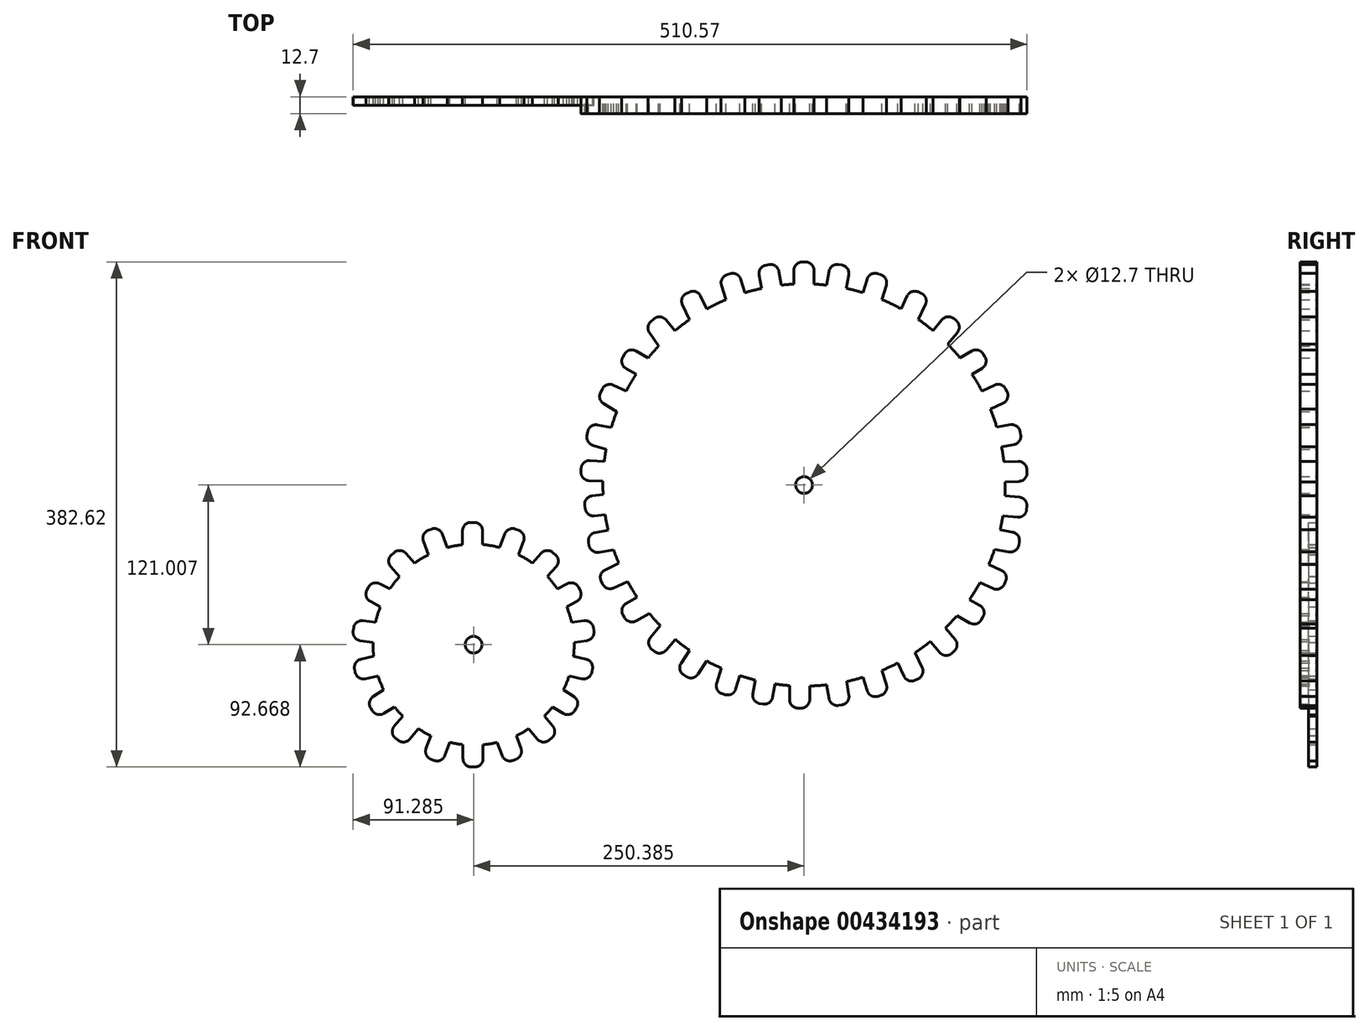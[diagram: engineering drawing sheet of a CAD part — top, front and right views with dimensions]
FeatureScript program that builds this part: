
annotation { "Feature Type Name" : "Feature", "Feature Type Description" : "" }
export const myFeature = defineFeature(function(context is Context, id is Id, definition is map)
    precondition{}
    {
        {
            var Q0;
            Q0=qCreatedBy(makeId("Front.planeOp"),FACE);
            var sketch = newSketch(context, id + "F0", { "sketchPlane" : qUnion([Q0])});
            skCircle(sketch, "E0", {"center": v(106.38, 71.68) * mm, "radius": 152.4 * mm});
            skCircle(sketch, "E1", {"center": v(-144, -49.32) * mm, "radius": 76.2 * mm});
            skCircle(sketch, "E2", {"center": v(-144, -49.32) * mm, "radius": 6.35 * mm});
            skCircle(sketch, "E3", {"center": v(106.38, 71.68) * mm, "radius": 6.35 * mm});
            skSolve(sketch);
        }
        {
            var Q0;
            Q0=makeQuery(id+"F0.imprint","IMPRINT",FACE,{"disambiguationData":[TD([[makeQuery(id+"F0.imprint","IMPRINT",EDGE,{"derivedFrom":sQuery(id+"F0.wireOp",EDGE,"E0")}),1.0]])]});
            extrude(context, id + "F1", {"entities" : qUnion([Q0]), "depth" : 12.7 * mm});
        }
        {
            var Q0;
            Q0 = qSketchRegion(id + "F0", true);
            extrude(context, id + "F2", {"entities" : qUnion([Q0]), "depth" : 6.35 * mm});
        }
        {
            var Q0;
            Q0=qCreatedBy(makeId("Front.planeOp"),FACE);
            var sketch = newSketch(context, id + "F3", { "sketchPlane" : qUnion([Q0])});
            skLineSegment(sketch, "E4.bottom", {"start": v(-146.1, 43.29) * mm, "end": v(-143.56, 43.29) * mm});
            skLineSegment(sketch, "E4.top", {"start": v(-152.45, 22.97) * mm, "end": v(-137.2, 22.97) * mm});
            skLineSegment(sketch, "E4.left", {"start": v(-152.45, 36.94) * mm, "end": v(-152.45, 22.97) * mm});
            skLineSegment(sketch, "E4.right", {"start": v(-137.2, 36.94) * mm, "end": v(-137.2, 22.97) * mm});
            skLineSegment(sketch, "E5", {"start": v(-136.92, 40.56) * mm, "end": v(-135.42, 26.4) * mm});
            skLineSegment(sketch, "E6", {"start": v(-137.2, 22.97) * mm, "end": v(-138.5, 22.97) * mm});
            skLineSegment(sketch, "E7", {"start": v(-152.67, 40.47) * mm, "end": v(-153.76, 26.25) * mm});
            skLineSegment(sketch, "E8", {"start": v(-152.45, 22.97) * mm, "end": v(-150.72, 22.97) * mm});
            skPoint(sketch, "E9.visualSharp", {"position": v(-152.45, 43.29) * mm});
            skArc(sketch, "E9.filletArc", {"start": v(-149.63, 43.29) * mm, "mid": v(-151.7, 42.48) * mm, "end": v(-152.67, 40.47) * mm});
            skPoint(sketch, "E10.visualSharp", {"position": v(-137.2, 43.29) * mm});
            skArc(sketch, "E10.filletArc", {"start": v(-136.92, 40.56) * mm, "mid": v(-137.91, 42.5) * mm, "end": v(-139.95, 43.29) * mm});
            skPoint(sketch, "E11.visualSharp", {"position": v(-154.01, 22.97) * mm});
            skArc(sketch, "E11.filletArc", {"start": v(-153.76, 26.25) * mm, "mid": v(-152.96, 23.95) * mm, "end": v(-150.72, 22.97) * mm});
            skPoint(sketch, "E12.visualSharp", {"position": v(-135.06, 22.97) * mm});
            skArc(sketch, "E12.filletArc", {"start": v(-138.5, 22.97) * mm, "mid": v(-136.2, 24) * mm, "end": v(-135.42, 26.4) * mm});
            skLineSegment(sketch, "E13.MirrorCS", {"start": v(-136.79, -121.67) * mm, "end": v(-138.04, -121.67) * mm});
            skLineSegment(sketch, "E14.MirrorCS", {"start": v(-152.03, -121.67) * mm, "end": v(-150.3, -121.67) * mm});
            skArc(sketch, "E15.MirrorCS", {"start": v(-138.04, -121.67) * mm, "mid": v(-135.8, -122.66) * mm, "end": v(-135.01, -124.99) * mm});
            skArc(sketch, "E16.MirrorCS", {"start": v(-149.2, -141.99) * mm, "mid": v(-151.28, -141.18) * mm, "end": v(-152.24, -139.17) * mm});
            skArc(sketch, "E17.MirrorCS", {"start": v(-136.5, -139.21) * mm, "mid": v(-137.48, -141.19) * mm, "end": v(-139.53, -141.99) * mm});
            skArc(sketch, "E18.MirrorCS", {"start": v(-153.34, -124.95) * mm, "mid": v(-152.54, -122.64) * mm, "end": v(-150.3, -121.67) * mm});
            skPoint(sketch, "E19.MirrorP", {"position": v(-152.03, -141.99) * mm});
            skLineSegment(sketch, "E20.MirrorCS", {"start": v(-152.03, -121.67) * mm, "end": v(-136.79, -121.67) * mm});
            skLineSegment(sketch, "E21.MirrorCS", {"start": v(-136.5, -139.21) * mm, "end": v(-135.01, -124.99) * mm});
            skPoint(sketch, "E22.MirrorP", {"position": v(-135, -124.52) * mm});
            skPoint(sketch, "E23.MirrorP", {"position": v(-136.79, -141.99) * mm});
            skLineSegment(sketch, "E24.MirrorCS", {"start": v(-152.03, -135.64) * mm, "end": v(-152.03, -121.67) * mm});
            skLineSegment(sketch, "E25.MirrorCS", {"start": v(-152.24, -139.17) * mm, "end": v(-153.34, -124.95) * mm});
            skLineSegment(sketch, "E26.MirrorCS", {"start": v(-145.68, -141.99) * mm, "end": v(-143.14, -141.99) * mm});
            skLineSegment(sketch, "E27.MirrorCS", {"start": v(-136.79, -135.64) * mm, "end": v(-136.79, -121.67) * mm});
            skPoint(sketch, "E28.MirrorP", {"position": v(-153.94, -124.52) * mm});
            skLineSegment(sketch, "E29.bottom", {"start": v(-178.32, 37.32) * mm, "end": v(-175.94, 38.23) * mm});
            skLineSegment(sketch, "E29.top", {"start": v(-176.8, 15.57) * mm, "end": v(-162.56, 21.01) * mm});
            skLineSegment(sketch, "E29.left", {"start": v(-181.98, 29.13) * mm, "end": v(-176.8, 15.57) * mm});
            skLineSegment(sketch, "E29.right", {"start": v(-167.75, 34.57) * mm, "end": v(-162.56, 21.01) * mm});
            skLineSegment(sketch, "E30", {"start": v(-168.8, 37.96) * mm, "end": v(-162.41, 24.62) * mm});
            skLineSegment(sketch, "E31", {"start": v(-162.56, 21.01) * mm, "end": v(-164.08, 20.43) * mm});
            skLineSegment(sketch, "E32", {"start": v(-183.5, 32.38) * mm, "end": v(-179.51, 18.1) * mm});
            skLineSegment(sketch, "E33", {"start": v(-176.8, 15.57) * mm, "end": v(-175.49, 16.07) * mm});
            skPoint(sketch, "E34.visualSharp", {"position": v(-184.25, 35.06) * mm});
            skArc(sketch, "E34.filletArc", {"start": v(-181.65, 36.05) * mm, "mid": v(-183.29, 34.57) * mm, "end": v(-183.5, 32.38) * mm});
            skPoint(sketch, "E35.visualSharp", {"position": v(-170.01, 40.5) * mm});
            skArc(sketch, "E35.filletArc", {"start": v(-168.8, 37.96) * mm, "mid": v(-170.42, 39.48) * mm, "end": v(-172.64, 39.5) * mm});
            skPoint(sketch, "E36.visualSharp", {"position": v(-178.61, 14.88) * mm});
            skArc(sketch, "E36.filletArc", {"start": v(-179.51, 18.1) * mm, "mid": v(-177.95, 16.2) * mm, "end": v(-175.49, 16.07) * mm});
            skPoint(sketch, "E37.visualSharp", {"position": v(-160.97, 21.62) * mm});
            skArc(sketch, "E37.filletArc", {"start": v(-164.08, 20.43) * mm, "mid": v(-162.33, 22.16) * mm, "end": v(-162.41, 24.62) * mm});
            skLineSegment(sketch, "E38.0", {"start": v(-162.56, 21.01) * mm, "end": v(-160.97, 21.62) * mm, "construction": true});
            skLineSegment(sketch, "E39.0", {"start": v(-178.61, 14.88) * mm, "end": v(-176.8, 15.57) * mm, "construction": true});
            skLineSegment(sketch, "E40.bottom", {"start": v(-206.24, 18.7) * mm, "end": v(-204.35, 20.4) * mm});
            skLineSegment(sketch, "E40.top", {"start": v(-197.6, -0.33) * mm, "end": v(-186.3, 9.88) * mm});
            skLineSegment(sketch, "E40.left", {"start": v(-206.7, 9.73) * mm, "end": v(-197.6, -0.33) * mm});
            skLineSegment(sketch, "E40.right", {"start": v(-195.39, 19.95) * mm, "end": v(-186.3, 9.88) * mm});
            skLineSegment(sketch, "E41", {"start": v(-197.6, 22.9) * mm, "end": v(-186.87, 13.68) * mm});
            skLineSegment(sketch, "E42", {"start": v(-186.3, 9.88) * mm, "end": v(-186.82, 9.4) * mm});
            skLineSegment(sketch, "E43", {"start": v(-209.38, 12.24) * mm, "end": v(-201.32, 0.9) * mm});
            skLineSegment(sketch, "E44", {"start": v(-197.6, -0.33) * mm, "end": v(-196.8, 0.4) * mm});
            skPoint(sketch, "E45.visualSharp", {"position": v(-210.95, 14.45) * mm});
            skArc(sketch, "E45.filletArc", {"start": v(-208.94, 16.26) * mm, "mid": v(-209.93, 14.33) * mm, "end": v(-209.38, 12.24) * mm});
            skPoint(sketch, "E46.visualSharp", {"position": v(-199.64, 24.66) * mm});
            skArc(sketch, "E46.filletArc", {"start": v(-197.6, 22.9) * mm, "mid": v(-199.63, 23.65) * mm, "end": v(-201.64, 22.86) * mm});
            skPoint(sketch, "E47.visualSharp", {"position": v(-199.33, -1.9) * mm});
            skArc(sketch, "E47.filletArc", {"start": v(-201.32, 0.9) * mm, "mid": v(-199.17, -0.37) * mm, "end": v(-196.8, 0.4) * mm});
            skPoint(sketch, "E48.visualSharp", {"position": v(-184.42, 11.57) * mm});
            skArc(sketch, "E48.filletArc", {"start": v(-186.82, 9.4) * mm, "mid": v(-185.88, 11.55) * mm, "end": v(-186.87, 13.68) * mm});
            skLineSegment(sketch, "E49.0", {"start": v(-186.3, 9.88) * mm, "end": v(-184.42, 11.57) * mm, "construction": true});
            skLineSegment(sketch, "E50.0", {"start": v(-199.33, -1.9) * mm, "end": v(-197.6, -0.33) * mm, "construction": true});
            skLineSegment(sketch, "E51.bottom", {"start": v(-224.8, -8.03) * mm, "end": v(-223.6, -5.78) * mm});
            skLineSegment(sketch, "E51.top", {"start": v(-211.59, -22.22) * mm, "end": v(-204.45, -8.76) * mm});
            skLineSegment(sketch, "E51.left", {"start": v(-222.16, -16.61) * mm, "end": v(-211.59, -22.22) * mm});
            skLineSegment(sketch, "E51.right", {"start": v(-215.02, -3.15) * mm, "end": v(-204.45, -8.76) * mm});
            skLineSegment(sketch, "E52", {"start": v(-218.1, -1.16) * mm, "end": v(-206.48, -5.7) * mm});
            skLineSegment(sketch, "E53", {"start": v(-204.45, -8.76) * mm, "end": v(-204.98, -9.76) * mm});
            skLineSegment(sketch, "E54", {"start": v(-225.38, -15.15) * mm, "end": v(-215.02, -21.7) * mm});
            skLineSegment(sketch, "E55", {"start": v(-211.59, -22.22) * mm, "end": v(-210.7, -20.55) * mm});
            skPoint(sketch, "E56.visualSharp", {"position": v(-227.77, -13.64) * mm});
            skArc(sketch, "E56.filletArc", {"start": v(-226.45, -11.14) * mm, "mid": v(-226.7, -13.35) * mm, "end": v(-225.38, -15.15) * mm});
            skPoint(sketch, "E57.visualSharp", {"position": v(-220.63, -0.17) * mm});
            skArc(sketch, "E57.filletArc", {"start": v(-218.1, -1.16) * mm, "mid": v(-220.27, -1.14) * mm, "end": v(-221.9, -2.57) * mm});
            skPoint(sketch, "E58.visualSharp", {"position": v(-212.24, -23.46) * mm});
            skArc(sketch, "E58.filletArc", {"start": v(-215.02, -21.7) * mm, "mid": v(-212.61, -22.07) * mm, "end": v(-210.7, -20.55) * mm});
            skPoint(sketch, "E59.visualSharp", {"position": v(-203.45, -6.89) * mm});
            skArc(sketch, "E59.filletArc", {"start": v(-204.98, -9.76) * mm, "mid": v(-204.82, -7.4) * mm, "end": v(-206.48, -5.7) * mm});
            skLineSegment(sketch, "E60.0", {"start": v(-212.24, -23.46) * mm, "end": v(-211.59, -22.22) * mm, "construction": true});
            skLineSegment(sketch, "E61.0", {"start": v(-204.45, -8.76) * mm, "end": v(-203.45, -6.89) * mm, "construction": true});
            skLineSegment(sketch, "E62.bottom", {"start": v(-235.23, -39.12) * mm, "end": v(-234.88, -36.6) * mm});
            skLineSegment(sketch, "E62.top", {"start": v(-216.79, -48.1) * mm, "end": v(-214.69, -33) * mm});
            skLineSegment(sketch, "E62.left", {"start": v(-229.81, -46.29) * mm, "end": v(-216.79, -48.1) * mm});
            skLineSegment(sketch, "E62.right", {"start": v(-227.7, -31.2) * mm, "end": v(-214.69, -33) * mm});
            skLineSegment(sketch, "E63", {"start": v(-231.27, -30.4) * mm, "end": v(-217.91, -30.78) * mm});
            skLineSegment(sketch, "E64", {"start": v(-214.69, -33) * mm, "end": v(-214.88, -34.37) * mm});
            skLineSegment(sketch, "E65", {"start": v(-233.34, -46) * mm, "end": v(-220.2, -48.86) * mm});
            skLineSegment(sketch, "E66", {"start": v(-216.79, -48.1) * mm, "end": v(-216.54, -46.3) * mm});
            skPoint(sketch, "E67.visualSharp", {"position": v(-236.1, -45.4) * mm});
            skArc(sketch, "E67.filletArc", {"start": v(-235.71, -42.6) * mm, "mid": v(-235.2, -44.77) * mm, "end": v(-233.34, -46) * mm});
            skPoint(sketch, "E68.visualSharp", {"position": v(-234, -30.32) * mm});
            skArc(sketch, "E68.filletArc", {"start": v(-231.27, -30.4) * mm, "mid": v(-233.32, -31.11) * mm, "end": v(-234.38, -33.02) * mm});
            skPoint(sketch, "E69.visualSharp", {"position": v(-217, -49.55) * mm});
            skArc(sketch, "E69.filletArc", {"start": v(-220.2, -48.86) * mm, "mid": v(-217.81, -48.38) * mm, "end": v(-216.54, -46.3) * mm});
            skPoint(sketch, "E70.visualSharp", {"position": v(-214.4, -30.88) * mm});
            skArc(sketch, "E70.filletArc", {"start": v(-214.88, -34.37) * mm, "mid": v(-215.6, -31.9) * mm, "end": v(-217.91, -30.78) * mm});
            skLineSegment(sketch, "E71.0", {"start": v(-217, -49.55) * mm, "end": v(-216.79, -48.1) * mm, "construction": true});
            skLineSegment(sketch, "E72.0", {"start": v(-214.69, -33) * mm, "end": v(-214.4, -30.88) * mm, "construction": true});
            skLineSegment(sketch, "E73.bottom", {"start": v(-233.61, -70.43) * mm, "end": v(-234.16, -67.95) * mm});
            skLineSegment(sketch, "E73.top", {"start": v(-213.05, -72.38) * mm, "end": v(-216.34, -57.5) * mm});
            skLineSegment(sketch, "E73.left", {"start": v(-226.04, -75.26) * mm, "end": v(-213.05, -72.38) * mm});
            skLineSegment(sketch, "E73.right", {"start": v(-229.33, -60.38) * mm, "end": v(-216.34, -57.5) * mm});
            skLineSegment(sketch, "E74", {"start": v(-232.94, -60.87) * mm, "end": v(-219.87, -56.47) * mm});
            skLineSegment(sketch, "E75", {"start": v(-216.34, -57.5) * mm, "end": v(-216.1, -58.6) * mm});
            skLineSegment(sketch, "E76", {"start": v(-229.45, -76.24) * mm, "end": v(-215.98, -74.35) * mm});
            skLineSegment(sketch, "E77", {"start": v(-213.05, -72.38) * mm, "end": v(-213.42, -70.68) * mm});
            skPoint(sketch, "E78.visualSharp", {"position": v(-232.24, -76.63) * mm});
            skArc(sketch, "E78.filletArc", {"start": v(-232.85, -73.88) * mm, "mid": v(-231.61, -75.72) * mm, "end": v(-229.45, -76.24) * mm});
            skPoint(sketch, "E79.visualSharp", {"position": v(-235.53, -61.75) * mm});
            skArc(sketch, "E79.filletArc", {"start": v(-232.94, -60.87) * mm, "mid": v(-234.62, -62.26) * mm, "end": v(-234.94, -64.42) * mm});
            skPoint(sketch, "E80.visualSharp", {"position": v(-212.71, -73.9) * mm});
            skArc(sketch, "E80.filletArc", {"start": v(-215.98, -74.35) * mm, "mid": v(-213.9, -73.07) * mm, "end": v(-213.42, -70.68) * mm});
            skPoint(sketch, "E81.visualSharp", {"position": v(-216.8, -55.43) * mm});
            skArc(sketch, "E81.filletArc", {"start": v(-216.1, -58.6) * mm, "mid": v(-217.5, -56.7) * mm, "end": v(-219.87, -56.47) * mm});
            skLineSegment(sketch, "E82.0", {"start": v(-212.71, -73.9) * mm, "end": v(-213.05, -72.38) * mm, "construction": true});
            skLineSegment(sketch, "E83.0", {"start": v(-216.34, -57.5) * mm, "end": v(-216.8, -55.43) * mm, "construction": true});
            skLineSegment(sketch, "E84.bottom", {"start": v(-220.62, -99.46) * mm, "end": v(-221.98, -97.3) * mm});
            skLineSegment(sketch, "E84.top", {"start": v(-201.01, -94.6) * mm, "end": v(-209.14, -81.7) * mm});
            skLineSegment(sketch, "E84.left", {"start": v(-211.86, -101.44) * mm, "end": v(-201.01, -94.6) * mm});
            skLineSegment(sketch, "E84.right", {"start": v(-220, -88.55) * mm, "end": v(-209.14, -81.7) * mm});
            skLineSegment(sketch, "E85", {"start": v(-223.23, -90.24) * mm, "end": v(-212.86, -81.96) * mm});
            skLineSegment(sketch, "E86", {"start": v(-209.14, -81.7) * mm, "end": v(-208.52, -82.7) * mm});
            skLineSegment(sketch, "E87", {"start": v(-214.74, -103.51) * mm, "end": v(-203.13, -97.4) * mm});
            skLineSegment(sketch, "E88", {"start": v(-201.01, -94.6) * mm, "end": v(-201.97, -93.07) * mm});
            skPoint(sketch, "E89.visualSharp", {"position": v(-217.23, -104.83) * mm});
            skArc(sketch, "E89.filletArc", {"start": v(-218.74, -102.44) * mm, "mid": v(-216.95, -103.76) * mm, "end": v(-214.74, -103.51) * mm});
            skPoint(sketch, "E90.visualSharp", {"position": v(-225.37, -91.94) * mm});
            skArc(sketch, "E90.filletArc", {"start": v(-223.23, -90.24) * mm, "mid": v(-224.34, -92.11) * mm, "end": v(-223.9, -94.24) * mm});
            skPoint(sketch, "E91.visualSharp", {"position": v(-200.21, -95.86) * mm});
            skArc(sketch, "E91.filletArc", {"start": v(-203.13, -97.4) * mm, "mid": v(-201.6, -95.49) * mm, "end": v(-201.97, -93.07) * mm});
            skPoint(sketch, "E92.visualSharp", {"position": v(-210.28, -79.9) * mm});
            skArc(sketch, "E92.filletArc", {"start": v(-208.52, -82.7) * mm, "mid": v(-210.52, -81.36) * mm, "end": v(-212.86, -81.96) * mm});
            skLineSegment(sketch, "E93.0", {"start": v(-200.21, -95.86) * mm, "end": v(-201.01, -94.6) * mm, "construction": true});
            skLineSegment(sketch, "E94.0", {"start": v(-209.14, -81.7) * mm, "end": v(-210.28, -79.9) * mm, "construction": true});
            skLineSegment(sketch, "E95.bottom", {"start": v(-201.4, -121.68) * mm, "end": v(-203.35, -120.05) * mm});
            skLineSegment(sketch, "E95.top", {"start": v(-183.63, -110.37) * mm, "end": v(-195.3, -100.57) * mm});
            skLineSegment(sketch, "E95.left", {"start": v(-192.46, -120.9) * mm, "end": v(-183.63, -110.37) * mm});
            skLineSegment(sketch, "E95.right", {"start": v(-204.14, -111.1) * mm, "end": v(-195.3, -100.57) * mm});
            skLineSegment(sketch, "E96", {"start": v(-206.7, -113.7) * mm, "end": v(-198.93, -102.14) * mm});
            skLineSegment(sketch, "E97", {"start": v(-195.3, -100.57) * mm, "end": v(-194.24, -101.47) * mm});
            skLineSegment(sketch, "E98", {"start": v(-194.57, -123.75) * mm, "end": v(-184.75, -113.72) * mm});
            skLineSegment(sketch, "E99", {"start": v(-183.63, -110.37) * mm, "end": v(-184.96, -109.25) * mm});
            skPoint(sketch, "E100.visualSharp", {"position": v(-196.54, -125.76) * mm});
            skArc(sketch, "E100.filletArc", {"start": v(-198.7, -123.95) * mm, "mid": v(-196.6, -124.66) * mm, "end": v(-194.57, -123.75) * mm});
            skPoint(sketch, "E101.visualSharp", {"position": v(-208.22, -115.97) * mm});
            skArc(sketch, "E101.filletArc", {"start": v(-206.7, -113.7) * mm, "mid": v(-207.18, -115.82) * mm, "end": v(-206.12, -117.73) * mm});
            skPoint(sketch, "E102.visualSharp", {"position": v(-182.44, -111.37) * mm});
            skArc(sketch, "E102.filletArc", {"start": v(-184.75, -113.72) * mm, "mid": v(-183.88, -111.44) * mm, "end": v(-184.96, -109.25) * mm});
            skPoint(sketch, "E103.visualSharp", {"position": v(-196.96, -99.19) * mm});
            skArc(sketch, "E103.filletArc", {"start": v(-194.24, -101.47) * mm, "mid": v(-196.73, -100.76) * mm, "end": v(-198.93, -102.14) * mm});
            skLineSegment(sketch, "E104.0", {"start": v(-182.44, -111.37) * mm, "end": v(-183.63, -110.37) * mm, "construction": true});
            skLineSegment(sketch, "E105.0", {"start": v(-195.3, -100.57) * mm, "end": v(-196.96, -99.19) * mm, "construction": true});
            skLineSegment(sketch, "E106.bottom", {"start": v(-173.8, -137.08) * mm, "end": v(-176.2, -136.2) * mm});
            skLineSegment(sketch, "E106.top", {"start": v(-160.88, -120.12) * mm, "end": v(-175.2, -114.92) * mm});
            skLineSegment(sketch, "E106.left", {"start": v(-165.67, -133.28) * mm, "end": v(-160.88, -120.12) * mm});
            skLineSegment(sketch, "E106.right", {"start": v(-180, -128.07) * mm, "end": v(-175.2, -114.92) * mm});
            skLineSegment(sketch, "E107", {"start": v(-181.5, -131.38) * mm, "end": v(-178.04, -117.5) * mm});
            skLineSegment(sketch, "E108", {"start": v(-175.2, -114.92) * mm, "end": v(-174, -115.35) * mm});
            skLineSegment(sketch, "E109", {"start": v(-166.67, -136.68) * mm, "end": v(-160.78, -123.65) * mm});
            skLineSegment(sketch, "E110", {"start": v(-160.88, -120.12) * mm, "end": v(-162.51, -119.53) * mm});
            skPoint(sketch, "E111.visualSharp", {"position": v(-167.84, -139.25) * mm});
            skArc(sketch, "E111.filletArc", {"start": v(-170.5, -138.28) * mm, "mid": v(-168.27, -138.23) * mm, "end": v(-166.67, -136.68) * mm});
            skPoint(sketch, "E112.visualSharp", {"position": v(-182.16, -134.04) * mm});
            skArc(sketch, "E112.filletArc", {"start": v(-181.5, -131.38) * mm, "mid": v(-181.23, -133.55) * mm, "end": v(-179.58, -134.98) * mm});
            skPoint(sketch, "E113.visualSharp", {"position": v(-159.42, -120.66) * mm});
            skArc(sketch, "E113.filletArc", {"start": v(-160.78, -123.65) * mm, "mid": v(-160.74, -121.21) * mm, "end": v(-162.51, -119.53) * mm});
            skPoint(sketch, "E114.visualSharp", {"position": v(-177.22, -114.19) * mm});
            skArc(sketch, "E114.filletArc", {"start": v(-174, -115.35) * mm, "mid": v(-176.5, -115.53) * mm, "end": v(-178.04, -117.5) * mm});
            skLineSegment(sketch, "E115.0", {"start": v(-159.42, -120.66) * mm, "end": v(-160.88, -120.12) * mm, "construction": true});
            skLineSegment(sketch, "E116.0", {"start": v(-175.2, -114.92) * mm, "end": v(-177.22, -114.19) * mm, "construction": true});
            skLineSegment(sketch, "E117", {"start": v(-144.05, -49.16) * mm, "end": v(-144.05, -125.7) * mm, "construction": true});
            skLineSegment(sketch, "E118", {"start": v(-144.05, -125.7) * mm, "end": v(-144.05, 26.61) * mm, "construction": true});
            skLineSegment(sketch, "E119.MirrorCS", {"start": v(-111.3, 15.57) * mm, "end": v(-112.61, 16.07) * mm});
            skLineSegment(sketch, "E120.MirrorCS", {"start": v(-87.1, -94.6) * mm, "end": v(-86.13, -93.07) * mm});
            skLineSegment(sketch, "E121.MirrorCS", {"start": v(-71.77, -57.5) * mm, "end": v(-72, -58.6) * mm});
            skLineSegment(sketch, "E122.MirrorCS", {"start": v(-125.54, 21.01) * mm, "end": v(-127.13, 21.62) * mm, "construction": true});
            skArc(sketch, "E123.MirrorCS", {"start": v(-108.59, 18.1) * mm, "mid": v(-110.15, 16.2) * mm, "end": v(-112.61, 16.07) * mm});
            skLineSegment(sketch, "E124.MirrorCS", {"start": v(-75.86, -23.46) * mm, "end": v(-76.52, -22.22) * mm, "construction": true});
            skLineSegment(sketch, "E125.MirrorCS", {"start": v(-105.66, -111.37) * mm, "end": v(-104.47, -110.37) * mm, "construction": true});
            skLineSegment(sketch, "E126.MirrorCS", {"start": v(-87.9, -95.86) * mm, "end": v(-87.1, -94.6) * mm, "construction": true});
            skLineSegment(sketch, "E127.MirrorCS", {"start": v(-75.06, -72.38) * mm, "end": v(-74.68, -70.68) * mm});
            skLineSegment(sketch, "E128.MirrorCS", {"start": v(-71.31, -48.1) * mm, "end": v(-71.56, -46.3) * mm});
            skLineSegment(sketch, "E129.MirrorCS", {"start": v(-127.22, -120.12) * mm, "end": v(-125.6, -119.53) * mm});
            skArc(sketch, "E130.MirrorCS", {"start": v(-84.98, -97.4) * mm, "mid": v(-86.5, -95.49) * mm, "end": v(-86.13, -93.07) * mm});
            skLineSegment(sketch, "E131.MirrorCS", {"start": v(-78.96, -81.7) * mm, "end": v(-79.59, -82.7) * mm});
            skLineSegment(sketch, "E132.MirrorCS", {"start": v(-112.9, -114.92) * mm, "end": v(-114.1, -115.35) * mm});
            skLineSegment(sketch, "E133.MirrorCS", {"start": v(-78.96, -81.7) * mm, "end": v(-77.83, -79.9) * mm, "construction": true});
            skLineSegment(sketch, "E134.MirrorCS", {"start": v(-76.52, -22.22) * mm, "end": v(-77.4, -20.55) * mm});
            skLineSegment(sketch, "E135.MirrorCS", {"start": v(-109.49, 14.88) * mm, "end": v(-111.3, 15.57) * mm, "construction": true});
            skLineSegment(sketch, "E136.MirrorCS", {"start": v(-104.47, -110.37) * mm, "end": v(-103.14, -109.25) * mm});
            skLineSegment(sketch, "E137.MirrorCS", {"start": v(-71.77, -57.5) * mm, "end": v(-71.3, -55.43) * mm, "construction": true});
            skLineSegment(sketch, "E138.MirrorCS", {"start": v(-71.11, -49.55) * mm, "end": v(-71.31, -48.1) * mm, "construction": true});
            skLineSegment(sketch, "E139.MirrorCS", {"start": v(-128.68, -120.66) * mm, "end": v(-127.22, -120.12) * mm, "construction": true});
            skLineSegment(sketch, "E140.MirrorCS", {"start": v(-125.54, 21.01) * mm, "end": v(-124.02, 20.43) * mm});
            skLineSegment(sketch, "E141.MirrorCS", {"start": v(-92.8, -100.57) * mm, "end": v(-91.15, -99.19) * mm, "construction": true});
            skArc(sketch, "E142.MirrorCS", {"start": v(-83.12, -9.76) * mm, "mid": v(-83.28, -7.4) * mm, "end": v(-81.62, -5.7) * mm});
            skLineSegment(sketch, "E143.MirrorCS", {"start": v(-73.42, -33) * mm, "end": v(-73.71, -30.88) * mm, "construction": true});
            skLineSegment(sketch, "E144.MirrorCS", {"start": v(-75.4, -73.9) * mm, "end": v(-75.06, -72.38) * mm, "construction": true});
            skArc(sketch, "E145.MirrorCS", {"start": v(-72.13, -74.35) * mm, "mid": v(-74.2, -73.07) * mm, "end": v(-74.68, -70.68) * mm});
            skLineSegment(sketch, "E146.MirrorCS", {"start": v(-83.66, -8.76) * mm, "end": v(-83.12, -9.76) * mm});
            skLineSegment(sketch, "E147.MirrorCS", {"start": v(-92.8, -100.57) * mm, "end": v(-93.87, -101.47) * mm});
            skLineSegment(sketch, "E148.MirrorCS", {"start": v(-83.66, -8.76) * mm, "end": v(-84.65, -6.89) * mm, "construction": true});
            skLineSegment(sketch, "E149.MirrorCS", {"start": v(-73.42, -33) * mm, "end": v(-73.23, -34.37) * mm});
            skLineSegment(sketch, "E150.MirrorCS", {"start": v(-112.9, -114.92) * mm, "end": v(-110.89, -114.19) * mm, "construction": true});
            skLineSegment(sketch, "E151.MirrorCS", {"start": v(-101.81, 9.88) * mm, "end": v(-101.29, 9.4) * mm});
            skArc(sketch, "E152.MirrorCS", {"start": v(-114.1, -115.35) * mm, "mid": v(-111.6, -115.53) * mm, "end": v(-110.06, -117.5) * mm});
            skLineSegment(sketch, "E153.MirrorCS", {"start": v(-101.81, 9.88) * mm, "end": v(-103.68, 11.57) * mm, "construction": true});
            skLineSegment(sketch, "E154.MirrorCS", {"start": v(-88.77, -1.9) * mm, "end": v(-90.5, -0.33) * mm, "construction": true});
            skLineSegment(sketch, "E155.MirrorCS", {"start": v(-90.5, -0.33) * mm, "end": v(-91.31, 0.4) * mm});
            skArc(sketch, "E156.MirrorCS", {"start": v(-101.29, 9.4) * mm, "mid": v(-102.23, 11.55) * mm, "end": v(-101.23, 13.68) * mm});
            skArc(sketch, "E157.MirrorCS", {"start": v(-79.59, -82.7) * mm, "mid": v(-77.58, -81.36) * mm, "end": v(-75.24, -81.96) * mm});
            skArc(sketch, "E158.MirrorCS", {"start": v(-103.36, -113.72) * mm, "mid": v(-104.22, -111.44) * mm, "end": v(-103.14, -109.25) * mm});
            skArc(sketch, "E159.MirrorCS", {"start": v(-89.4, -123.95) * mm, "mid": v(-91.5, -124.66) * mm, "end": v(-93.53, -123.75) * mm});
            skArc(sketch, "E160.MirrorCS", {"start": v(-72, -58.6) * mm, "mid": v(-70.6, -56.7) * mm, "end": v(-68.23, -56.47) * mm});
            skArc(sketch, "E161.MirrorCS", {"start": v(-56.83, -30.4) * mm, "mid": v(-54.78, -31.11) * mm, "end": v(-53.73, -33.02) * mm});
            skArc(sketch, "E162.MirrorCS", {"start": v(-119.3, 37.96) * mm, "mid": v(-117.68, 39.48) * mm, "end": v(-115.47, 39.5) * mm});
            skArc(sketch, "E163.MirrorCS", {"start": v(-81.4, -113.7) * mm, "mid": v(-80.92, -115.82) * mm, "end": v(-81.98, -117.73) * mm});
            skArc(sketch, "E164.MirrorCS", {"start": v(-93.87, -101.47) * mm, "mid": v(-91.37, -100.76) * mm, "end": v(-89.17, -102.14) * mm});
            skArc(sketch, "E165.MirrorCS", {"start": v(-106.45, 36.05) * mm, "mid": v(-104.82, 34.57) * mm, "end": v(-104.6, 32.38) * mm});
            skArc(sketch, "E166.MirrorCS", {"start": v(-86.79, 0.9) * mm, "mid": v(-88.94, -0.37) * mm, "end": v(-91.31, 0.4) * mm});
            skArc(sketch, "E167.MirrorCS", {"start": v(-64.87, -90.24) * mm, "mid": v(-63.77, -92.11) * mm, "end": v(-64.2, -94.24) * mm});
            skArc(sketch, "E168.MirrorCS", {"start": v(-52.4, -42.6) * mm, "mid": v(-52.91, -44.77) * mm, "end": v(-54.76, -46) * mm});
            skArc(sketch, "E169.MirrorCS", {"start": v(-55.16, -60.87) * mm, "mid": v(-53.48, -62.26) * mm, "end": v(-53.16, -64.42) * mm});
            skArc(sketch, "E170.MirrorCS", {"start": v(-90.5, 22.9) * mm, "mid": v(-88.47, 23.65) * mm, "end": v(-86.47, 22.86) * mm});
            skArc(sketch, "E171.MirrorCS", {"start": v(-117.61, -138.28) * mm, "mid": v(-119.84, -138.23) * mm, "end": v(-121.43, -136.68) * mm});
            skArc(sketch, "E172.MirrorCS", {"start": v(-67.9, -48.86) * mm, "mid": v(-70.3, -48.38) * mm, "end": v(-71.56, -46.3) * mm});
            skArc(sketch, "E173.MirrorCS", {"start": v(-106.6, -131.38) * mm, "mid": v(-106.87, -133.55) * mm, "end": v(-108.52, -134.98) * mm});
            skArc(sketch, "E174.MirrorCS", {"start": v(-124.02, 20.43) * mm, "mid": v(-125.77, 22.16) * mm, "end": v(-125.7, 24.62) * mm});
            skArc(sketch, "E175.MirrorCS", {"start": v(-55.25, -73.88) * mm, "mid": v(-56.5, -75.72) * mm, "end": v(-58.65, -76.24) * mm});
            skArc(sketch, "E176.MirrorCS", {"start": v(-127.33, -123.65) * mm, "mid": v(-127.36, -121.21) * mm, "end": v(-125.6, -119.53) * mm});
            skArc(sketch, "E177.MirrorCS", {"start": v(-61.66, -11.14) * mm, "mid": v(-61.4, -13.35) * mm, "end": v(-62.72, -15.15) * mm});
            skArc(sketch, "E178.MirrorCS", {"start": v(-73.08, -21.7) * mm, "mid": v(-75.5, -22.07) * mm, "end": v(-77.4, -20.55) * mm});
            skArc(sketch, "E179.MirrorCS", {"start": v(-70, -1.16) * mm, "mid": v(-67.83, -1.14) * mm, "end": v(-66.2, -2.57) * mm});
            skArc(sketch, "E180.MirrorCS", {"start": v(-73.23, -34.37) * mm, "mid": v(-72.51, -31.9) * mm, "end": v(-70.19, -30.78) * mm});
            skArc(sketch, "E181.MirrorCS", {"start": v(-79.16, 16.26) * mm, "mid": v(-78.18, 14.33) * mm, "end": v(-78.72, 12.24) * mm});
            skArc(sketch, "E182.MirrorCS", {"start": v(-69.37, -102.44) * mm, "mid": v(-71.16, -103.76) * mm, "end": v(-73.36, -103.51) * mm});
            skLineSegment(sketch, "E183.MirrorCS", {"start": v(-114.3, -137.08) * mm, "end": v(-111.91, -136.2) * mm});
            skLineSegment(sketch, "E184.MirrorCS", {"start": v(-67.48, -99.46) * mm, "end": v(-66.13, -97.3) * mm});
            skLineSegment(sketch, "E185.MirrorCS", {"start": v(-86.7, -121.68) * mm, "end": v(-84.75, -120.05) * mm});
            skPoint(sketch, "E186.MirrorP", {"position": v(-134.1, 22.97) * mm});
            skPoint(sketch, "E187.MirrorP", {"position": v(-128.68, -120.66) * mm});
            skPoint(sketch, "E188.MirrorP", {"position": v(-87.9, -95.86) * mm});
            skLineSegment(sketch, "E189.MirrorCS", {"start": v(-109.79, 37.32) * mm, "end": v(-112.16, 38.23) * mm});
            skPoint(sketch, "E190.MirrorP", {"position": v(-70.87, -104.83) * mm});
            skLineSegment(sketch, "E191.MirrorCS", {"start": v(-60.4, -31.2) * mm, "end": v(-73.42, -33) * mm});
            skLineSegment(sketch, "E192.MirrorCS", {"start": v(-73.36, -103.51) * mm, "end": v(-84.98, -97.4) * mm});
            skLineSegment(sketch, "E193.MirrorCS", {"start": v(-56.83, -30.4) * mm, "end": v(-70.19, -30.78) * mm});
            skPoint(sketch, "E194.MirrorP", {"position": v(-52.57, -61.75) * mm});
            skPoint(sketch, "E195.MirrorP", {"position": v(-118.1, 40.5) * mm});
            skLineSegment(sketch, "E196.MirrorCS", {"start": v(-63.3, -8.03) * mm, "end": v(-64.5, -5.78) * mm});
            skLineSegment(sketch, "E197.MirrorCS", {"start": v(-71.31, -48.1) * mm, "end": v(-73.42, -33) * mm});
            skLineSegment(sketch, "E198.MirrorCS", {"start": v(-78.72, 12.24) * mm, "end": v(-86.79, 0.9) * mm});
            skPoint(sketch, "E199.MirrorP", {"position": v(-134.16, -124.52) * mm});
            skPoint(sketch, "E200.MirrorP", {"position": v(-109.49, 14.88) * mm});
            skLineSegment(sketch, "E201.MirrorCS", {"start": v(-65.94, -16.61) * mm, "end": v(-76.52, -22.22) * mm});
            skPoint(sketch, "E202.MirrorP", {"position": v(-67.48, -0.17) * mm});
            skLineSegment(sketch, "E203.MirrorCS", {"start": v(-81.86, 18.7) * mm, "end": v(-83.75, 20.4) * mm});
            skLineSegment(sketch, "E204.MirrorCS", {"start": v(-81.4, 9.73) * mm, "end": v(-90.5, -0.33) * mm});
            skPoint(sketch, "E205.MirrorP", {"position": v(-73.71, -30.88) * mm});
            skLineSegment(sketch, "E206.MirrorCS", {"start": v(-52.88, -39.12) * mm, "end": v(-53.23, -36.6) * mm});
            skLineSegment(sketch, "E207.MirrorCS", {"start": v(-58.3, -46.29) * mm, "end": v(-71.31, -48.1) * mm});
            skLineSegment(sketch, "E208.MirrorCS", {"start": v(-90.5, -0.33) * mm, "end": v(-101.81, 9.88) * mm});
            skLineSegment(sketch, "E209.MirrorCS", {"start": v(-70, -1.16) * mm, "end": v(-81.62, -5.7) * mm});
            skPoint(sketch, "E210.MirrorP", {"position": v(-127.13, 21.62) * mm});
            skLineSegment(sketch, "E211.MirrorCS", {"start": v(-76.24, -101.44) * mm, "end": v(-87.1, -94.6) * mm});
            skPoint(sketch, "E212.MirrorP", {"position": v(-75.86, -23.46) * mm});
            skPoint(sketch, "E213.MirrorP", {"position": v(-75.4, -73.9) * mm});
            skPoint(sketch, "E214.MirrorP", {"position": v(-79.88, -115.97) * mm});
            skLineSegment(sketch, "E215.MirrorCS", {"start": v(-54.76, -46) * mm, "end": v(-67.9, -48.86) * mm});
            skPoint(sketch, "E216.MirrorP", {"position": v(-60.33, -13.64) * mm});
            skPoint(sketch, "E217.MirrorP", {"position": v(-52, -45.4) * mm});
            skLineSegment(sketch, "E218.MirrorCS", {"start": v(-122.44, -133.28) * mm, "end": v(-127.22, -120.12) * mm});
            skPoint(sketch, "E219.MirrorP", {"position": v(-55.86, -76.63) * mm});
            skLineSegment(sketch, "E220.MirrorCS", {"start": v(-106.12, 29.13) * mm, "end": v(-111.3, 15.57) * mm});
            skPoint(sketch, "E221.MirrorP", {"position": v(-103.68, 11.57) * mm});
            skLineSegment(sketch, "E222.MirrorCS", {"start": v(-62.06, -75.26) * mm, "end": v(-75.06, -72.38) * mm});
            skLineSegment(sketch, "E223.MirrorCS", {"start": v(-92.72, 19.95) * mm, "end": v(-101.81, 9.88) * mm});
            skPoint(sketch, "E224.MirrorP", {"position": v(-71.3, -55.43) * mm});
            skPoint(sketch, "E225.MirrorP", {"position": v(-91.15, -99.19) * mm});
            skLineSegment(sketch, "E226.MirrorCS", {"start": v(-111.3, 15.57) * mm, "end": v(-125.54, 21.01) * mm});
            skLineSegment(sketch, "E227.MirrorCS", {"start": v(-75.06, -72.38) * mm, "end": v(-71.77, -57.5) * mm});
            skLineSegment(sketch, "E228.MirrorCS", {"start": v(-68.1, -88.55) * mm, "end": v(-78.96, -81.7) * mm});
            skPoint(sketch, "E229.MirrorP", {"position": v(-88.77, -1.9) * mm});
            skLineSegment(sketch, "E230.MirrorCS", {"start": v(-121.43, -136.68) * mm, "end": v(-127.33, -123.65) * mm});
            skLineSegment(sketch, "E231.MirrorCS", {"start": v(-83.96, -111.1) * mm, "end": v(-92.8, -100.57) * mm});
            skLineSegment(sketch, "E232.MirrorCS", {"start": v(-64.87, -90.24) * mm, "end": v(-75.24, -81.96) * mm});
            skLineSegment(sketch, "E233.MirrorCS", {"start": v(-93.53, -123.75) * mm, "end": v(-103.36, -113.72) * mm});
            skLineSegment(sketch, "E234.MirrorCS", {"start": v(-58.77, -60.38) * mm, "end": v(-71.77, -57.5) * mm});
            skPoint(sketch, "E235.MirrorP", {"position": v(-71.11, -49.55) * mm});
            skLineSegment(sketch, "E236.MirrorCS", {"start": v(-87.1, -94.6) * mm, "end": v(-78.96, -81.7) * mm});
            skLineSegment(sketch, "E237.MirrorCS", {"start": v(-54.5, -70.43) * mm, "end": v(-53.94, -67.95) * mm});
            skPoint(sketch, "E238.MirrorP", {"position": v(-77.15, 14.45) * mm});
            skPoint(sketch, "E239.MirrorP", {"position": v(-77.83, -79.9) * mm});
            skPoint(sketch, "E240.MirrorP", {"position": v(-110.89, -114.19) * mm});
            skPoint(sketch, "E241.MirrorP", {"position": v(-84.65, -6.89) * mm});
            skPoint(sketch, "E242.MirrorP", {"position": v(-105.66, -111.37) * mm});
            skLineSegment(sketch, "E243.MirrorCS", {"start": v(-120.36, 34.57) * mm, "end": v(-125.54, 21.01) * mm});
            skLineSegment(sketch, "E244.MirrorCS", {"start": v(-127.22, -120.12) * mm, "end": v(-112.9, -114.92) * mm});
            skLineSegment(sketch, "E245.MirrorCS", {"start": v(-62.72, -15.15) * mm, "end": v(-73.08, -21.7) * mm});
            skLineSegment(sketch, "E246.MirrorCS", {"start": v(-76.52, -22.22) * mm, "end": v(-83.66, -8.76) * mm});
            skLineSegment(sketch, "E247.MirrorCS", {"start": v(-81.4, -113.7) * mm, "end": v(-89.17, -102.14) * mm});
            skPoint(sketch, "E248.MirrorP", {"position": v(-103.85, 35.06) * mm});
            skLineSegment(sketch, "E249.MirrorCS", {"start": v(-90.5, 22.9) * mm, "end": v(-101.23, 13.68) * mm});
            skLineSegment(sketch, "E250.MirrorCS", {"start": v(-58.65, -76.24) * mm, "end": v(-72.13, -74.35) * mm});
            skLineSegment(sketch, "E251.MirrorCS", {"start": v(-55.16, -60.87) * mm, "end": v(-68.23, -56.47) * mm});
            skPoint(sketch, "E252.MirrorP", {"position": v(-91.56, -125.76) * mm});
            skLineSegment(sketch, "E253.MirrorCS", {"start": v(-104.47, -110.37) * mm, "end": v(-92.8, -100.57) * mm});
            skPoint(sketch, "E254.MirrorP", {"position": v(-105.94, -134.04) * mm});
            skPoint(sketch, "E255.MirrorP", {"position": v(-54.1, -30.32) * mm});
            skLineSegment(sketch, "E256.MirrorCS", {"start": v(-108.11, -128.07) * mm, "end": v(-112.9, -114.92) * mm});
            skPoint(sketch, "E257.MirrorP", {"position": v(-120.27, -139.25) * mm});
            skLineSegment(sketch, "E258.MirrorCS", {"start": v(-119.3, 37.96) * mm, "end": v(-125.7, 24.62) * mm});
            skLineSegment(sketch, "E259.MirrorCS", {"start": v(-106.6, -131.38) * mm, "end": v(-110.06, -117.5) * mm});
            skPoint(sketch, "E260.MirrorP", {"position": v(-62.74, -91.94) * mm});
            skLineSegment(sketch, "E261.MirrorCS", {"start": v(-73.08, -3.15) * mm, "end": v(-83.66, -8.76) * mm});
            skPoint(sketch, "E262.MirrorP", {"position": v(-88.46, 24.66) * mm});
            skLineSegment(sketch, "E263.MirrorCS", {"start": v(-104.6, 32.38) * mm, "end": v(-108.59, 18.1) * mm});
            skLineSegment(sketch, "E264.MirrorCS", {"start": v(-95.64, -120.9) * mm, "end": v(-104.47, -110.37) * mm});
            skArc(sketch, "E265.filletArc", {"start": v(-137.2, 36.94) * mm, "mid": v(-139.07, 41.43) * mm, "end": v(-143.56, 43.29) * mm});
            skArc(sketch, "E266.filletArc", {"start": v(-146.1, 43.29) * mm, "mid": v(-150.59, 41.43) * mm, "end": v(-152.45, 36.94) * mm});
            skPoint(sketch, "E267.newPointA", {"position": v(-172.64, 39.5) * mm});
            skArc(sketch, "E267.filletArc", {"start": v(-167.75, 34.57) * mm, "mid": v(-171.09, 38.1) * mm, "end": v(-175.94, 38.23) * mm});
            skPoint(sketch, "E268.newPointA", {"position": v(-181.65, 36.05) * mm});
            skArc(sketch, "E268.filletArc", {"start": v(-178.32, 37.32) * mm, "mid": v(-181.85, 33.98) * mm, "end": v(-181.98, 29.13) * mm});
            skPoint(sketch, "E269.newPointA", {"position": v(-201.64, 22.86) * mm});
            skArc(sketch, "E269.filletArc", {"start": v(-195.39, 19.95) * mm, "mid": v(-199.78, 22.03) * mm, "end": v(-204.35, 20.4) * mm});
            skPoint(sketch, "E270.newPointA", {"position": v(-208.94, 16.26) * mm});
            skArc(sketch, "E270.filletArc", {"start": v(-206.24, 18.7) * mm, "mid": v(-208.32, 14.31) * mm, "end": v(-206.7, 9.73) * mm});
            skPoint(sketch, "E271.newPointA", {"position": v(-221.9, -2.57) * mm});
            skArc(sketch, "E271.filletArc", {"start": v(-215.02, -3.15) * mm, "mid": v(-219.86, -2.69) * mm, "end": v(-223.6, -5.78) * mm});
            skPoint(sketch, "E272.newPointA", {"position": v(-226.45, -11.14) * mm});
            skArc(sketch, "E272.filletArc", {"start": v(-224.8, -8.03) * mm, "mid": v(-225.25, -12.87) * mm, "end": v(-222.16, -16.61) * mm});
            skPoint(sketch, "E273.newPointA", {"position": v(-234.38, -33.02) * mm});
            skArc(sketch, "E273.filletArc", {"start": v(-227.7, -31.2) * mm, "mid": v(-232.41, -32.41) * mm, "end": v(-234.88, -36.6) * mm});
            skPoint(sketch, "E274.newPointA", {"position": v(-235.71, -42.6) * mm});
            skArc(sketch, "E274.filletArc", {"start": v(-235.23, -39.12) * mm, "mid": v(-234, -43.82) * mm, "end": v(-229.81, -46.29) * mm});
            skPoint(sketch, "E275.newPointA", {"position": v(-106.45, 36.05) * mm});
            skArc(sketch, "E275.filletArc", {"start": v(-106.12, 29.13) * mm, "mid": v(-106.26, 33.98) * mm, "end": v(-109.79, 37.32) * mm});
            skPoint(sketch, "E276.newPointA", {"position": v(-115.47, 39.5) * mm});
            skArc(sketch, "E276.filletArc", {"start": v(-112.16, 38.23) * mm, "mid": v(-117.02, 38.1) * mm, "end": v(-120.36, 34.57) * mm});
            skPoint(sketch, "E277.newPointA", {"position": v(-79.16, 16.26) * mm});
            skArc(sketch, "E277.filletArc", {"start": v(-81.4, 9.73) * mm, "mid": v(-79.78, 14.31) * mm, "end": v(-81.86, 18.7) * mm});
            skPoint(sketch, "E278.newPointA", {"position": v(-86.47, 22.86) * mm});
            skArc(sketch, "E278.filletArc", {"start": v(-83.75, 20.4) * mm, "mid": v(-88.33, 22.03) * mm, "end": v(-92.72, 19.95) * mm});
            skPoint(sketch, "E279.newPointA", {"position": v(-61.66, -11.14) * mm});
            skArc(sketch, "E279.filletArc", {"start": v(-65.94, -16.61) * mm, "mid": v(-62.85, -12.87) * mm, "end": v(-63.3, -8.03) * mm});
            skPoint(sketch, "E280.newPointA", {"position": v(-66.2, -2.57) * mm});
            skArc(sketch, "E280.filletArc", {"start": v(-64.5, -5.78) * mm, "mid": v(-68.25, -2.69) * mm, "end": v(-73.08, -3.15) * mm});
            skPoint(sketch, "E281.newPointA", {"position": v(-234.94, -64.42) * mm});
            skArc(sketch, "E281.filletArc", {"start": v(-229.33, -60.38) * mm, "mid": v(-233.32, -63.16) * mm, "end": v(-234.16, -67.95) * mm});
            skPoint(sketch, "E282.newPointA", {"position": v(-232.85, -73.88) * mm});
            skArc(sketch, "E282.filletArc", {"start": v(-233.61, -70.43) * mm, "mid": v(-230.83, -74.41) * mm, "end": v(-226.04, -75.26) * mm});
            skPoint(sketch, "E283.newPointA", {"position": v(-223.9, -94.24) * mm});
            skArc(sketch, "E283.filletArc", {"start": v(-220, -88.55) * mm, "mid": v(-222.8, -92.52) * mm, "end": v(-221.98, -97.3) * mm});
            skPoint(sketch, "E284.newPointA", {"position": v(-218.74, -102.44) * mm});
            skArc(sketch, "E284.filletArc", {"start": v(-220.62, -99.46) * mm, "mid": v(-216.65, -102.26) * mm, "end": v(-211.86, -101.44) * mm});
            skPoint(sketch, "E285.newPointA", {"position": v(-206.12, -117.73) * mm});
            skArc(sketch, "E285.filletArc", {"start": v(-204.14, -111.1) * mm, "mid": v(-205.6, -115.74) * mm, "end": v(-203.35, -120.05) * mm});
            skPoint(sketch, "E286.newPointA", {"position": v(-198.7, -123.95) * mm});
            skArc(sketch, "E286.filletArc", {"start": v(-201.4, -121.68) * mm, "mid": v(-196.77, -123.14) * mm, "end": v(-192.46, -120.9) * mm});
            skPoint(sketch, "E287.newPointA", {"position": v(-170.5, -138.28) * mm});
            skArc(sketch, "E287.filletArc", {"start": v(-173.8, -137.08) * mm, "mid": v(-168.95, -136.86) * mm, "end": v(-165.67, -133.28) * mm});
            skPoint(sketch, "E288.newPointB", {"position": v(-179.58, -134.98) * mm});
            skArc(sketch, "E288.filletArc", {"start": v(-180, -128.07) * mm, "mid": v(-179.78, -132.93) * mm, "end": v(-176.2, -136.2) * mm});
            skArc(sketch, "E289.filletArc", {"start": v(-152.03, -135.64) * mm, "mid": v(-150.17, -140.13) * mm, "end": v(-145.68, -141.99) * mm});
            skArc(sketch, "E290.filletArc", {"start": v(-143.14, -141.99) * mm, "mid": v(-138.65, -140.13) * mm, "end": v(-136.79, -135.64) * mm});
            skPoint(sketch, "E291.newPointB", {"position": v(-108.52, -134.98) * mm});
            skArc(sketch, "E291.filletArc", {"start": v(-111.91, -136.2) * mm, "mid": v(-108.33, -132.93) * mm, "end": v(-108.11, -128.07) * mm});
            skPoint(sketch, "E292.newPointB", {"position": v(-117.61, -138.28) * mm});
            skArc(sketch, "E292.filletArc", {"start": v(-122.44, -133.28) * mm, "mid": v(-119.15, -136.86) * mm, "end": v(-114.3, -137.08) * mm});
            skPoint(sketch, "E293.newPointB", {"position": v(-89.4, -123.95) * mm});
            skArc(sketch, "E293.filletArc", {"start": v(-95.64, -120.9) * mm, "mid": v(-91.33, -123.14) * mm, "end": v(-86.7, -121.68) * mm});
            skPoint(sketch, "E294.newPointB", {"position": v(-81.98, -117.73) * mm});
            skArc(sketch, "E294.filletArc", {"start": v(-84.75, -120.05) * mm, "mid": v(-82.5, -115.74) * mm, "end": v(-83.96, -111.1) * mm});
            skPoint(sketch, "E295.newPointB", {"position": v(-64.2, -94.24) * mm});
            skArc(sketch, "E295.filletArc", {"start": v(-66.13, -97.3) * mm, "mid": v(-65.3, -92.52) * mm, "end": v(-68.1, -88.55) * mm});
            skPoint(sketch, "E296.newPointB", {"position": v(-69.37, -102.44) * mm});
            skArc(sketch, "E296.filletArc", {"start": v(-76.24, -101.44) * mm, "mid": v(-71.45, -102.26) * mm, "end": v(-67.48, -99.46) * mm});
            skPoint(sketch, "E297.newPointB", {"position": v(-55.25, -73.88) * mm});
            skArc(sketch, "E297.filletArc", {"start": v(-62.06, -75.26) * mm, "mid": v(-57.28, -74.41) * mm, "end": v(-54.5, -70.43) * mm});
            skPoint(sketch, "E298.newPointB", {"position": v(-53.16, -64.42) * mm});
            skArc(sketch, "E298.filletArc", {"start": v(-53.94, -67.95) * mm, "mid": v(-54.79, -63.16) * mm, "end": v(-58.77, -60.38) * mm});
            skPoint(sketch, "E299.newPointB", {"position": v(-53.73, -33.02) * mm});
            skArc(sketch, "E299.filletArc", {"start": v(-53.23, -36.6) * mm, "mid": v(-55.69, -32.41) * mm, "end": v(-60.4, -31.2) * mm});
            skPoint(sketch, "E300.newPointB", {"position": v(-52.4, -42.6) * mm});
            skArc(sketch, "E300.filletArc", {"start": v(-58.3, -46.29) * mm, "mid": v(-54.1, -43.82) * mm, "end": v(-52.88, -39.12) * mm});
            skSolve(sketch);
        }
        {
            var Q0;
            {var subQ11=sQuery(id+"F3.wireOp",EDGE,"E40.bottom");Q0=makeQuery(id+"F3.imprint","IMPRINT",FACE,{"disambiguationData":[TD([[makeQuery(id+"F3.imprint","IMPRINT",EDGE,{"derivedFrom":subQ11}),-1.0]])]});}
            var Q1;
            {var subQ5=sQuery(id+"F3.wireOp",EDGE,"E43");Q1=makeQuery(id+"F3.imprint","IMPRINT",FACE,{"disambiguationData":[TD([[makeQuery(id+"F3.imprint","IMPRINT",EDGE,{"derivedFrom":subQ5}),1.0]])]});}
            var Q2;
            {var subQ5=sQuery(id+"F3.wireOp",EDGE,"E41");Q2=makeQuery(id+"F3.imprint","IMPRINT",FACE,{"disambiguationData":[TD([[makeQuery(id+"F3.imprint","IMPRINT",EDGE,{"derivedFrom":subQ5}),-1.0]])]});}
            var Q3;
            {var subQ11=sQuery(id+"F3.wireOp",EDGE,"E29.bottom");Q3=makeQuery(id+"F3.imprint","IMPRINT",FACE,{"disambiguationData":[TD([[makeQuery(id+"F3.imprint","IMPRINT",EDGE,{"derivedFrom":subQ11}),-1.0]])]});}
            var Q4;
            {var subQ5=sQuery(id+"F3.wireOp",EDGE,"E32");Q4=makeQuery(id+"F3.imprint","IMPRINT",FACE,{"disambiguationData":[TD([[makeQuery(id+"F3.imprint","IMPRINT",EDGE,{"derivedFrom":subQ5}),1.0]])]});}
            var Q5;
            {var subQ5=sQuery(id+"F3.wireOp",EDGE,"E30");Q5=makeQuery(id+"F3.imprint","IMPRINT",FACE,{"disambiguationData":[TD([[makeQuery(id+"F3.imprint","IMPRINT",EDGE,{"derivedFrom":subQ5}),-1.0]])]});}
            var Q6;
            {var subQ5=sQuery(id+"F3.wireOp",EDGE,"E7");Q6=makeQuery(id+"F3.imprint","IMPRINT",FACE,{"disambiguationData":[TD([[makeQuery(id+"F3.imprint","IMPRINT",EDGE,{"derivedFrom":subQ5}),1.0]])]});}
            var Q7;
            {var subQ11=sQuery(id+"F3.wireOp",EDGE,"E4.bottom");Q7=makeQuery(id+"F3.imprint","IMPRINT",FACE,{"disambiguationData":[TD([[makeQuery(id+"F3.imprint","IMPRINT",EDGE,{"derivedFrom":subQ11}),-1.0]])]});}
            var Q8;
            {var subQ5=sQuery(id+"F3.wireOp",EDGE,"E5");Q8=makeQuery(id+"F3.imprint","IMPRINT",FACE,{"disambiguationData":[TD([[makeQuery(id+"F3.imprint","IMPRINT",EDGE,{"derivedFrom":subQ5}),-1.0]])]});}
            var Q9;
            {var subQ0=sQuery(id+"F3.wireOp",EDGE,"9ce58062-a104-4fe8-a601-26132dddf8bc139.MirrorCS");Q9=makeQuery(id+"F3.imprint","IMPRINT",FACE,{"disambiguationData":[TD([[makeQuery(id+"F3.imprint","IMPRINT",EDGE,{"derivedFrom":subQ0}),1.0]])]});}
            var Q10;
            {var subQ0=sQuery(id+"F3.wireOp",EDGE,"9ce58062-a104-4fe8-a601-26132dddf8bc82.MirrorCS");Q10=makeQuery(id+"F3.imprint","IMPRINT",FACE,{"disambiguationData":[TD([[makeQuery(id+"F3.imprint","IMPRINT",EDGE,{"derivedFrom":subQ0}),-1.0]])]});}
            var Q11;
            {var subQ0=sQuery(id+"F3.wireOp",EDGE,"9ce58062-a104-4fe8-a601-26132dddf8bc109.MirrorCS");Q11=makeQuery(id+"F3.imprint","IMPRINT",FACE,{"disambiguationData":[TD([[makeQuery(id+"F3.imprint","IMPRINT",EDGE,{"derivedFrom":subQ0}),1.0]])]});}
            var Q12;
            {var subQ0=sQuery(id+"F3.wireOp",EDGE,"9ce58062-a104-4fe8-a601-26132dddf8bc123.MirrorCS");Q12=makeQuery(id+"F3.imprint","IMPRINT",FACE,{"disambiguationData":[TD([[makeQuery(id+"F3.imprint","IMPRINT",EDGE,{"derivedFrom":subQ0}),1.0]])]});}
            var Q13;
            {var subQ9=sQuery(id+"F3.wireOp",EDGE,"9ce58062-a104-4fe8-a601-26132dddf8bc95.MirrorCS");Q13=makeQuery(id+"F3.imprint","IMPRINT",FACE,{"disambiguationData":[TD([[makeQuery(id+"F3.imprint","IMPRINT",EDGE,{"derivedFrom":subQ9}),1.0]])]});}
            var Q14;
            {var subQ0=sQuery(id+"F3.wireOp",EDGE,"9ce58062-a104-4fe8-a601-26132dddf8bc140.MirrorCS");Q14=makeQuery(id+"F3.imprint","IMPRINT",FACE,{"disambiguationData":[TD([[makeQuery(id+"F3.imprint","IMPRINT",EDGE,{"derivedFrom":subQ0}),-1.0]])]});}
            var Q15;
            {var subQ0=sQuery(id+"F3.wireOp",EDGE,"9ce58062-a104-4fe8-a601-26132dddf8bc108.MirrorCS");Q15=makeQuery(id+"F3.imprint","IMPRINT",FACE,{"disambiguationData":[TD([[makeQuery(id+"F3.imprint","IMPRINT",EDGE,{"derivedFrom":subQ0}),1.0]])]});}
            var Q16;
            {var subQ0=sQuery(id+"F3.wireOp",EDGE,"9ce58062-a104-4fe8-a601-26132dddf8bc69.MirrorCS");Q16=makeQuery(id+"F3.imprint","IMPRINT",FACE,{"disambiguationData":[TD([[makeQuery(id+"F3.imprint","IMPRINT",EDGE,{"derivedFrom":subQ0}),1.0]])]});}
            var Q17;
            {var subQ0=sQuery(id+"F3.wireOp",EDGE,"9ce58062-a104-4fe8-a601-26132dddf8bc122.MirrorCS");Q17=makeQuery(id+"F3.imprint","IMPRINT",FACE,{"disambiguationData":[TD([[makeQuery(id+"F3.imprint","IMPRINT",EDGE,{"derivedFrom":subQ0}),-1.0]])]});}
            var Q18;
            {var subQ0=sQuery(id+"F3.wireOp",EDGE,"9ce58062-a104-4fe8-a601-26132dddf8bc93.MirrorCS");Q18=makeQuery(id+"F3.imprint","IMPRINT",FACE,{"disambiguationData":[TD([[makeQuery(id+"F3.imprint","IMPRINT",EDGE,{"derivedFrom":subQ0}),1.0]])]});}
            var Q19;
            {var subQ0=sQuery(id+"F3.wireOp",EDGE,"9ce58062-a104-4fe8-a601-26132dddf8bc133.MirrorCS");Q19=makeQuery(id+"F3.imprint","IMPRINT",FACE,{"disambiguationData":[TD([[makeQuery(id+"F3.imprint","IMPRINT",EDGE,{"derivedFrom":subQ0}),1.0]])]});}
            var Q20;
            {var subQ0=sQuery(id+"F3.wireOp",EDGE,"9ce58062-a104-4fe8-a601-26132dddf8bc110.MirrorCS");Q20=makeQuery(id+"F3.imprint","IMPRINT",FACE,{"disambiguationData":[TD([[makeQuery(id+"F3.imprint","IMPRINT",EDGE,{"derivedFrom":subQ0}),-1.0]])]});}
            var Q21;
            {var subQ0=sQuery(id+"F3.wireOp",EDGE,"9ce58062-a104-4fe8-a601-26132dddf8bc71.MirrorCS");Q21=makeQuery(id+"F3.imprint","IMPRINT",FACE,{"disambiguationData":[TD([[makeQuery(id+"F3.imprint","IMPRINT",EDGE,{"derivedFrom":subQ0}),1.0]])]});}
            var Q22;
            {var subQ5=sQuery(id+"F3.wireOp",EDGE,"9ce58062-a104-4fe8-a601-26132dddf8bc98.MirrorCS");Q22=makeQuery(id+"F3.imprint","IMPRINT",FACE,{"disambiguationData":[TD([[makeQuery(id+"F3.imprint","IMPRINT",EDGE,{"derivedFrom":subQ5}),1.0]])]});}
            var Q23;
            {var subQ0=sQuery(id+"F3.wireOp",EDGE,"9ce58062-a104-4fe8-a601-26132dddf8bc92.MirrorCS");Q23=makeQuery(id+"F3.imprint","IMPRINT",FACE,{"disambiguationData":[TD([[makeQuery(id+"F3.imprint","IMPRINT",EDGE,{"derivedFrom":subQ0}),-1.0]])]});}
            var Q24;
            {var subQ0=sQuery(id+"F3.wireOp",EDGE,"9ce58062-a104-4fe8-a601-26132dddf8bc135.MirrorCS");Q24=makeQuery(id+"F3.imprint","IMPRINT",FACE,{"disambiguationData":[TD([[makeQuery(id+"F3.imprint","IMPRINT",EDGE,{"derivedFrom":subQ0}),1.0]])]});}
            var Q25;
            {var subQ10=sQuery(id+"F3.wireOp",EDGE,"9ce58062-a104-4fe8-a601-26132dddf8bc64.MirrorCS");Q25=makeQuery(id+"F3.imprint","IMPRINT",FACE,{"disambiguationData":[TD([[makeQuery(id+"F3.imprint","IMPRINT",EDGE,{"derivedFrom":subQ10}),1.0]])]});}
            var Q26;
            {var subQ0=sQuery(id+"F3.wireOp",EDGE,"9ce58062-a104-4fe8-a601-26132dddf8bc68.MirrorCS");Q26=makeQuery(id+"F3.imprint","IMPRINT",FACE,{"disambiguationData":[TD([[makeQuery(id+"F3.imprint","IMPRINT",EDGE,{"derivedFrom":subQ0}),-1.0]])]});}
            var Q27;
            {var subQ0=sQuery(id+"F3.wireOp",EDGE,"9ce58062-a104-4fe8-a601-26132dddf8bc100.MirrorCS");Q27=makeQuery(id+"F3.imprint","IMPRINT",FACE,{"disambiguationData":[TD([[makeQuery(id+"F3.imprint","IMPRINT",EDGE,{"derivedFrom":subQ0}),1.0]])]});}
            var Q28;
            {var subQ0=sQuery(id+"F3.wireOp",EDGE,"9ce58062-a104-4fe8-a601-26132dddf8bc134.MirrorCS");Q28=makeQuery(id+"F3.imprint","IMPRINT",FACE,{"disambiguationData":[TD([[makeQuery(id+"F3.imprint","IMPRINT",EDGE,{"derivedFrom":subQ0}),-1.0]])]});}
            var Q29;
            {var subQ0=sQuery(id+"F3.wireOp",EDGE,"9ce58062-a104-4fe8-a601-26132dddf8bc67.MirrorCS");Q29=makeQuery(id+"F3.imprint","IMPRINT",FACE,{"disambiguationData":[TD([[makeQuery(id+"F3.imprint","IMPRINT",EDGE,{"derivedFrom":subQ0}),1.0]])]});}
            var Q30;
            {var subQ0=sQuery(id+"F3.wireOp",EDGE,"9ce58062-a104-4fe8-a601-26132dddf8bc83.MirrorCS");Q30=makeQuery(id+"F3.imprint","IMPRINT",FACE,{"disambiguationData":[TD([[makeQuery(id+"F3.imprint","IMPRINT",EDGE,{"derivedFrom":subQ0}),1.0]])]});}
            var Q31;
            {var subQ0=sQuery(id+"F3.wireOp",EDGE,"9ce58062-a104-4fe8-a601-26132dddf8bc66.MirrorCS");Q31=makeQuery(id+"F3.imprint","IMPRINT",FACE,{"disambiguationData":[TD([[makeQuery(id+"F3.imprint","IMPRINT",EDGE,{"derivedFrom":subQ0}),1.0]])]});}
            var Q32;
            {var subQ0=sQuery(id+"F3.wireOp",EDGE,"9ce58062-a104-4fe8-a601-26132dddf8bc99.MirrorCS");Q32=makeQuery(id+"F3.imprint","IMPRINT",FACE,{"disambiguationData":[TD([[makeQuery(id+"F3.imprint","IMPRINT",EDGE,{"derivedFrom":subQ0}),-1.0]])]});}
            var Q33;
            {var subQ0=sQuery(id+"F3.wireOp",EDGE,"E21.MirrorCS");Q33=makeQuery(id+"F3.imprint","IMPRINT",FACE,{"disambiguationData":[TD([[makeQuery(id+"F3.imprint","IMPRINT",EDGE,{"derivedFrom":subQ0}),1.0]])]});}
            var Q34;
            {var subQ5=sQuery(id+"F3.wireOp",EDGE,"E26.MirrorCS");Q34=makeQuery(id+"F3.imprint","IMPRINT",FACE,{"disambiguationData":[TD([[makeQuery(id+"F3.imprint","IMPRINT",EDGE,{"derivedFrom":subQ5}),1.0]])]});}
            var Q35;
            {var subQ0=sQuery(id+"F3.wireOp",EDGE,"E25.MirrorCS");Q35=makeQuery(id+"F3.imprint","IMPRINT",FACE,{"disambiguationData":[TD([[makeQuery(id+"F3.imprint","IMPRINT",EDGE,{"derivedFrom":subQ0}),-1.0]])]});}
            var Q36;
            {var subQ5=sQuery(id+"F3.wireOp",EDGE,"E109");Q36=makeQuery(id+"F3.imprint","IMPRINT",FACE,{"disambiguationData":[TD([[makeQuery(id+"F3.imprint","IMPRINT",EDGE,{"derivedFrom":subQ5}),1.0]])]});}
            var Q37;
            {var subQ11=sQuery(id+"F3.wireOp",EDGE,"E106.bottom");Q37=makeQuery(id+"F3.imprint","IMPRINT",FACE,{"disambiguationData":[TD([[makeQuery(id+"F3.imprint","IMPRINT",EDGE,{"derivedFrom":subQ11}),-1.0]])]});}
            var Q38;
            {var subQ5=sQuery(id+"F3.wireOp",EDGE,"E107");Q38=makeQuery(id+"F3.imprint","IMPRINT",FACE,{"disambiguationData":[TD([[makeQuery(id+"F3.imprint","IMPRINT",EDGE,{"derivedFrom":subQ5}),-1.0]])]});}
            var Q39;
            {var subQ5=sQuery(id+"F3.wireOp",EDGE,"E98");Q39=makeQuery(id+"F3.imprint","IMPRINT",FACE,{"disambiguationData":[TD([[makeQuery(id+"F3.imprint","IMPRINT",EDGE,{"derivedFrom":subQ5}),1.0]])]});}
            var Q40;
            {var subQ11=sQuery(id+"F3.wireOp",EDGE,"E95.bottom");Q40=makeQuery(id+"F3.imprint","IMPRINT",FACE,{"disambiguationData":[TD([[makeQuery(id+"F3.imprint","IMPRINT",EDGE,{"derivedFrom":subQ11}),-1.0]])]});}
            var Q41;
            {var subQ5=sQuery(id+"F3.wireOp",EDGE,"E96");Q41=makeQuery(id+"F3.imprint","IMPRINT",FACE,{"disambiguationData":[TD([[makeQuery(id+"F3.imprint","IMPRINT",EDGE,{"derivedFrom":subQ5}),-1.0]])]});}
            var Q42;
            {var subQ5=sQuery(id+"F3.wireOp",EDGE,"E87");Q42=makeQuery(id+"F3.imprint","IMPRINT",FACE,{"disambiguationData":[TD([[makeQuery(id+"F3.imprint","IMPRINT",EDGE,{"derivedFrom":subQ5}),1.0]])]});}
            var Q43;
            {var subQ11=sQuery(id+"F3.wireOp",EDGE,"E84.bottom");Q43=makeQuery(id+"F3.imprint","IMPRINT",FACE,{"disambiguationData":[TD([[makeQuery(id+"F3.imprint","IMPRINT",EDGE,{"derivedFrom":subQ11}),-1.0]])]});}
            var Q44;
            {var subQ5=sQuery(id+"F3.wireOp",EDGE,"E85");Q44=makeQuery(id+"F3.imprint","IMPRINT",FACE,{"disambiguationData":[TD([[makeQuery(id+"F3.imprint","IMPRINT",EDGE,{"derivedFrom":subQ5}),-1.0]])]});}
            var Q45;
            {var subQ5=sQuery(id+"F3.wireOp",EDGE,"E76");Q45=makeQuery(id+"F3.imprint","IMPRINT",FACE,{"disambiguationData":[TD([[makeQuery(id+"F3.imprint","IMPRINT",EDGE,{"derivedFrom":subQ5}),1.0]])]});}
            var Q46;
            {var subQ11=sQuery(id+"F3.wireOp",EDGE,"E73.bottom");Q46=makeQuery(id+"F3.imprint","IMPRINT",FACE,{"disambiguationData":[TD([[makeQuery(id+"F3.imprint","IMPRINT",EDGE,{"derivedFrom":subQ11}),-1.0]])]});}
            var Q47;
            {var subQ5=sQuery(id+"F3.wireOp",EDGE,"E74");Q47=makeQuery(id+"F3.imprint","IMPRINT",FACE,{"disambiguationData":[TD([[makeQuery(id+"F3.imprint","IMPRINT",EDGE,{"derivedFrom":subQ5}),-1.0]])]});}
            var Q48;
            {var subQ5=sQuery(id+"F3.wireOp",EDGE,"E65");Q48=makeQuery(id+"F3.imprint","IMPRINT",FACE,{"disambiguationData":[TD([[makeQuery(id+"F3.imprint","IMPRINT",EDGE,{"derivedFrom":subQ5}),1.0]])]});}
            var Q49;
            {var subQ11=sQuery(id+"F3.wireOp",EDGE,"E62.bottom");Q49=makeQuery(id+"F3.imprint","IMPRINT",FACE,{"disambiguationData":[TD([[makeQuery(id+"F3.imprint","IMPRINT",EDGE,{"derivedFrom":subQ11}),-1.0]])]});}
            var Q50;
            {var subQ5=sQuery(id+"F3.wireOp",EDGE,"E63");Q50=makeQuery(id+"F3.imprint","IMPRINT",FACE,{"disambiguationData":[TD([[makeQuery(id+"F3.imprint","IMPRINT",EDGE,{"derivedFrom":subQ5}),-1.0]])]});}
            var Q51;
            {var subQ5=sQuery(id+"F3.wireOp",EDGE,"E54");Q51=makeQuery(id+"F3.imprint","IMPRINT",FACE,{"disambiguationData":[TD([[makeQuery(id+"F3.imprint","IMPRINT",EDGE,{"derivedFrom":subQ5}),1.0]])]});}
            var Q52;
            {var subQ11=sQuery(id+"F3.wireOp",EDGE,"E51.bottom");Q52=makeQuery(id+"F3.imprint","IMPRINT",FACE,{"disambiguationData":[TD([[makeQuery(id+"F3.imprint","IMPRINT",EDGE,{"derivedFrom":subQ11}),-1.0]])]});}
            var Q53;
            {var subQ5=sQuery(id+"F3.wireOp",EDGE,"E52");Q53=makeQuery(id+"F3.imprint","IMPRINT",FACE,{"disambiguationData":[TD([[makeQuery(id+"F3.imprint","IMPRINT",EDGE,{"derivedFrom":subQ5}),-1.0]])]});}
            var Q54;
            {var subQ5=sQuery(id+"F3.wireOp",EDGE,"E183.MirrorCS");Q54=makeQuery(id+"F3.imprint","IMPRINT",FACE,{"disambiguationData":[TD([[makeQuery(id+"F3.imprint","IMPRINT",EDGE,{"derivedFrom":subQ5}),1.0]])]});}
            var Q55;
            {var subQ0=sQuery(id+"F3.wireOp",EDGE,"E230.MirrorCS");Q55=makeQuery(id+"F3.imprint","IMPRINT",FACE,{"disambiguationData":[TD([[makeQuery(id+"F3.imprint","IMPRINT",EDGE,{"derivedFrom":subQ0}),-1.0]])]});}
            var Q56;
            {var subQ0=sQuery(id+"F3.wireOp",EDGE,"E259.MirrorCS");Q56=makeQuery(id+"F3.imprint","IMPRINT",FACE,{"disambiguationData":[TD([[makeQuery(id+"F3.imprint","IMPRINT",EDGE,{"derivedFrom":subQ0}),1.0]])]});}
            var Q57;
            {var subQ9=sQuery(id+"F3.wireOp",EDGE,"E185.MirrorCS");Q57=makeQuery(id+"F3.imprint","IMPRINT",FACE,{"disambiguationData":[TD([[makeQuery(id+"F3.imprint","IMPRINT",EDGE,{"derivedFrom":subQ9}),1.0]])]});}
            var Q58;
            {var subQ0=sQuery(id+"F3.wireOp",EDGE,"E247.MirrorCS");Q58=makeQuery(id+"F3.imprint","IMPRINT",FACE,{"disambiguationData":[TD([[makeQuery(id+"F3.imprint","IMPRINT",EDGE,{"derivedFrom":subQ0}),1.0]])]});}
            var Q59;
            {var subQ0=sQuery(id+"F3.wireOp",EDGE,"E233.MirrorCS");Q59=makeQuery(id+"F3.imprint","IMPRINT",FACE,{"disambiguationData":[TD([[makeQuery(id+"F3.imprint","IMPRINT",EDGE,{"derivedFrom":subQ0}),-1.0]])]});}
            var Q60;
            {var subQ0=sQuery(id+"F3.wireOp",EDGE,"E192.MirrorCS");Q60=makeQuery(id+"F3.imprint","IMPRINT",FACE,{"disambiguationData":[TD([[makeQuery(id+"F3.imprint","IMPRINT",EDGE,{"derivedFrom":subQ0}),-1.0]])]});}
            var Q61;
            {var subQ0=sQuery(id+"F3.wireOp",EDGE,"E184.MirrorCS");Q61=makeQuery(id+"F3.imprint","IMPRINT",FACE,{"disambiguationData":[TD([[makeQuery(id+"F3.imprint","IMPRINT",EDGE,{"derivedFrom":subQ0}),1.0]])]});}
            var Q62;
            {var subQ0=sQuery(id+"F3.wireOp",EDGE,"E232.MirrorCS");Q62=makeQuery(id+"F3.imprint","IMPRINT",FACE,{"disambiguationData":[TD([[makeQuery(id+"F3.imprint","IMPRINT",EDGE,{"derivedFrom":subQ0}),1.0]])]});}
            var Q63;
            {var subQ0=sQuery(id+"F3.wireOp",EDGE,"E237.MirrorCS");Q63=makeQuery(id+"F3.imprint","IMPRINT",FACE,{"disambiguationData":[TD([[makeQuery(id+"F3.imprint","IMPRINT",EDGE,{"derivedFrom":subQ0}),1.0]])]});}
            var Q64;
            {var subQ0=sQuery(id+"F3.wireOp",EDGE,"E251.MirrorCS");Q64=makeQuery(id+"F3.imprint","IMPRINT",FACE,{"disambiguationData":[TD([[makeQuery(id+"F3.imprint","IMPRINT",EDGE,{"derivedFrom":subQ0}),1.0]])]});}
            var Q65;
            {var subQ0=sQuery(id+"F3.wireOp",EDGE,"E250.MirrorCS");Q65=makeQuery(id+"F3.imprint","IMPRINT",FACE,{"disambiguationData":[TD([[makeQuery(id+"F3.imprint","IMPRINT",EDGE,{"derivedFrom":subQ0}),-1.0]])]});}
            var Q66;
            {var subQ0=sQuery(id+"F3.wireOp",EDGE,"E215.MirrorCS");Q66=makeQuery(id+"F3.imprint","IMPRINT",FACE,{"disambiguationData":[TD([[makeQuery(id+"F3.imprint","IMPRINT",EDGE,{"derivedFrom":subQ0}),-1.0]])]});}
            var Q67;
            {var subQ9=sQuery(id+"F3.wireOp",EDGE,"E206.MirrorCS");Q67=makeQuery(id+"F3.imprint","IMPRINT",FACE,{"disambiguationData":[TD([[makeQuery(id+"F3.imprint","IMPRINT",EDGE,{"derivedFrom":subQ9}),1.0]])]});}
            var Q68;
            {var subQ0=sQuery(id+"F3.wireOp",EDGE,"E193.MirrorCS");Q68=makeQuery(id+"F3.imprint","IMPRINT",FACE,{"disambiguationData":[TD([[makeQuery(id+"F3.imprint","IMPRINT",EDGE,{"derivedFrom":subQ0}),1.0]])]});}
            var Q69;
            {var subQ7=sQuery(id+"F3.wireOp",EDGE,"E196.MirrorCS");Q69=makeQuery(id+"F3.imprint","IMPRINT",FACE,{"disambiguationData":[TD([[makeQuery(id+"F3.imprint","IMPRINT",EDGE,{"derivedFrom":subQ7}),1.0]])]});}
            var Q70;
            {var subQ0=sQuery(id+"F3.wireOp",EDGE,"E245.MirrorCS");Q70=makeQuery(id+"F3.imprint","IMPRINT",FACE,{"disambiguationData":[TD([[makeQuery(id+"F3.imprint","IMPRINT",EDGE,{"derivedFrom":subQ0}),-1.0]])]});}
            var Q71;
            {var subQ0=sQuery(id+"F3.wireOp",EDGE,"E209.MirrorCS");Q71=makeQuery(id+"F3.imprint","IMPRINT",FACE,{"disambiguationData":[TD([[makeQuery(id+"F3.imprint","IMPRINT",EDGE,{"derivedFrom":subQ0}),1.0]])]});}
            var Q72;
            {var subQ0=sQuery(id+"F3.wireOp",EDGE,"E198.MirrorCS");Q72=makeQuery(id+"F3.imprint","IMPRINT",FACE,{"disambiguationData":[TD([[makeQuery(id+"F3.imprint","IMPRINT",EDGE,{"derivedFrom":subQ0}),-1.0]])]});}
            var Q73;
            {var subQ0=sQuery(id+"F3.wireOp",EDGE,"E203.MirrorCS");Q73=makeQuery(id+"F3.imprint","IMPRINT",FACE,{"disambiguationData":[TD([[makeQuery(id+"F3.imprint","IMPRINT",EDGE,{"derivedFrom":subQ0}),1.0]])]});}
            var Q74;
            {var subQ0=sQuery(id+"F3.wireOp",EDGE,"E249.MirrorCS");Q74=makeQuery(id+"F3.imprint","IMPRINT",FACE,{"disambiguationData":[TD([[makeQuery(id+"F3.imprint","IMPRINT",EDGE,{"derivedFrom":subQ0}),1.0]])]});}
            var Q75;
            {var subQ0=sQuery(id+"F3.wireOp",EDGE,"E263.MirrorCS");Q75=makeQuery(id+"F3.imprint","IMPRINT",FACE,{"disambiguationData":[TD([[makeQuery(id+"F3.imprint","IMPRINT",EDGE,{"derivedFrom":subQ0}),-1.0]])]});}
            var Q76;
            {var subQ0=sQuery(id+"F3.wireOp",EDGE,"E189.MirrorCS");Q76=makeQuery(id+"F3.imprint","IMPRINT",FACE,{"disambiguationData":[TD([[makeQuery(id+"F3.imprint","IMPRINT",EDGE,{"derivedFrom":subQ0}),1.0]])]});}
            var Q77;
            {var subQ0=sQuery(id+"F3.wireOp",EDGE,"E258.MirrorCS");Q77=makeQuery(id+"F3.imprint","IMPRINT",FACE,{"disambiguationData":[TD([[makeQuery(id+"F3.imprint","IMPRINT",EDGE,{"derivedFrom":subQ0}),1.0]])]});}
            extrude(context, id + "F4", {"entities" : qUnion([Q0, Q1, Q2, Q3, Q4, Q5, Q6, Q7, Q8, Q9, Q10, Q11, Q12, Q13, Q14, Q15, Q16, Q17, Q18, Q19, Q20, Q21, Q22, Q23, Q24, Q25, Q26, Q27, Q28, Q29, Q30, Q31, Q32, Q33, Q34, Q35, Q36, Q37, Q38, Q39, Q40, Q41, Q42, Q43, Q44, Q45, Q46, Q47, Q48, Q49, Q50, Q51, Q52, Q53, Q54, Q55, Q56, Q57, Q58, Q59, Q60, Q61, Q62, Q63, Q64, Q65, Q66, Q67, Q68, Q69, Q70, Q71, Q72, Q73, Q74, Q75, Q76, Q77]), "operationType" : NewBodyOperationType.ADD, "depth" : 6.35 * mm});
        }
        {
            var Q0;
            Q0=qCreatedBy(makeId("Front.planeOp"),FACE);
            var sketch = newSketch(context, id + "F5", { "sketchPlane" : qUnion([Q0])});
            skLineSegment(sketch, "E301.bottom", {"start": v(105.04, 240.63) * mm, "end": v(107.58, 240.63) * mm});
            skLineSegment(sketch, "E301.top", {"start": v(98.69, 220.3) * mm, "end": v(113.93, 220.3) * mm});
            skLineSegment(sketch, "E301.left", {"start": v(98.69, 234.28) * mm, "end": v(98.69, 220.3) * mm});
            skLineSegment(sketch, "E301.right", {"start": v(113.93, 234.28) * mm, "end": v(113.93, 220.3) * mm});
            skLineSegment(sketch, "E302", {"start": v(114.21, 237.9) * mm, "end": v(115.68, 223.97) * mm});
            skLineSegment(sketch, "E303", {"start": v(113.93, 220.3) * mm, "end": v(112.4, 220.3) * mm});
            skLineSegment(sketch, "E304", {"start": v(98.47, 237.81) * mm, "end": v(97.38, 223.59) * mm});
            skLineSegment(sketch, "E305", {"start": v(98.69, 220.3) * mm, "end": v(100.41, 220.3) * mm});
            skPoint(sketch, "E306.visualSharp", {"position": v(98.69, 240.63) * mm});
            skArc(sketch, "E306.filletArc", {"start": v(101.5, 240.63) * mm, "mid": v(99.44, 239.81) * mm, "end": v(98.47, 237.81) * mm});
            skPoint(sketch, "E307.visualSharp", {"position": v(113.93, 240.63) * mm});
            skArc(sketch, "E307.filletArc", {"start": v(114.21, 237.9) * mm, "mid": v(113.22, 239.84) * mm, "end": v(111.18, 240.63) * mm});
            skPoint(sketch, "E308.visualSharp", {"position": v(97.12, 220.3) * mm});
            skArc(sketch, "E308.filletArc", {"start": v(97.38, 223.59) * mm, "mid": v(98.18, 221.28) * mm, "end": v(100.41, 220.3) * mm});
            skPoint(sketch, "E309.visualSharp", {"position": v(116.07, 220.3) * mm});
            skArc(sketch, "E309.filletArc", {"start": v(112.4, 220.3) * mm, "mid": v(114.85, 221.4) * mm, "end": v(115.68, 223.97) * mm});
            skLineSegment(sketch, "E310.MirrorCS", {"start": v(110.64, -77.06) * mm, "end": v(109.1, -77.06) * mm});
            skArc(sketch, "E311.MirrorCS", {"start": v(110.92, -94.65) * mm, "mid": v(109.93, -96.6) * mm, "end": v(107.9, -97.38) * mm});
            skLineSegment(sketch, "E312.MirrorCS", {"start": v(95.4, -77.06) * mm, "end": v(97.12, -77.06) * mm});
            skArc(sketch, "E313.MirrorCS", {"start": v(98.22, -97.38) * mm, "mid": v(96.15, -96.57) * mm, "end": v(95.18, -94.56) * mm});
            skArc(sketch, "E314.MirrorCS", {"start": v(109.1, -77.06) * mm, "mid": v(111.56, -78.15) * mm, "end": v(112.4, -80.72) * mm});
            skArc(sketch, "E315.MirrorCS", {"start": v(94.08, -80.34) * mm, "mid": v(94.89, -78.04) * mm, "end": v(97.12, -77.06) * mm});
            skLineSegment(sketch, "E316.MirrorCS", {"start": v(110.64, -91.03) * mm, "end": v(110.64, -77.06) * mm});
            skLineSegment(sketch, "E317.MirrorCS", {"start": v(95.4, -91.03) * mm, "end": v(95.4, -77.06) * mm});
            skPoint(sketch, "E318.MirrorP", {"position": v(110.64, -97.38) * mm});
            skPoint(sketch, "E319.MirrorP", {"position": v(95.4, -97.38) * mm});
            skLineSegment(sketch, "E320.MirrorCS", {"start": v(101.75, -97.38) * mm, "end": v(104.29, -97.38) * mm});
            skLineSegment(sketch, "E321.MirrorCS", {"start": v(110.92, -94.65) * mm, "end": v(112.4, -80.72) * mm});
            skLineSegment(sketch, "E322.MirrorCS", {"start": v(95.18, -94.56) * mm, "end": v(94.08, -80.34) * mm});
            skLineSegment(sketch, "E323.MirrorCS", {"start": v(95.4, -77.06) * mm, "end": v(110.64, -77.06) * mm});
            skPoint(sketch, "E324.MirrorP", {"position": v(93.83, -77.06) * mm});
            skPoint(sketch, "E325.MirrorP", {"position": v(112.78, -77.06) * mm});
            skLineSegment(sketch, "E326.bottom", {"start": v(132.6, 238.72) * mm, "end": v(135.1, 238.28) * mm});
            skLineSegment(sketch, "E326.top", {"start": v(122.8, 219.81) * mm, "end": v(137.82, 217.17) * mm});
            skLineSegment(sketch, "E326.left", {"start": v(125.24, 233.57) * mm, "end": v(122.8, 219.81) * mm});
            skLineSegment(sketch, "E326.right", {"start": v(140.24, 230.92) * mm, "end": v(137.82, 217.17) * mm});
            skLineSegment(sketch, "E327", {"start": v(141.16, 234.44) * mm, "end": v(140.18, 220.29) * mm});
            skLineSegment(sketch, "E328", {"start": v(137.82, 217.17) * mm, "end": v(136.5, 217.4) * mm});
            skLineSegment(sketch, "E329", {"start": v(125.64, 237.1) * mm, "end": v(122.09, 223.27) * mm});
            skLineSegment(sketch, "E330", {"start": v(122.8, 219.81) * mm, "end": v(124.51, 219.51) * mm});
            skPoint(sketch, "E331.visualSharp", {"position": v(126.34, 239.82) * mm});
            skArc(sketch, "E331.filletArc", {"start": v(129.12, 239.33) * mm, "mid": v(126.94, 238.9) * mm, "end": v(125.64, 237.1) * mm});
            skPoint(sketch, "E332.visualSharp", {"position": v(141.35, 237.18) * mm});
            skArc(sketch, "E332.filletArc", {"start": v(141.16, 234.44) * mm, "mid": v(140.52, 236.53) * mm, "end": v(138.65, 237.65) * mm});
            skPoint(sketch, "E333.visualSharp", {"position": v(121.27, 220.08) * mm});
            skArc(sketch, "E333.filletArc", {"start": v(122.09, 223.27) * mm, "mid": v(122.48, 220.86) * mm, "end": v(124.51, 219.51) * mm});
            skPoint(sketch, "E334.visualSharp", {"position": v(139.94, 216.8) * mm});
            skArc(sketch, "E334.filletArc", {"start": v(136.5, 217.4) * mm, "mid": v(138.98, 218.02) * mm, "end": v(140.18, 220.29) * mm});
            skLineSegment(sketch, "E335.0", {"start": v(137.82, 217.17) * mm, "end": v(139.94, 216.8) * mm, "construction": true});
            skLineSegment(sketch, "E336.0", {"start": v(121.27, 220.08) * mm, "end": v(122.8, 219.81) * mm, "construction": true});
            skLineSegment(sketch, "E337", {"start": v(109.55, 71.67) * mm, "end": v(109.55, 223.62) * mm, "construction": true});
            skLineSegment(sketch, "E338", {"start": v(106.26, 71.67) * mm, "end": v(258.85, 71.72) * mm, "construction": true});
            skLineSegment(sketch, "E339", {"start": v(258.85, 71.72) * mm, "end": v(-45.82, 71.63) * mm, "construction": true});
            skLineSegment(sketch, "E340.bottom", {"start": v(162.06, 231.83) * mm, "end": v(164.49, 231.09) * mm});
            skLineSegment(sketch, "E340.top", {"start": v(150.04, 214.26) * mm, "end": v(164.61, 209.8) * mm});
            skLineSegment(sketch, "E340.left", {"start": v(154.13, 227.62) * mm, "end": v(150.04, 214.26) * mm});
            skLineSegment(sketch, "E340.right", {"start": v(168.7, 223.16) * mm, "end": v(164.61, 209.8) * mm});
            skLineSegment(sketch, "E341", {"start": v(170, 226.51) * mm, "end": v(166.9, 211.55) * mm});
            skLineSegment(sketch, "E342", {"start": v(164.61, 209.8) * mm, "end": v(164.17, 209.94) * mm});
            skLineSegment(sketch, "E343", {"start": v(154.96, 231.06) * mm, "end": v(149.75, 217.78) * mm});
            skLineSegment(sketch, "E344", {"start": v(150.04, 214.26) * mm, "end": v(151.7, 213.76) * mm});
            skPoint(sketch, "E345.visualSharp", {"position": v(155.99, 233.7) * mm});
            skArc(sketch, "E345.filletArc", {"start": v(158.69, 232.87) * mm, "mid": v(156.47, 232.7) * mm, "end": v(154.96, 231.06) * mm});
            skPoint(sketch, "E346.visualSharp", {"position": v(170.56, 229.23) * mm});
            skArc(sketch, "E346.filletArc", {"start": v(170, 226.51) * mm, "mid": v(169.64, 228.68) * mm, "end": v(167.9, 230.04) * mm});
            skPoint(sketch, "E347.visualSharp", {"position": v(148.55, 214.72) * mm});
            skArc(sketch, "E347.filletArc", {"start": v(149.75, 217.78) * mm, "mid": v(149.84, 215.34) * mm, "end": v(151.7, 213.76) * mm});
            skPoint(sketch, "E348.visualSharp", {"position": v(166.42, 209.25) * mm});
            skArc(sketch, "E348.filletArc", {"start": v(164.17, 209.94) * mm, "mid": v(165.89, 210.14) * mm, "end": v(166.9, 211.55) * mm});
            skLineSegment(sketch, "E349.0", {"start": v(164.61, 209.8) * mm, "end": v(166.42, 209.25) * mm, "construction": true});
            skLineSegment(sketch, "E350.0", {"start": v(148.55, 214.72) * mm, "end": v(150.04, 214.26) * mm, "construction": true});
            skLineSegment(sketch, "E351.bottom", {"start": v(192.96, 217.97) * mm, "end": v(195.26, 216.9) * mm});
            skLineSegment(sketch, "E351.top", {"start": v(178.62, 202.24) * mm, "end": v(192.43, 195.8) * mm});
            skLineSegment(sketch, "E351.left", {"start": v(184.52, 214.9) * mm, "end": v(178.62, 202.24) * mm});
            skLineSegment(sketch, "E351.right", {"start": v(198.33, 208.46) * mm, "end": v(192.43, 195.8) * mm});
            skLineSegment(sketch, "E352", {"start": v(200, 211.57) * mm, "end": v(194.17, 196.26) * mm});
            skLineSegment(sketch, "E353", {"start": v(192.71, 195.67) * mm, "end": v(192.43, 195.8) * mm});
            skLineSegment(sketch, "E354", {"start": v(185.82, 218.2) * mm, "end": v(178.82, 205.77) * mm});
            skLineSegment(sketch, "E355", {"start": v(178.62, 202.24) * mm, "end": v(180.18, 201.51) * mm});
            skPoint(sketch, "E356.visualSharp", {"position": v(187.2, 220.66) * mm});
            skArc(sketch, "E356.filletArc", {"start": v(189.76, 219.46) * mm, "mid": v(187.54, 219.6) * mm, "end": v(185.82, 218.2) * mm});
            skPoint(sketch, "E357.visualSharp", {"position": v(201.02, 214.22) * mm});
            skArc(sketch, "E357.filletArc", {"start": v(200, 211.57) * mm, "mid": v(199.98, 213.8) * mm, "end": v(198.45, 215.41) * mm});
            skPoint(sketch, "E358.visualSharp", {"position": v(177.2, 202.9) * mm});
            skArc(sketch, "E358.filletArc", {"start": v(178.82, 205.77) * mm, "mid": v(178.57, 203.34) * mm, "end": v(180.18, 201.51) * mm});
            skPoint(sketch, "E359.visualSharp", {"position": v(193.76, 195.18) * mm});
            skArc(sketch, "E359.filletArc", {"start": v(192.71, 195.67) * mm, "mid": v(193.57, 195.65) * mm, "end": v(194.17, 196.26) * mm});
            skLineSegment(sketch, "E360.0", {"start": v(177.2, 202.9) * mm, "end": v(178.62, 202.24) * mm, "construction": true});
            skLineSegment(sketch, "E361.0", {"start": v(192.43, 195.8) * mm, "end": v(193.76, 195.18) * mm, "construction": true});
            skLineSegment(sketch, "E362.bottom", {"start": v(219.8, 197.69) * mm, "end": v(221.74, 196.06) * mm});
            skLineSegment(sketch, "E362.top", {"start": v(201.87, 186.2) * mm, "end": v(213.54, 176.4) * mm});
            skLineSegment(sketch, "E362.left", {"start": v(210.85, 196.9) * mm, "end": v(201.87, 186.2) * mm});
            skLineSegment(sketch, "E362.right", {"start": v(222.52, 187.11) * mm, "end": v(213.54, 176.4) * mm});
            skLineSegment(sketch, "E363", {"start": v(225.05, 189.7) * mm, "end": v(216.45, 177.09) * mm});
            skLineSegment(sketch, "E364", {"start": v(213.54, 176.4) * mm, "end": v(213.26, 176.65) * mm});
            skLineSegment(sketch, "E365", {"start": v(212.96, 199.75) * mm, "end": v(202.97, 189.56) * mm});
            skLineSegment(sketch, "E366", {"start": v(201.87, 186.2) * mm, "end": v(203.2, 185.1) * mm});
            skPoint(sketch, "E367.visualSharp", {"position": v(214.93, 201.77) * mm});
            skArc(sketch, "E367.filletArc", {"start": v(217.1, 199.96) * mm, "mid": v(214.98, 200.67) * mm, "end": v(212.96, 199.75) * mm});
            skPoint(sketch, "E368.visualSharp", {"position": v(226.6, 191.98) * mm});
            skArc(sketch, "E368.filletArc", {"start": v(225.05, 189.7) * mm, "mid": v(225.55, 191.83) * mm, "end": v(224.5, 193.75) * mm});
            skPoint(sketch, "E369.visualSharp", {"position": v(200.67, 187.21) * mm});
            skArc(sketch, "E369.filletArc", {"start": v(202.97, 189.56) * mm, "mid": v(202.1, 187.28) * mm, "end": v(203.2, 185.1) * mm});
            skPoint(sketch, "E370.visualSharp", {"position": v(215.1, 175.1) * mm});
            skArc(sketch, "E370.filletArc", {"start": v(213.26, 176.65) * mm, "mid": v(214.95, 176.16) * mm, "end": v(216.45, 177.09) * mm});
            skLineSegment(sketch, "E371.0", {"start": v(200.67, 187.21) * mm, "end": v(201.87, 186.2) * mm, "construction": true});
            skLineSegment(sketch, "E372.0", {"start": v(213.54, 176.4) * mm, "end": v(215.1, 175.1) * mm, "construction": true});
            skLineSegment(sketch, "E373.bottom", {"start": v(242.18, 170.92) * mm, "end": v(243.44, 168.72) * mm});
            skLineSegment(sketch, "E373.top", {"start": v(221.4, 166.32) * mm, "end": v(228.97, 153.1) * mm});
            skLineSegment(sketch, "E373.left", {"start": v(233.51, 173.27) * mm, "end": v(221.4, 166.32) * mm});
            skLineSegment(sketch, "E373.right", {"start": v(241.09, 160.05) * mm, "end": v(228.97, 153.1) * mm});
            skLineSegment(sketch, "E374", {"start": v(244.34, 161.6) * mm, "end": v(234.31, 154.5) * mm});
            skLineSegment(sketch, "E375", {"start": v(228.97, 153.1) * mm, "end": v(227.28, 156.06) * mm});
            skLineSegment(sketch, "E376", {"start": v(236.47, 175.22) * mm, "end": v(223.59, 169.1) * mm});
            skLineSegment(sketch, "E377", {"start": v(221.4, 166.32) * mm, "end": v(222.25, 164.82) * mm});
            skPoint(sketch, "E378.visualSharp", {"position": v(239.02, 176.43) * mm});
            skArc(sketch, "E378.filletArc", {"start": v(240.42, 173.98) * mm, "mid": v(238.69, 175.37) * mm, "end": v(236.47, 175.22) * mm});
            skPoint(sketch, "E379.visualSharp", {"position": v(246.6, 163.2) * mm});
            skArc(sketch, "E379.filletArc", {"start": v(244.34, 161.6) * mm, "mid": v(245.55, 163.44) * mm, "end": v(245.22, 165.61) * mm});
            skPoint(sketch, "E380.visualSharp", {"position": v(220.61, 167.68) * mm});
            skArc(sketch, "E380.filletArc", {"start": v(223.59, 169.1) * mm, "mid": v(221.98, 167.25) * mm, "end": v(222.25, 164.82) * mm});
            skPoint(sketch, "E381.visualSharp", {"position": v(229.94, 151.41) * mm});
            skArc(sketch, "E381.filletArc", {"start": v(227.28, 156.06) * mm, "mid": v(230.45, 153.73) * mm, "end": v(234.31, 154.5) * mm});
            skLineSegment(sketch, "E382.0", {"start": v(220.61, 167.68) * mm, "end": v(221.4, 166.32) * mm, "construction": true});
            skLineSegment(sketch, "E383.0", {"start": v(228.97, 153.1) * mm, "end": v(229.94, 151.41) * mm, "construction": true});
            skLineSegment(sketch, "E384.bottom", {"start": v(259.15, 144.37) * mm, "end": v(260.22, 142.07) * mm});
            skLineSegment(sketch, "E384.top", {"start": v(238.05, 141.54) * mm, "end": v(244.49, 127.73) * mm});
            skLineSegment(sketch, "E384.left", {"start": v(250.7, 147.44) * mm, "end": v(238.05, 141.54) * mm});
            skLineSegment(sketch, "E384.right", {"start": v(257.15, 133.63) * mm, "end": v(244.49, 127.73) * mm});
            skLineSegment(sketch, "E385", {"start": v(260.55, 134.9) * mm, "end": v(248.2, 127.5) * mm});
            skLineSegment(sketch, "E386", {"start": v(244.49, 127.73) * mm, "end": v(244, 128.78) * mm});
            skLineSegment(sketch, "E387", {"start": v(253.82, 149.13) * mm, "end": v(240.47, 144.11) * mm});
            skLineSegment(sketch, "E388", {"start": v(238.05, 141.54) * mm, "end": v(238.78, 139.97) * mm});
            skPoint(sketch, "E389.visualSharp", {"position": v(256.46, 150.13) * mm});
            skArc(sketch, "E389.filletArc", {"start": v(257.66, 147.57) * mm, "mid": v(256.05, 149.1) * mm, "end": v(253.82, 149.13) * mm});
            skPoint(sketch, "E390.visualSharp", {"position": v(262.9, 136.31) * mm});
            skArc(sketch, "E390.filletArc", {"start": v(260.55, 134.9) * mm, "mid": v(261.9, 136.62) * mm, "end": v(261.74, 138.8) * mm});
            skPoint(sketch, "E391.visualSharp", {"position": v(237.39, 142.96) * mm});
            skArc(sketch, "E391.filletArc", {"start": v(240.47, 144.11) * mm, "mid": v(238.72, 142.41) * mm, "end": v(238.78, 139.97) * mm});
            skPoint(sketch, "E392.visualSharp", {"position": v(245.38, 125.81) * mm});
            skArc(sketch, "E392.filletArc", {"start": v(244, 128.78) * mm, "mid": v(245.8, 127.2) * mm, "end": v(248.2, 127.5) * mm});
            skLineSegment(sketch, "E393.0", {"start": v(237.39, 142.96) * mm, "end": v(238.05, 141.54) * mm, "construction": true});
            skLineSegment(sketch, "E394.0", {"start": v(244.49, 127.73) * mm, "end": v(245.38, 125.81) * mm, "construction": true});
            skLineSegment(sketch, "E395.bottom", {"start": v(270.07, 112.17) * mm, "end": v(270.51, 109.67) * mm});
            skLineSegment(sketch, "E395.top", {"start": v(248.96, 114.9) * mm, "end": v(251.6, 99.89) * mm});
            skLineSegment(sketch, "E395.left", {"start": v(262.72, 117.32) * mm, "end": v(248.96, 114.9) * mm});
            skLineSegment(sketch, "E395.right", {"start": v(265.36, 102.31) * mm, "end": v(251.6, 99.89) * mm});
            skLineSegment(sketch, "E396", {"start": v(269, 102.65) * mm, "end": v(256.32, 98.94) * mm});
            skLineSegment(sketch, "E397", {"start": v(251.6, 99.89) * mm, "end": v(251.21, 102.11) * mm});
            skLineSegment(sketch, "E398", {"start": v(266.16, 118.15) * mm, "end": v(251.96, 116.76) * mm});
            skLineSegment(sketch, "E399", {"start": v(248.96, 114.9) * mm, "end": v(249.26, 113.2) * mm});
            skPoint(sketch, "E400.visualSharp", {"position": v(268.97, 118.42) * mm});
            skArc(sketch, "E400.filletArc", {"start": v(269.46, 115.64) * mm, "mid": v(268.3, 117.54) * mm, "end": v(266.16, 118.15) * mm});
            skPoint(sketch, "E401.visualSharp", {"position": v(271.62, 103.41) * mm});
            skArc(sketch, "E401.filletArc", {"start": v(269, 102.65) * mm, "mid": v(270.73, 103.97) * mm, "end": v(271.14, 106.1) * mm});
            skPoint(sketch, "E402.visualSharp", {"position": v(248.69, 116.43) * mm});
            skArc(sketch, "E402.filletArc", {"start": v(251.96, 116.76) * mm, "mid": v(249.83, 115.57) * mm, "end": v(249.26, 113.2) * mm});
            skPoint(sketch, "E403.visualSharp", {"position": v(252, 97.67) * mm});
            skArc(sketch, "E403.filletArc", {"start": v(251.21, 102.11) * mm, "mid": v(253.06, 99.38) * mm, "end": v(256.32, 98.94) * mm});
            skLineSegment(sketch, "E404.0", {"start": v(248.69, 116.43) * mm, "end": v(248.96, 114.9) * mm, "construction": true});
            skLineSegment(sketch, "E405.0", {"start": v(251.6, 99.89) * mm, "end": v(252, 97.67) * mm, "construction": true});
            skLineSegment(sketch, "E406.bottom", {"start": v(275.15, 83.57) * mm, "end": v(275.28, 81.03) * mm});
            skLineSegment(sketch, "E406.top", {"start": v(254.55, 88.94) * mm, "end": v(255.28, 73.72) * mm});
            skLineSegment(sketch, "E406.left", {"start": v(268.5, 89.6) * mm, "end": v(254.55, 88.94) * mm});
            skLineSegment(sketch, "E406.right", {"start": v(269.24, 74.38) * mm, "end": v(255.28, 73.72) * mm});
            skLineSegment(sketch, "E407", {"start": v(272.86, 74.28) * mm, "end": v(258.67, 72.14) * mm});
            skLineSegment(sketch, "E408", {"start": v(255.28, 73.72) * mm, "end": v(255.22, 74.96) * mm});
            skLineSegment(sketch, "E409", {"start": v(272.03, 90) * mm, "end": v(257.77, 90.4) * mm});
            skLineSegment(sketch, "E410", {"start": v(254.55, 88.94) * mm, "end": v(254.64, 87.21) * mm});
            skPoint(sketch, "E411.visualSharp", {"position": v(274.85, 89.91) * mm});
            skArc(sketch, "E411.filletArc", {"start": v(274.99, 87.1) * mm, "mid": v(274.08, 89.12) * mm, "end": v(272.03, 90) * mm});
            skPoint(sketch, "E412.visualSharp", {"position": v(275.58, 74.69) * mm});
            skArc(sketch, "E412.filletArc", {"start": v(272.86, 74.28) * mm, "mid": v(274.76, 75.36) * mm, "end": v(275.45, 77.44) * mm});
            skPoint(sketch, "E413.visualSharp", {"position": v(254.48, 90.5) * mm});
            skArc(sketch, "E413.filletArc", {"start": v(257.77, 90.4) * mm, "mid": v(255.5, 89.5) * mm, "end": v(254.64, 87.21) * mm});
            skPoint(sketch, "E414.visualSharp", {"position": v(255.38, 71.64) * mm});
            skArc(sketch, "E414.filletArc", {"start": v(255.22, 74.96) * mm, "mid": v(256.32, 72.79) * mm, "end": v(258.67, 72.14) * mm});
            skLineSegment(sketch, "E415.0", {"start": v(255.28, 73.72) * mm, "end": v(255.38, 71.64) * mm, "construction": true});
            skLineSegment(sketch, "E416.0", {"start": v(254.48, 90.5) * mm, "end": v(254.55, 88.94) * mm, "construction": true});
            skLineSegment(sketch, "E417.MirrorCS", {"start": v(19.81, 195.62) * mm, "end": v(20.1, 195.75) * mm});
            skLineSegment(sketch, "E418.MirrorCS", {"start": v(20.1, 195.75) * mm, "end": v(18.77, 195.13) * mm, "construction": true});
            skLineSegment(sketch, "E419.MirrorCS", {"start": v(47.9, 209.77) * mm, "end": v(48.35, 209.9) * mm});
            skArc(sketch, "E420.MirrorCS", {"start": v(19.81, 195.62) * mm, "mid": v(18.96, 195.6) * mm, "end": v(18.36, 196.2) * mm});
            skLineSegment(sketch, "E421.MirrorCS", {"start": v(89.7, 219.8) * mm, "end": v(88, 219.5) * mm});
            skLineSegment(sketch, "E422.MirrorCS", {"start": v(47.9, 209.77) * mm, "end": v(46.1, 209.21) * mm, "construction": true});
            skLineSegment(sketch, "E423.MirrorCS", {"start": v(91.24, 220.08) * mm, "end": v(89.7, 219.8) * mm, "construction": true});
            skArc(sketch, "E424.MirrorCS", {"start": v(48.35, 209.9) * mm, "mid": v(46.63, 210.1) * mm, "end": v(45.62, 211.52) * mm});
            skLineSegment(sketch, "E425.MirrorCS", {"start": v(-36.38, 114.81) * mm, "end": v(-36.68, 113.1) * mm});
            skLineSegment(sketch, "E426.MirrorCS", {"start": v(33.9, 202.2) * mm, "end": v(32.34, 201.47) * mm});
            skArc(sketch, "E427.MirrorCS", {"start": v(90.42, 223.26) * mm, "mid": v(90.03, 220.85) * mm, "end": v(88, 219.5) * mm});
            skLineSegment(sketch, "E428.MirrorCS", {"start": v(-25.49, 141.46) * mm, "end": v(-26.22, 139.9) * mm});
            skLineSegment(sketch, "E429.MirrorCS", {"start": v(-8.84, 166.26) * mm, "end": v(-9.7, 164.76) * mm});
            skLineSegment(sketch, "E430.MirrorCS", {"start": v(-1, 176.35) * mm, "end": v(-0.72, 176.58) * mm});
            skLineSegment(sketch, "E431.MirrorCS", {"start": v(10.66, 186.15) * mm, "end": v(9.34, 185.04) * mm});
            skLineSegment(sketch, "E432.MirrorCS", {"start": v(74.7, 217.15) * mm, "end": v(76.02, 217.38) * mm});
            skLineSegment(sketch, "E433.MirrorCS", {"start": v(-39.02, 99.8) * mm, "end": v(-38.63, 102.03) * mm});
            skLineSegment(sketch, "E434.MirrorCS", {"start": v(-41.93, 89.53) * mm, "end": v(-42.01, 87.8) * mm});
            skLineSegment(sketch, "E435.MirrorCS", {"start": v(63.97, 214.7) * mm, "end": v(62.48, 214.24) * mm, "construction": true});
            skLineSegment(sketch, "E436.MirrorCS", {"start": v(-31.92, 127.65) * mm, "end": v(-31.43, 128.7) * mm});
            skArc(sketch, "E437.MirrorCS", {"start": v(-45.15, 91) * mm, "mid": v(-42.88, 90.08) * mm, "end": v(-42.01, 87.8) * mm});
            skArc(sketch, "E438.MirrorCS", {"start": v(9.56, 189.5) * mm, "mid": v(10.43, 187.22) * mm, "end": v(9.34, 185.04) * mm});
            skArc(sketch, "E439.MirrorCS", {"start": v(-0.72, 176.58) * mm, "mid": v(-2.42, 176.1) * mm, "end": v(-3.91, 177.02) * mm});
            skLineSegment(sketch, "E440.MirrorCS", {"start": v(62.48, 214.24) * mm, "end": v(60.82, 213.73) * mm});
            skLineSegment(sketch, "E441.MirrorCS", {"start": v(11.86, 187.15) * mm, "end": v(10.66, 186.15) * mm, "construction": true});
            skArc(sketch, "E442.MirrorCS", {"start": v(33.7, 205.73) * mm, "mid": v(33.95, 203.3) * mm, "end": v(32.34, 201.47) * mm});
            skLineSegment(sketch, "E443.MirrorCS", {"start": v(-1, 176.35) * mm, "end": v(-2.56, 175.04) * mm, "construction": true});
            skArc(sketch, "E444.MirrorCS", {"start": v(76.02, 217.38) * mm, "mid": v(73.53, 218) * mm, "end": v(72.33, 220.27) * mm});
            skLineSegment(sketch, "E445.MirrorCS", {"start": v(-42.65, 74.3) * mm, "end": v(-42.6, 75.55) * mm});
            skLineSegment(sketch, "E446.MirrorCS", {"start": v(35.32, 202.86) * mm, "end": v(33.9, 202.2) * mm, "construction": true});
            skLineSegment(sketch, "E447.MirrorCS", {"start": v(74.7, 217.15) * mm, "end": v(72.57, 216.77) * mm, "construction": true});
            skArc(sketch, "E448.MirrorCS", {"start": v(-39.39, 116.67) * mm, "mid": v(-37.26, 115.48) * mm, "end": v(-36.68, 113.1) * mm});
            skLineSegment(sketch, "E449.MirrorCS", {"start": v(-41.86, 91.09) * mm, "end": v(-41.93, 89.53) * mm, "construction": true});
            skLineSegment(sketch, "E450.MirrorCS", {"start": v(-39.02, 99.8) * mm, "end": v(-39.4, 97.58) * mm, "construction": true});
            skLineSegment(sketch, "E451.MirrorCS", {"start": v(-36.11, 116.35) * mm, "end": v(-36.38, 114.81) * mm, "construction": true});
            skArc(sketch, "E452.MirrorCS", {"start": v(-27.9, 144.04) * mm, "mid": v(-26.16, 142.34) * mm, "end": v(-26.22, 139.9) * mm});
            skLineSegment(sketch, "E453.MirrorCS", {"start": v(-24.83, 142.88) * mm, "end": v(-25.49, 141.46) * mm, "construction": true});
            skArc(sketch, "E454.MirrorCS", {"start": v(-11.04, 169.02) * mm, "mid": v(-9.44, 167.18) * mm, "end": v(-9.7, 164.76) * mm});
            skLineSegment(sketch, "E455.MirrorCS", {"start": v(-31.92, 127.65) * mm, "end": v(-32.81, 125.73) * mm, "construction": true});
            skLineSegment(sketch, "E456.MirrorCS", {"start": v(-8.07, 167.61) * mm, "end": v(-8.84, 166.26) * mm, "construction": true});
            skLineSegment(sketch, "E457.MirrorCS", {"start": v(-16.42, 153.03) * mm, "end": v(-14.72, 155.99) * mm});
            skArc(sketch, "E458.MirrorCS", {"start": v(-42.6, 75.55) * mm, "mid": v(-43.69, 73.37) * mm, "end": v(-46.04, 72.73) * mm});
            skLineSegment(sketch, "E459.MirrorCS", {"start": v(-42.65, 74.3) * mm, "end": v(-42.75, 72.23) * mm, "construction": true});
            skLineSegment(sketch, "E460.MirrorCS", {"start": v(-16.42, 153.03) * mm, "end": v(-17.39, 151.34) * mm, "construction": true});
            skArc(sketch, "E461.MirrorCS", {"start": v(-62.36, 87.67) * mm, "mid": v(-61.45, 89.7) * mm, "end": v(-59.4, 90.57) * mm});
            skArc(sketch, "E462.MirrorCS", {"start": v(22.75, 219.41) * mm, "mid": v(24.97, 219.56) * mm, "end": v(26.7, 218.15) * mm});
            skArc(sketch, "E463.MirrorCS", {"start": v(53.82, 232.83) * mm, "mid": v(56.04, 232.67) * mm, "end": v(57.55, 231.04) * mm});
            skArc(sketch, "E464.MirrorCS", {"start": v(-56.88, 115.55) * mm, "mid": v(-55.73, 117.45) * mm, "end": v(-53.59, 118.05) * mm});
            skArc(sketch, "E465.MirrorCS", {"start": v(-27.88, 173.9) * mm, "mid": v(-26.15, 175.3) * mm, "end": v(-23.93, 175.14) * mm});
            skArc(sketch, "E466.MirrorCS", {"start": v(-4.57, 199.9) * mm, "mid": v(-2.46, 200.6) * mm, "end": v(-0.43, 199.7) * mm});
            skArc(sketch, "E467.MirrorCS", {"start": v(-12.52, 189.63) * mm, "mid": v(-13.02, 191.76) * mm, "end": v(-11.96, 193.68) * mm});
            skLineSegment(sketch, "E468.MirrorCS", {"start": v(-7.27, 197.62) * mm, "end": v(-9.67, 195.6) * mm});
            skArc(sketch, "E469.MirrorCS", {"start": v(-60.23, 74.86) * mm, "mid": v(-62.13, 75.94) * mm, "end": v(-62.82, 78.02) * mm});
            skArc(sketch, "E470.MirrorCS", {"start": v(-31.43, 128.7) * mm, "mid": v(-33.24, 127.12) * mm, "end": v(-35.62, 127.41) * mm});
            skArc(sketch, "E471.MirrorCS", {"start": v(83.38, 239.32) * mm, "mid": v(85.57, 238.88) * mm, "end": v(86.87, 237.08) * mm});
            skArc(sketch, "E472.MirrorCS", {"start": v(71.35, 234.42) * mm, "mid": v(71.99, 236.5) * mm, "end": v(73.86, 237.63) * mm});
            skArc(sketch, "E473.MirrorCS", {"start": v(42.51, 226.47) * mm, "mid": v(42.87, 228.65) * mm, "end": v(44.6, 230) * mm});
            skArc(sketch, "E474.MirrorCS", {"start": v(62.77, 217.76) * mm, "mid": v(62.68, 215.32) * mm, "end": v(60.82, 213.73) * mm});
            skLineSegment(sketch, "E475.MirrorCS", {"start": v(19.55, 217.92) * mm, "end": v(17.25, 216.85) * mm});
            skArc(sketch, "E476.MirrorCS", {"start": v(-56.41, 102.55) * mm, "mid": v(-58.15, 103.87) * mm, "end": v(-58.56, 106) * mm});
            skArc(sketch, "E477.MirrorCS", {"start": v(-45.1, 147.48) * mm, "mid": v(-43.5, 149.01) * mm, "end": v(-41.27, 149.05) * mm});
            skArc(sketch, "E478.MirrorCS", {"start": v(-38.63, 102.03) * mm, "mid": v(-40.47, 99.3) * mm, "end": v(-43.74, 98.85) * mm});
            skArc(sketch, "E479.MirrorCS", {"start": v(-47.98, 134.81) * mm, "mid": v(-49.33, 136.53) * mm, "end": v(-49.18, 138.71) * mm});
            skArc(sketch, "E480.MirrorCS", {"start": v(-31.79, 161.53) * mm, "mid": v(-33, 163.36) * mm, "end": v(-32.68, 165.53) * mm});
            skArc(sketch, "E481.MirrorCS", {"start": v(-14.72, 155.99) * mm, "mid": v(-17.9, 153.65) * mm, "end": v(-21.76, 154.43) * mm});
            skArc(sketch, "E482.MirrorCS", {"start": v(12.51, 211.51) * mm, "mid": v(12.53, 213.74) * mm, "end": v(14.07, 215.36) * mm});
            skLineSegment(sketch, "E483.MirrorCS", {"start": v(-46.59, 144.28) * mm, "end": v(-47.93, 141.41) * mm});
            skLineSegment(sketch, "E484.MirrorCS", {"start": v(-29.63, 170.84) * mm, "end": v(-30.9, 168.64) * mm});
            skLineSegment(sketch, "E485.MirrorCS", {"start": v(50.45, 231.8) * mm, "end": v(48.02, 231.06) * mm});
            skLineSegment(sketch, "E486.MirrorCS", {"start": v(-23.93, 175.14) * mm, "end": v(-11.04, 169.02) * mm});
            skLineSegment(sketch, "E487.MirrorCS", {"start": v(-0.43, 199.7) * mm, "end": v(9.56, 189.5) * mm});
            skLineSegment(sketch, "E488.MirrorCS", {"start": v(-45.43, 133.28) * mm, "end": v(-35.62, 127.41) * mm});
            skLineSegment(sketch, "E489.MirrorCS", {"start": v(-20.97, 173.2) * mm, "end": v(-8.84, 166.26) * mm});
            skPoint(sketch, "E490.MirrorP", {"position": v(-32.81, 125.73) * mm});
            skPoint(sketch, "E491.MirrorP", {"position": v(-42.75, 72.23) * mm});
            skPoint(sketch, "E492.MirrorP", {"position": v(46.1, 209.21) * mm});
            skPoint(sketch, "E493.MirrorP", {"position": v(-2.56, 175.04) * mm});
            skLineSegment(sketch, "E494.MirrorCS", {"start": v(-50.34, 136.22) * mm, "end": v(-31.92, 127.65) * mm});
            skLineSegment(sketch, "E495.MirrorCS", {"start": v(-8.84, 166.26) * mm, "end": v(-16.42, 153.03) * mm});
            skLineSegment(sketch, "E496.MirrorCS", {"start": v(-28.54, 159.97) * mm, "end": v(-16.42, 153.03) * mm});
            skLineSegment(sketch, "E497.MirrorCS", {"start": v(10.66, 186.15) * mm, "end": v(-1, 176.35) * mm});
            skPoint(sketch, "E498.MirrorP", {"position": v(-26.48, 176.35) * mm});
            skLineSegment(sketch, "E499.MirrorCS", {"start": v(79.91, 238.7) * mm, "end": v(77.4, 238.26) * mm});
            skLineSegment(sketch, "E500.MirrorCS", {"start": v(-31.79, 161.53) * mm, "end": v(-21.76, 154.43) * mm});
            skLineSegment(sketch, "E501.MirrorCS", {"start": v(-41.27, 149.05) * mm, "end": v(-27.9, 144.04) * mm});
            skLineSegment(sketch, "E502.MirrorCS", {"start": v(1.68, 196.85) * mm, "end": v(10.66, 186.15) * mm});
            skLineSegment(sketch, "E503.MirrorCS", {"start": v(33.9, 202.2) * mm, "end": v(20.1, 195.75) * mm});
            skLineSegment(sketch, "E504.MirrorCS", {"start": v(89.7, 219.8) * mm, "end": v(74.7, 217.15) * mm});
            skLineSegment(sketch, "E505.MirrorCS", {"start": v(28, 214.86) * mm, "end": v(33.9, 202.2) * mm});
            skLineSegment(sketch, "E506.MirrorCS", {"start": v(42.51, 226.47) * mm, "end": v(45.62, 211.52) * mm});
            skLineSegment(sketch, "E507.MirrorCS", {"start": v(86.87, 237.08) * mm, "end": v(90.42, 223.26) * mm});
            skLineSegment(sketch, "E508.MirrorCS", {"start": v(-41.93, 89.53) * mm, "end": v(-42.65, 74.3) * mm});
            skLineSegment(sketch, "E509.MirrorCS", {"start": v(57.55, 231.04) * mm, "end": v(62.77, 217.76) * mm});
            skLineSegment(sketch, "E510.MirrorCS", {"start": v(-55.88, 90.19) * mm, "end": v(-41.93, 89.53) * mm});
            skLineSegment(sketch, "E511.MirrorCS", {"start": v(-57.5, 112.07) * mm, "end": v(-58.05, 108.92) * mm});
            skPoint(sketch, "E512.MirrorP", {"position": v(-2.4, 201.7) * mm});
            skPoint(sketch, "E513.MirrorP", {"position": v(56.52, 233.66) * mm});
            skPoint(sketch, "E514.MirrorP", {"position": v(-43.9, 150.04) * mm});
            skLineSegment(sketch, "E515.MirrorCS", {"start": v(-36.38, 114.81) * mm, "end": v(-39.02, 99.8) * mm});
            skLineSegment(sketch, "E516.MirrorCS", {"start": v(-50.14, 117.23) * mm, "end": v(-36.38, 114.81) * mm});
            skPoint(sketch, "E517.MirrorP", {"position": v(-14.07, 191.9) * mm});
            skPoint(sketch, "E518.MirrorP", {"position": v(41.95, 229.2) * mm});
            skPoint(sketch, "E519.MirrorP", {"position": v(-50.34, 136.22) * mm});
            skPoint(sketch, "E520.MirrorP", {"position": v(-62.95, 75.27) * mm});
            skLineSegment(sketch, "E521.MirrorCS", {"start": v(-59.03, 103.32) * mm, "end": v(-39.02, 99.8) * mm});
            skLineSegment(sketch, "E522.MirrorCS", {"start": v(-25.49, 141.46) * mm, "end": v(-31.92, 127.65) * mm});
            skPoint(sketch, "E523.MirrorP", {"position": v(11.86, 187.15) * mm});
            skPoint(sketch, "E524.MirrorP", {"position": v(63.97, 214.7) * mm});
            skPoint(sketch, "E525.MirrorP", {"position": v(-41.86, 91.09) * mm});
            skPoint(sketch, "E526.MirrorP", {"position": v(-24.83, 142.88) * mm});
            skLineSegment(sketch, "E527.MirrorCS", {"start": v(-59.4, 90.57) * mm, "end": v(-45.15, 91) * mm});
            skLineSegment(sketch, "E528.MirrorCS", {"start": v(-53.58, 101.72) * mm, "end": v(-43.74, 98.85) * mm});
            skLineSegment(sketch, "E529.MirrorCS", {"start": v(-38.15, 147.36) * mm, "end": v(-25.49, 141.46) * mm});
            skPoint(sketch, "E530.MirrorP", {"position": v(86.16, 239.81) * mm});
            skPoint(sketch, "E531.MirrorP", {"position": v(-56.4, 118.33) * mm});
            skLineSegment(sketch, "E532.MirrorCS", {"start": v(-53.59, 118.05) * mm, "end": v(-39.39, 116.67) * mm});
            skPoint(sketch, "E533.MirrorP", {"position": v(25.3, 220.6) * mm});
            skLineSegment(sketch, "E534.MirrorCS", {"start": v(-14.07, 191.9) * mm, "end": v(-1, 176.35) * mm});
            skPoint(sketch, "E535.MirrorP", {"position": v(71.16, 237.16) * mm});
            skPoint(sketch, "E536.MirrorP", {"position": v(-59.03, 103.32) * mm});
            skPoint(sketch, "E537.MirrorP", {"position": v(-34.05, 163.13) * mm});
            skPoint(sketch, "E538.MirrorP", {"position": v(11.5, 214.16) * mm});
            skLineSegment(sketch, "E539.MirrorCS", {"start": v(87.27, 233.56) * mm, "end": v(89.7, 219.8) * mm});
            skLineSegment(sketch, "E540.MirrorCS", {"start": v(-10.83, 187.16) * mm, "end": v(-3.91, 177.02) * mm});
            skLineSegment(sketch, "E541.MirrorCS", {"start": v(14.19, 208.4) * mm, "end": v(20.1, 195.75) * mm});
            skLineSegment(sketch, "E542.MirrorCS", {"start": v(62.48, 214.24) * mm, "end": v(47.9, 209.77) * mm});
            skLineSegment(sketch, "E543.MirrorCS", {"start": v(72.26, 230.9) * mm, "end": v(74.7, 217.15) * mm});
            skLineSegment(sketch, "E544.MirrorCS", {"start": v(43.8, 223.12) * mm, "end": v(47.9, 209.77) * mm});
            skPoint(sketch, "E545.MirrorP", {"position": v(-36.11, 116.35) * mm});
            skPoint(sketch, "E546.MirrorP", {"position": v(-8.07, 167.61) * mm});
            skPoint(sketch, "E547.MirrorP", {"position": v(35.32, 202.86) * mm});
            skLineSegment(sketch, "E548.MirrorCS", {"start": v(12.51, 211.51) * mm, "end": v(18.36, 196.2) * mm});
            skLineSegment(sketch, "E549.MirrorCS", {"start": v(58.38, 227.6) * mm, "end": v(62.48, 214.24) * mm});
            skLineSegment(sketch, "E550.MirrorCS", {"start": v(71.35, 234.42) * mm, "end": v(72.33, 220.27) * mm});
            skPoint(sketch, "E551.MirrorP", {"position": v(18.77, 195.13) * mm});
            skPoint(sketch, "E552.MirrorP", {"position": v(72.57, 216.77) * mm});
            skPoint(sketch, "E553.MirrorP", {"position": v(-39.4, 97.58) * mm});
            skPoint(sketch, "E554.MirrorP", {"position": v(-17.39, 151.34) * mm});
            skLineSegment(sketch, "E555.MirrorCS", {"start": v(26.7, 218.15) * mm, "end": v(33.7, 205.73) * mm});
            skLineSegment(sketch, "E556.MirrorCS", {"start": v(-62.53, 84.15) * mm, "end": v(-62.65, 81.6) * mm});
            skPoint(sketch, "E557.MirrorP", {"position": v(91.24, 220.08) * mm});
            skPoint(sketch, "E558.MirrorP", {"position": v(-62.23, 90.49) * mm});
            skLineSegment(sketch, "E559.MirrorCS", {"start": v(-56.6, 74.97) * mm, "end": v(-42.65, 74.3) * mm});
            skLineSegment(sketch, "E560.MirrorCS", {"start": v(-60.23, 74.86) * mm, "end": v(-46.04, 72.73) * mm});
            skLineSegment(sketch, "E561.MirrorCS", {"start": v(44.18, -65.2) * mm, "end": v(44.63, -65.33) * mm});
            skLineSegment(sketch, "E562.MirrorCS", {"start": v(-0.94, -33.07) * mm, "end": v(-0.66, -33.3) * mm});
            skArc(sketch, "E563.MirrorCS", {"start": v(44.63, -65.33) * mm, "mid": v(42.9, -65.53) * mm, "end": v(41.9, -66.94) * mm});
            skLineSegment(sketch, "E564.MirrorCS", {"start": v(-35.34, 23.11) * mm, "end": v(-35.64, 24.81) * mm});
            skLineSegment(sketch, "E565.MirrorCS", {"start": v(44.18, -65.2) * mm, "end": v(42.37, -64.64) * mm, "construction": true});
            skLineSegment(sketch, "E566.MirrorCS", {"start": v(84.97, -75.46) * mm, "end": v(83.26, -75.16) * mm});
            skArc(sketch, "E567.MirrorCS", {"start": v(-38.35, 21.25) * mm, "mid": v(-36.22, 22.44) * mm, "end": v(-35.64, 24.81) * mm});
            skLineSegment(sketch, "E568.MirrorCS", {"start": v(10.73, -42.86) * mm, "end": v(9.4, -41.75) * mm});
            skLineSegment(sketch, "E569.MirrorCS", {"start": v(34.94, -60.8) * mm, "end": v(33.63, -59.96) * mm, "construction": true});
            skLineSegment(sketch, "E570.MirrorCS", {"start": v(-16.37, -11.13) * mm, "end": v(-17.34, -9.44) * mm, "construction": true});
            skLineSegment(sketch, "E571.MirrorCS", {"start": v(-35.07, 21.57) * mm, "end": v(-35.34, 23.11) * mm, "construction": true});
            skLineSegment(sketch, "E572.MirrorCS", {"start": v(86.5, -75.73) * mm, "end": v(84.97, -75.46) * mm, "construction": true});
            skLineSegment(sketch, "E573.MirrorCS", {"start": v(-0.94, -33.07) * mm, "end": v(-2.5, -31.76) * mm, "construction": true});
            skArc(sketch, "E574.MirrorCS", {"start": v(85.69, -78.92) * mm, "mid": v(85.3, -76.5) * mm, "end": v(83.26, -75.16) * mm});
            skLineSegment(sketch, "E575.MirrorCS", {"start": v(33.63, -59.96) * mm, "end": v(32.18, -59.02) * mm});
            skLineSegment(sketch, "E576.MirrorCS", {"start": v(11.93, -43.87) * mm, "end": v(10.73, -42.86) * mm, "construction": true});
            skArc(sketch, "E577.MirrorCS", {"start": v(-0.66, -33.3) * mm, "mid": v(-2.35, -32.82) * mm, "end": v(-3.85, -33.75) * mm});
            skLineSegment(sketch, "E578.MirrorCS", {"start": v(-31.63, 13.33) * mm, "end": v(-32.53, 15.24) * mm, "construction": true});
            skLineSegment(sketch, "E579.MirrorCS", {"start": v(-24.53, -1.9) * mm, "end": v(-25.2, -0.49) * mm, "construction": true});
            skLineSegment(sketch, "E580.MirrorCS", {"start": v(-25.2, -0.49) * mm, "end": v(-25.92, 1.08) * mm});
            skLineSegment(sketch, "E581.MirrorCS", {"start": v(-31.63, 13.33) * mm, "end": v(-31.14, 12.27) * mm});
            skArc(sketch, "E582.MirrorCS", {"start": v(-27.61, -3.06) * mm, "mid": v(-25.86, -1.36) * mm, "end": v(-25.92, 1.08) * mm});
            skLineSegment(sketch, "E583.MirrorCS", {"start": v(20.83, -51.68) * mm, "end": v(19.6, -50.89) * mm, "construction": true});
            skLineSegment(sketch, "E584.MirrorCS", {"start": v(-37.99, 38.12) * mm, "end": v(-38.38, 40.34) * mm, "construction": true});
            skLineSegment(sketch, "E585.MirrorCS", {"start": v(20.57, -51.51) * mm, "end": v(20.83, -51.68) * mm});
            skLineSegment(sketch, "E586.MirrorCS", {"start": v(-37.99, 38.12) * mm, "end": v(-37.6, 35.9) * mm});
            skLineSegment(sketch, "E587.MirrorCS", {"start": v(69.96, -72.8) * mm, "end": v(71.28, -73.04) * mm});
            skLineSegment(sketch, "E588.MirrorCS", {"start": v(69.96, -72.8) * mm, "end": v(67.83, -72.44) * mm, "construction": true});
            skLineSegment(sketch, "E589.MirrorCS", {"start": v(-8.79, -24.36) * mm, "end": v(-9.65, -22.86) * mm});
            skLineSegment(sketch, "E590.MirrorCS", {"start": v(-8.01, -25.71) * mm, "end": v(-8.79, -24.36) * mm, "construction": true});
            skLineSegment(sketch, "E591.MirrorCS", {"start": v(58.75, -69.65) * mm, "end": v(57.1, -69.15) * mm});
            skArc(sketch, "E592.MirrorCS", {"start": v(-10.98, -27.12) * mm, "mid": v(-9.38, -25.28) * mm, "end": v(-9.65, -22.86) * mm});
            skLineSegment(sketch, "E593.MirrorCS", {"start": v(60.24, -70.1) * mm, "end": v(58.75, -69.65) * mm, "construction": true});
            skArc(sketch, "E594.MirrorCS", {"start": v(20.57, -51.51) * mm, "mid": v(19.72, -51.37) * mm, "end": v(19.04, -51.9) * mm});
            skLineSegment(sketch, "E595.MirrorCS", {"start": v(-16.37, -11.13) * mm, "end": v(-14.67, -14.09) * mm});
            skArc(sketch, "E596.MirrorCS", {"start": v(11.16, -66.26) * mm, "mid": v(10.88, -68.48) * mm, "end": v(12.18, -70.29) * mm});
            skArc(sketch, "E597.MirrorCS", {"start": v(-4.5, -56.62) * mm, "mid": v(-2.38, -57.33) * mm, "end": v(-0.35, -56.41) * mm});
            skArc(sketch, "E598.MirrorCS", {"start": v(-14.67, -14.09) * mm, "mid": v(-17.85, -11.76) * mm, "end": v(-21.7, -12.54) * mm});
            skArc(sketch, "E599.MirrorCS", {"start": v(-27.82, -32.01) * mm, "mid": v(-26.09, -33.4) * mm, "end": v(-23.87, -33.25) * mm});
            skArc(sketch, "E600.MirrorCS", {"start": v(-31.74, -19.64) * mm, "mid": v(-32.95, -21.47) * mm, "end": v(-32.62, -23.64) * mm});
            skArc(sketch, "E601.MirrorCS", {"start": v(-55.84, 22.36) * mm, "mid": v(-54.68, 20.46) * mm, "end": v(-52.54, 19.86) * mm});
            skArc(sketch, "E602.MirrorCS", {"start": v(-47.7, 6.15) * mm, "mid": v(-49.04, 4.43) * mm, "end": v(-48.89, 2.25) * mm});
            skArc(sketch, "E603.MirrorCS", {"start": v(50.1, -88.26) * mm, "mid": v(52.32, -88.09) * mm, "end": v(53.83, -86.45) * mm});
            skArc(sketch, "E604.MirrorCS", {"start": v(-37.6, 35.9) * mm, "mid": v(-39.44, 38.62) * mm, "end": v(-42.7, 39.07) * mm});
            skArc(sketch, "E605.MirrorCS", {"start": v(20.22, -75.5) * mm, "mid": v(22.4, -75.93) * mm, "end": v(24.3, -74.78) * mm});
            skArc(sketch, "E606.MirrorCS", {"start": v(-44.8, -6.51) * mm, "mid": v(-43.2, -8.05) * mm, "end": v(-40.97, -8.08) * mm});
            skArc(sketch, "E607.MirrorCS", {"start": v(71.28, -73.04) * mm, "mid": v(68.8, -73.67) * mm, "end": v(67.6, -75.93) * mm});
            skArc(sketch, "E608.MirrorCS", {"start": v(66.62, -90.09) * mm, "mid": v(67.26, -92.17) * mm, "end": v(69.13, -93.3) * mm});
            skArc(sketch, "E609.MirrorCS", {"start": v(-12.45, -46.36) * mm, "mid": v(-12.95, -48.49) * mm, "end": v(-11.9, -50.4) * mm});
            skArc(sketch, "E610.MirrorCS", {"start": v(78.66, -94.98) * mm, "mid": v(80.84, -94.54) * mm, "end": v(82.14, -92.73) * mm});
            skArc(sketch, "E611.MirrorCS", {"start": v(9.63, -46.22) * mm, "mid": v(10.5, -43.94) * mm, "end": v(9.4, -41.75) * mm});
            skArc(sketch, "E612.MirrorCS", {"start": v(-31.14, 12.27) * mm, "mid": v(-32.95, 13.85) * mm, "end": v(-35.34, 13.56) * mm});
            skArc(sketch, "E613.MirrorCS", {"start": v(32.95, -63.43) * mm, "mid": v(33.52, -61.06) * mm, "end": v(32.18, -59.02) * mm});
            skArc(sketch, "E614.MirrorCS", {"start": v(59.04, -73.17) * mm, "mid": v(58.95, -70.73) * mm, "end": v(57.1, -69.15) * mm});
            skArc(sketch, "E615.MirrorCS", {"start": v(38.8, -81.9) * mm, "mid": v(39.16, -84.07) * mm, "end": v(40.89, -85.43) * mm});
            skArc(sketch, "E616.MirrorCS", {"start": v(-55.38, 35.36) * mm, "mid": v(-57.11, 34.04) * mm, "end": v(-57.52, 31.9) * mm});
            skLineSegment(sketch, "E617.MirrorCS", {"start": v(33.63, -59.96) * mm, "end": v(20.83, -51.68) * mm});
            skPoint(sketch, "E618.MirrorP", {"position": v(52.8, -89.08) * mm});
            skLineSegment(sketch, "E619.MirrorCS", {"start": v(-52.54, 19.86) * mm, "end": v(-38.35, 21.25) * mm});
            skPoint(sketch, "E620.MirrorP", {"position": v(9.8, -68.75) * mm});
            skLineSegment(sketch, "E621.MirrorCS", {"start": v(1.75, -53.57) * mm, "end": v(10.73, -42.86) * mm});
            skPoint(sketch, "E622.MirrorP", {"position": v(-2.33, -58.43) * mm});
            skLineSegment(sketch, "E623.MirrorCS", {"start": v(-37.85, -6.39) * mm, "end": v(-25.2, -0.49) * mm});
            skPoint(sketch, "E624.MirrorP", {"position": v(-34, -21.24) * mm});
            skPoint(sketch, "E625.MirrorP", {"position": v(-26.42, -34.46) * mm});
            skLineSegment(sketch, "E626.MirrorCS", {"start": v(-40.97, -8.08) * mm, "end": v(-27.61, -3.06) * mm});
            skPoint(sketch, "E627.MirrorP", {"position": v(-58, 34.6) * mm});
            skLineSegment(sketch, "E628.MirrorCS", {"start": v(-55.38, 35.36) * mm, "end": v(-42.7, 39.07) * mm});
            skPoint(sketch, "E629.MirrorP", {"position": v(-2.5, -31.76) * mm});
            skLineSegment(sketch, "E630.MirrorCS", {"start": v(-31.74, -19.64) * mm, "end": v(-21.7, -12.54) * mm});
            skPoint(sketch, "E631.MirrorP", {"position": v(66.43, -92.82) * mm});
            skPoint(sketch, "E632.MirrorP", {"position": v(42.37, -64.64) * mm});
            skLineSegment(sketch, "E633.MirrorCS", {"start": v(75.18, -94.36) * mm, "end": v(72.68, -93.92) * mm});
            skPoint(sketch, "E634.MirrorP", {"position": v(22.6, -77.02) * mm});
            skLineSegment(sketch, "E635.MirrorCS", {"start": v(-25.2, -0.49) * mm, "end": v(-31.63, 13.33) * mm});
            skLineSegment(sketch, "E636.MirrorCS", {"start": v(10.73, -42.86) * mm, "end": v(-0.94, -33.07) * mm});
            skPoint(sketch, "E637.MirrorP", {"position": v(-55.35, 19.58) * mm});
            skLineSegment(sketch, "E638.MirrorCS", {"start": v(-51.75, 35.7) * mm, "end": v(-37.99, 38.12) * mm});
            skLineSegment(sketch, "E639.MirrorCS", {"start": v(24.3, -74.78) * mm, "end": v(32.95, -63.43) * mm});
            skLineSegment(sketch, "E640.MirrorCS", {"start": v(-49.1, 20.69) * mm, "end": v(-35.34, 23.11) * mm});
            skPoint(sketch, "E641.MirrorP", {"position": v(81.44, -95.47) * mm});
            skLineSegment(sketch, "E642.MirrorCS", {"start": v(66.62, -90.09) * mm, "end": v(67.6, -75.93) * mm});
            skLineSegment(sketch, "E643.MirrorCS", {"start": v(-9.92, -43.77) * mm, "end": v(-0.94, -33.07) * mm});
            skPoint(sketch, "E644.MirrorP", {"position": v(-35.07, 21.57) * mm});
            skPoint(sketch, "E645.MirrorP", {"position": v(-43.6, -9.07) * mm});
            skLineSegment(sketch, "E646.MirrorCS", {"start": v(84.97, -75.46) * mm, "end": v(69.96, -72.8) * mm});
            skLineSegment(sketch, "E647.MirrorCS", {"start": v(-47.7, 6.15) * mm, "end": v(-35.34, 13.56) * mm});
            skLineSegment(sketch, "E648.MirrorCS", {"start": v(-46.3, -3.32) * mm, "end": v(-47.37, -1.02) * mm});
            skPoint(sketch, "E649.MirrorP", {"position": v(-38.38, 40.34) * mm});
            skLineSegment(sketch, "E650.MirrorCS", {"start": v(67.53, -86.57) * mm, "end": v(69.96, -72.8) * mm});
            skPoint(sketch, "E651.MirrorP", {"position": v(11.93, -43.87) * mm});
            skLineSegment(sketch, "E652.MirrorCS", {"start": v(53.83, -86.45) * mm, "end": v(59.04, -73.17) * mm});
            skLineSegment(sketch, "E653.MirrorCS", {"start": v(-0.35, -56.41) * mm, "end": v(9.63, -46.22) * mm});
            skPoint(sketch, "E654.MirrorP", {"position": v(19.6, -50.89) * mm});
            skLineSegment(sketch, "E655.MirrorCS", {"start": v(82.14, -92.73) * mm, "end": v(85.69, -78.92) * mm});
            skLineSegment(sketch, "E656.MirrorCS", {"start": v(13.24, -63.42) * mm, "end": v(20.83, -51.68) * mm});
            skLineSegment(sketch, "E657.MirrorCS", {"start": v(-44.3, 7.42) * mm, "end": v(-31.63, 13.33) * mm});
            skPoint(sketch, "E658.MirrorP", {"position": v(86.5, -75.73) * mm});
            skPoint(sketch, "E659.MirrorP", {"position": v(60.24, -70.1) * mm});
            skPoint(sketch, "E660.MirrorP", {"position": v(-17.34, -9.44) * mm});
            skLineSegment(sketch, "E661.MirrorCS", {"start": v(40.09, -78.55) * mm, "end": v(44.18, -65.2) * mm});
            skLineSegment(sketch, "E662.MirrorCS", {"start": v(-20.9, -31.3) * mm, "end": v(-8.79, -24.36) * mm});
            skPoint(sketch, "E663.MirrorP", {"position": v(67.83, -72.44) * mm});
            skLineSegment(sketch, "E664.MirrorCS", {"start": v(58.75, -69.65) * mm, "end": v(44.18, -65.2) * mm});
            skPoint(sketch, "E665.MirrorP", {"position": v(-50.05, 4.74) * mm});
            skLineSegment(sketch, "E666.MirrorCS", {"start": v(-23.87, -33.25) * mm, "end": v(-10.98, -27.12) * mm});
            skPoint(sketch, "E667.MirrorP", {"position": v(38.23, -84.62) * mm});
            skLineSegment(sketch, "E668.MirrorCS", {"start": v(38.8, -81.9) * mm, "end": v(41.9, -66.94) * mm});
            skLineSegment(sketch, "E669.MirrorCS", {"start": v(-12.45, -46.36) * mm, "end": v(-3.85, -33.75) * mm});
            skPoint(sketch, "E670.MirrorP", {"position": v(34.94, -60.8) * mm});
            skLineSegment(sketch, "E671.MirrorCS", {"start": v(46.73, -87.22) * mm, "end": v(44.3, -86.48) * mm});
            skPoint(sketch, "E672.MirrorP", {"position": v(-32.53, 15.24) * mm});
            skLineSegment(sketch, "E673.MirrorCS", {"start": v(-28.49, -18.08) * mm, "end": v(-16.37, -11.13) * mm});
            skPoint(sketch, "E674.MirrorP", {"position": v(-14, -48.63) * mm});
            skLineSegment(sketch, "E675.MirrorCS", {"start": v(26.04, -71.7) * mm, "end": v(33.63, -59.96) * mm});
            skLineSegment(sketch, "E676.MirrorCS", {"start": v(82.54, -89.21) * mm, "end": v(84.97, -75.46) * mm});
            skPoint(sketch, "E677.MirrorP", {"position": v(-8.01, -25.71) * mm});
            skLineSegment(sketch, "E678.MirrorCS", {"start": v(-7.2, -54.35) * mm, "end": v(-9.14, -52.72) * mm});
            skLineSegment(sketch, "E679.MirrorCS", {"start": v(-29.58, -28.95) * mm, "end": v(-30.84, -26.75) * mm});
            skPoint(sketch, "E680.MirrorP", {"position": v(-24.53, -1.9) * mm});
            skLineSegment(sketch, "E681.MirrorCS", {"start": v(-35.34, 23.11) * mm, "end": v(-37.99, 38.12) * mm});
            skLineSegment(sketch, "E682.MirrorCS", {"start": v(54.66, -83) * mm, "end": v(58.75, -69.65) * mm});
            skLineSegment(sketch, "E683.MirrorCS", {"start": v(17.26, -73.58) * mm, "end": v(15.13, -72.2) * mm});
            skLineSegment(sketch, "E684.MirrorCS", {"start": v(-8.79, -24.36) * mm, "end": v(-16.37, -11.13) * mm});
            skLineSegment(sketch, "E685.MirrorCS", {"start": v(-56.46, 25.84) * mm, "end": v(-56.9, 28.34) * mm});
            skLineSegment(sketch, "E686.MirrorCS", {"start": v(11.16, -66.26) * mm, "end": v(19.04, -51.9) * mm});
            skLineSegment(sketch, "E687.MirrorCS", {"start": v(190.25, -54.05) * mm, "end": v(189.96, -54.19) * mm});
            skLineSegment(sketch, "E688.MirrorCS", {"start": v(211.83, -34.78) * mm, "end": v(211.55, -35.02) * mm});
            skArc(sketch, "E689.MirrorCS", {"start": v(211.55, -35.02) * mm, "mid": v(213.24, -34.53) * mm, "end": v(214.74, -35.46) * mm});
            skLineSegment(sketch, "E690.MirrorCS", {"start": v(211.83, -34.78) * mm, "end": v(213.38, -33.48) * mm, "construction": true});
            skLineSegment(sketch, "E691.MirrorCS", {"start": v(137.9, -73.8) * mm, "end": v(136.58, -74.04) * mm});
            skLineSegment(sketch, "E692.MirrorCS", {"start": v(164.7, -66.43) * mm, "end": v(164.25, -66.56) * mm});
            skLineSegment(sketch, "E693.MirrorCS", {"start": v(189.96, -54.19) * mm, "end": v(191.3, -53.57) * mm, "construction": true});
            skArc(sketch, "E694.MirrorCS", {"start": v(164.25, -66.56) * mm, "mid": v(165.97, -66.77) * mm, "end": v(166.98, -68.18) * mm});
            skLineSegment(sketch, "E695.MirrorCS", {"start": v(164.7, -66.43) * mm, "end": v(166.5, -65.87) * mm, "construction": true});
            skArc(sketch, "E696.MirrorCS", {"start": v(190.25, -54.05) * mm, "mid": v(191.1, -54.03) * mm, "end": v(191.7, -54.64) * mm});
            skLineSegment(sketch, "E697.MirrorCS", {"start": v(200.16, -44.59) * mm, "end": v(201.48, -43.48) * mm});
            skLineSegment(sketch, "E698.MirrorCS", {"start": v(250.58, 38.38) * mm, "end": v(250.97, 40.6) * mm, "construction": true});
            skArc(sketch, "E699.MirrorCS", {"start": v(239.24, -3.49) * mm, "mid": v(237.49, -1.79) * mm, "end": v(237.55, 0.65) * mm});
            skLineSegment(sketch, "E700.MirrorCS", {"start": v(247.67, 21.83) * mm, "end": v(247.94, 23.37) * mm, "construction": true});
            skLineSegment(sketch, "E701.MirrorCS", {"start": v(219.92, -25.96) * mm, "end": v(220.78, -24.46) * mm});
            skLineSegment(sketch, "E702.MirrorCS", {"start": v(236.16, -2.33) * mm, "end": v(236.82, -0.92) * mm, "construction": true});
            skArc(sketch, "E703.MirrorCS", {"start": v(222.12, -28.73) * mm, "mid": v(220.52, -26.9) * mm, "end": v(220.78, -24.46) * mm});
            skLineSegment(sketch, "E704.MirrorCS", {"start": v(176.15, -60.64) * mm, "end": v(177.72, -59.9) * mm});
            skArc(sketch, "E705.MirrorCS", {"start": v(201.27, -47.94) * mm, "mid": v(200.4, -45.66) * mm, "end": v(201.48, -43.48) * mm});
            skLineSegment(sketch, "E706.MirrorCS", {"start": v(219.14, -27.32) * mm, "end": v(219.92, -25.96) * mm, "construction": true});
            skLineSegment(sketch, "E707.MirrorCS", {"start": v(150.13, -70.9) * mm, "end": v(151.78, -70.39) * mm});
            skLineSegment(sketch, "E708.MirrorCS", {"start": v(198.96, -45.6) * mm, "end": v(200.16, -44.59) * mm, "construction": true});
            skArc(sketch, "E709.MirrorCS", {"start": v(250.95, 21.51) * mm, "mid": v(248.82, 22.7) * mm, "end": v(248.24, 25.08) * mm});
            skLineSegment(sketch, "E710.MirrorCS", {"start": v(148.63, -71.35) * mm, "end": v(150.13, -70.9) * mm, "construction": true});
            skLineSegment(sketch, "E711.MirrorCS", {"start": v(174.74, -61.3) * mm, "end": v(176.15, -60.64) * mm, "construction": true});
            skLineSegment(sketch, "E712.MirrorCS", {"start": v(137.9, -73.8) * mm, "end": v(140.03, -73.43) * mm, "construction": true});
            skLineSegment(sketch, "E713.MirrorCS", {"start": v(250.58, 38.38) * mm, "end": v(250.19, 36.16) * mm});
            skLineSegment(sketch, "E714.MirrorCS", {"start": v(247.94, 23.37) * mm, "end": v(248.24, 25.08) * mm});
            skLineSegment(sketch, "E715.MirrorCS", {"start": v(236.82, -0.92) * mm, "end": v(237.55, 0.65) * mm});
            skArc(sketch, "E716.MirrorCS", {"start": v(136.58, -74.04) * mm, "mid": v(139.07, -74.66) * mm, "end": v(140.27, -76.93) * mm});
            skLineSegment(sketch, "E717.MirrorCS", {"start": v(243.25, 12.9) * mm, "end": v(244.14, 14.82) * mm, "construction": true});
            skLineSegment(sketch, "E718.MirrorCS", {"start": v(122.9, -76.46) * mm, "end": v(124.6, -76.16) * mm});
            skLineSegment(sketch, "E719.MirrorCS", {"start": v(227.5, -12.74) * mm, "end": v(228.46, -11.05) * mm, "construction": true});
            skLineSegment(sketch, "E720.MirrorCS", {"start": v(243.25, 12.9) * mm, "end": v(242.76, 11.85) * mm});
            skLineSegment(sketch, "E721.MirrorCS", {"start": v(121.36, -76.74) * mm, "end": v(122.9, -76.46) * mm, "construction": true});
            skLineSegment(sketch, "E722.MirrorCS", {"start": v(227.5, -12.74) * mm, "end": v(225.8, -15.7) * mm});
            skArc(sketch, "E723.MirrorCS", {"start": v(129.22, -95.98) * mm, "mid": v(127.04, -95.54) * mm, "end": v(125.73, -93.74) * mm});
            skArc(sketch, "E724.MirrorCS", {"start": v(242.87, -21.23) * mm, "mid": v(244.08, -23.06) * mm, "end": v(243.75, -25.24) * mm});
            skArc(sketch, "E725.MirrorCS", {"start": v(242.76, 11.85) * mm, "mid": v(244.57, 13.42) * mm, "end": v(246.96, 13.13) * mm});
            skArc(sketch, "E726.MirrorCS", {"start": v(238.96, -33.6) * mm, "mid": v(237.23, -35) * mm, "end": v(235, -34.85) * mm});
            skArc(sketch, "E727.MirrorCS", {"start": v(259.32, 5.73) * mm, "mid": v(260.66, 4.01) * mm, "end": v(260.51, 1.83) * mm});
            skArc(sketch, "E728.MirrorCS", {"start": v(250.19, 36.16) * mm, "mid": v(252.03, 38.89) * mm, "end": v(255.3, 39.34) * mm});
            skArc(sketch, "E729.MirrorCS", {"start": v(215.4, -58.33) * mm, "mid": v(213.28, -59.04) * mm, "end": v(211.25, -58.13) * mm});
            skArc(sketch, "E730.MirrorCS", {"start": v(223.34, -48.06) * mm, "mid": v(223.84, -50.2) * mm, "end": v(222.79, -52.12) * mm});
            skArc(sketch, "E731.MirrorCS", {"start": v(225.8, -15.7) * mm, "mid": v(228.97, -13.36) * mm, "end": v(232.84, -14.14) * mm});
            skArc(sketch, "E732.MirrorCS", {"start": v(187.31, -77.85) * mm, "mid": v(185.1, -78) * mm, "end": v(183.37, -76.59) * mm});
            skArc(sketch, "E733.MirrorCS", {"start": v(197.55, -69.95) * mm, "mid": v(197.53, -72.18) * mm, "end": v(196, -73.8) * mm});
            skArc(sketch, "E734.MirrorCS", {"start": v(176.36, -64.16) * mm, "mid": v(176.1, -61.74) * mm, "end": v(177.72, -59.9) * mm});
            skArc(sketch, "E735.MirrorCS", {"start": v(158.78, -89.5) * mm, "mid": v(156.56, -89.33) * mm, "end": v(155.05, -87.7) * mm});
            skArc(sketch, "E736.MirrorCS", {"start": v(141.25, -91.08) * mm, "mid": v(140.62, -93.17) * mm, "end": v(138.74, -94.3) * mm});
            skArc(sketch, "E737.MirrorCS", {"start": v(256.43, -6.93) * mm, "mid": v(254.82, -8.47) * mm, "end": v(252.6, -8.5) * mm});
            skArc(sketch, "E738.MirrorCS", {"start": v(149.83, -74.42) * mm, "mid": v(149.93, -71.98) * mm, "end": v(151.78, -70.39) * mm});
            skArc(sketch, "E739.MirrorCS", {"start": v(268.44, 22.64) * mm, "mid": v(267.29, 20.74) * mm, "end": v(265.15, 20.13) * mm});
            skArc(sketch, "E740.MirrorCS", {"start": v(170.09, -83.13) * mm, "mid": v(169.73, -85.3) * mm, "end": v(168, -86.67) * mm});
            skArc(sketch, "E741.MirrorCS", {"start": v(122.18, -79.92) * mm, "mid": v(122.57, -77.51) * mm, "end": v(124.6, -76.16) * mm});
            skArc(sketch, "E742.MirrorCS", {"start": v(267.97, 35.63) * mm, "mid": v(269.7, 34.32) * mm, "end": v(270.12, 32.18) * mm});
            skLineSegment(sketch, "E743.MirrorCS", {"start": v(257.92, -3.74) * mm, "end": v(259, -1.43) * mm});
            skLineSegment(sketch, "E744.MirrorCS", {"start": v(162.15, -88.46) * mm, "end": v(164.58, -87.72) * mm});
            skLineSegment(sketch, "E745.MirrorCS", {"start": v(240.71, -30.55) * mm, "end": v(241.97, -28.34) * mm});
            skLineSegment(sketch, "E746.MirrorCS", {"start": v(218.1, -56.06) * mm, "end": v(220.04, -54.43) * mm});
            skLineSegment(sketch, "E747.MirrorCS", {"start": v(190.5, -76.36) * mm, "end": v(192.8, -75.28) * mm});
            skLineSegment(sketch, "E748.MirrorCS", {"start": v(132.7, -95.37) * mm, "end": v(135.2, -94.92) * mm});
            skPoint(sketch, "E749.MirrorP", {"position": v(198.56, -72.6) * mm});
            skPoint(sketch, "E750.MirrorP", {"position": v(245.13, -22.83) * mm});
            skPoint(sketch, "E751.MirrorP", {"position": v(270.6, 34.87) * mm});
            skPoint(sketch, "E752.MirrorP", {"position": v(141.44, -93.82) * mm});
            skLineSegment(sketch, "E753.MirrorCS", {"start": v(141.25, -91.08) * mm, "end": v(140.27, -76.93) * mm});
            skLineSegment(sketch, "E754.MirrorCS", {"start": v(168.8, -79.78) * mm, "end": v(164.7, -66.43) * mm});
            skLineSegment(sketch, "E755.MirrorCS", {"start": v(211.25, -58.13) * mm, "end": v(201.27, -47.94) * mm});
            skLineSegment(sketch, "E756.MirrorCS", {"start": v(140.34, -87.56) * mm, "end": v(137.9, -73.8) * mm});
            skLineSegment(sketch, "E757.MirrorCS", {"start": v(154.22, -84.25) * mm, "end": v(150.13, -70.9) * mm});
            skLineSegment(sketch, "E758.MirrorCS", {"start": v(197.55, -69.95) * mm, "end": v(191.7, -54.64) * mm});
            skPoint(sketch, "E759.MirrorP", {"position": v(184.75, -79.05) * mm});
            skPoint(sketch, "E760.MirrorP", {"position": v(237.56, -36.06) * mm});
            skPoint(sketch, "E761.MirrorP", {"position": v(267.96, 19.86) * mm});
            skPoint(sketch, "E762.MirrorP", {"position": v(126.44, -96.47) * mm});
            skLineSegment(sketch, "E763.MirrorCS", {"start": v(125.33, -90.22) * mm, "end": v(122.9, -76.46) * mm});
            skLineSegment(sketch, "E764.MirrorCS", {"start": v(150.13, -70.9) * mm, "end": v(164.7, -66.43) * mm});
            skLineSegment(sketch, "E765.MirrorCS", {"start": v(195.87, -66.84) * mm, "end": v(189.96, -54.19) * mm});
            skLineSegment(sketch, "E766.MirrorCS", {"start": v(183.37, -76.59) * mm, "end": v(176.36, -64.16) * mm});
            skLineSegment(sketch, "E767.MirrorCS", {"start": v(170.09, -83.13) * mm, "end": v(166.98, -68.18) * mm});
            skPoint(sketch, "E768.MirrorP", {"position": v(174.74, -61.3) * mm});
            skPoint(sketch, "E769.MirrorP", {"position": v(247.67, 21.83) * mm});
            skPoint(sketch, "E770.MirrorP", {"position": v(219.14, -27.32) * mm});
            skLineSegment(sketch, "E771.MirrorCS", {"start": v(125.73, -93.74) * mm, "end": v(122.18, -79.92) * mm});
            skLineSegment(sketch, "E772.MirrorCS", {"start": v(155.05, -87.7) * mm, "end": v(149.83, -74.42) * mm});
            skLineSegment(sketch, "E773.MirrorCS", {"start": v(269.05, 26.11) * mm, "end": v(269.5, 28.61) * mm});
            skLineSegment(sketch, "E774.MirrorCS", {"start": v(247.94, 23.37) * mm, "end": v(250.58, 38.38) * mm});
            skPoint(sketch, "E775.MirrorP", {"position": v(191.3, -53.57) * mm});
            skPoint(sketch, "E776.MirrorP", {"position": v(140.03, -73.43) * mm});
            skPoint(sketch, "E777.MirrorP", {"position": v(250.97, 40.6) * mm});
            skPoint(sketch, "E778.MirrorP", {"position": v(228.46, -11.05) * mm});
            skLineSegment(sketch, "E779.MirrorCS", {"start": v(261.7, 20.96) * mm, "end": v(247.94, 23.37) * mm});
            skLineSegment(sketch, "E780.MirrorCS", {"start": v(264.34, 35.97) * mm, "end": v(250.58, 38.38) * mm});
            skLineSegment(sketch, "E781.MirrorCS", {"start": v(236.82, -0.92) * mm, "end": v(243.25, 12.9) * mm});
            skPoint(sketch, "E782.MirrorP", {"position": v(213.23, -60.15) * mm});
            skPoint(sketch, "E783.MirrorP", {"position": v(156.08, -90.32) * mm});
            skPoint(sketch, "E784.MirrorP", {"position": v(255.24, -9.5) * mm});
            skLineSegment(sketch, "E785.MirrorCS", {"start": v(239.62, -19.68) * mm, "end": v(227.5, -12.74) * mm});
            skPoint(sketch, "E786.MirrorP", {"position": v(236.16, -2.33) * mm});
            skLineSegment(sketch, "E787.MirrorCS", {"start": v(223.34, -48.06) * mm, "end": v(214.74, -35.46) * mm});
            skLineSegment(sketch, "E788.MirrorCS", {"start": v(235, -34.85) * mm, "end": v(222.12, -28.73) * mm});
            skLineSegment(sketch, "E789.MirrorCS", {"start": v(122.9, -76.46) * mm, "end": v(137.9, -73.8) * mm});
            skLineSegment(sketch, "E790.MirrorCS", {"start": v(182.07, -73.3) * mm, "end": v(176.15, -60.64) * mm});
            skLineSegment(sketch, "E791.MirrorCS", {"start": v(200.16, -44.59) * mm, "end": v(211.83, -34.78) * mm});
            skPoint(sketch, "E792.MirrorP", {"position": v(166.5, -65.87) * mm});
            skPoint(sketch, "E793.MirrorP", {"position": v(213.38, -33.48) * mm});
            skPoint(sketch, "E794.MirrorP", {"position": v(244.14, 14.82) * mm});
            skPoint(sketch, "E795.MirrorP", {"position": v(198.96, -45.6) * mm});
            skPoint(sketch, "E796.MirrorP", {"position": v(148.63, -71.35) * mm});
            skPoint(sketch, "E797.MirrorP", {"position": v(170.65, -85.85) * mm});
            skLineSegment(sketch, "E798.MirrorCS", {"start": v(219.92, -25.96) * mm, "end": v(227.5, -12.74) * mm});
            skLineSegment(sketch, "E799.MirrorCS", {"start": v(255.92, 7) * mm, "end": v(243.25, 12.9) * mm});
            skLineSegment(sketch, "E800.MirrorCS", {"start": v(232.05, -32.9) * mm, "end": v(219.92, -25.96) * mm});
            skLineSegment(sketch, "E801.MirrorCS", {"start": v(265.15, 20.13) * mm, "end": v(250.95, 21.51) * mm});
            skLineSegment(sketch, "E802.MirrorCS", {"start": v(252.6, -8.5) * mm, "end": v(239.24, -3.49) * mm});
            skLineSegment(sketch, "E803.MirrorCS", {"start": v(242.87, -21.23) * mm, "end": v(232.84, -14.14) * mm});
            skLineSegment(sketch, "E804.MirrorCS", {"start": v(209.14, -55.28) * mm, "end": v(200.16, -44.59) * mm});
            skLineSegment(sketch, "E805.MirrorCS", {"start": v(176.15, -60.64) * mm, "end": v(189.96, -54.19) * mm});
            skLineSegment(sketch, "E806.MirrorCS", {"start": v(220.81, -45.48) * mm, "end": v(211.83, -34.78) * mm});
            skLineSegment(sketch, "E807.MirrorCS", {"start": v(267.97, 35.63) * mm, "end": v(255.3, 39.34) * mm});
            skLineSegment(sketch, "E808.MirrorCS", {"start": v(249.48, -6.81) * mm, "end": v(236.82, -0.92) * mm});
            skPoint(sketch, "E809.MirrorP", {"position": v(224.9, -50.34) * mm});
            skPoint(sketch, "E810.MirrorP", {"position": v(261.67, 4.32) * mm});
            skLineSegment(sketch, "E811.MirrorCS", {"start": v(259.32, 5.73) * mm, "end": v(246.96, 13.13) * mm});
            skPoint(sketch, "E812.MirrorP", {"position": v(121.36, -76.74) * mm});
            skLineSegment(sketch, "E813.bottom", {"start": v(-59.47, 53.8) * mm, "end": v(-59.8, 56.31) * mm});
            skLineSegment(sketch, "E813.top", {"start": v(-41.06, 49.78) * mm, "end": v(-43.02, 64.9) * mm});
            skLineSegment(sketch, "E813.left", {"start": v(-52.36, 48.31) * mm, "end": v(-41.06, 49.78) * mm});
            skLineSegment(sketch, "E813.right", {"start": v(-54.32, 63.43) * mm, "end": v(-43.02, 64.9) * mm});
            skLineSegment(sketch, "E814", {"start": v(-57.97, 63.26) * mm, "end": v(-45.05, 66.43) * mm});
            skLineSegment(sketch, "E815", {"start": v(-43.04, 65.05) * mm, "end": v(-43.02, 64.9) * mm});
            skLineSegment(sketch, "E816", {"start": v(-55.81, 47.67) * mm, "end": v(-44.16, 48.37) * mm});
            skLineSegment(sketch, "E817", {"start": v(-41.06, 49.78) * mm, "end": v(-41.32, 51.8) * mm});
            skPoint(sketch, "E818.visualSharp", {"position": v(-58.65, 47.5) * mm});
            skArc(sketch, "E818.filletArc", {"start": v(-59.02, 50.32) * mm, "mid": v(-57.94, 48.36) * mm, "end": v(-55.81, 47.67) * mm});
            skPoint(sketch, "E819.visualSharp", {"position": v(-60.61, 62.61) * mm});
            skArc(sketch, "E819.filletArc", {"start": v(-57.97, 63.26) * mm, "mid": v(-59.75, 62.02) * mm, "end": v(-60.26, 59.9) * mm});
            skPoint(sketch, "E820.visualSharp", {"position": v(-40.9, 48.57) * mm});
            skArc(sketch, "E820.filletArc", {"start": v(-44.16, 48.37) * mm, "mid": v(-42, 49.47) * mm, "end": v(-41.32, 51.8) * mm});
            skPoint(sketch, "E821.visualSharp", {"position": v(-43.28, 66.86) * mm});
            skArc(sketch, "E821.filletArc", {"start": v(-43.04, 65.05) * mm, "mid": v(-43.74, 66.2) * mm, "end": v(-45.05, 66.43) * mm});
            skLineSegment(sketch, "E822.0", {"start": v(-40.9, 48.57) * mm, "end": v(-41.06, 49.78) * mm, "construction": true});
            skLineSegment(sketch, "E823.0", {"start": v(-43.02, 64.9) * mm, "end": v(-43.28, 66.86) * mm, "construction": true});
            skLineSegment(sketch, "E824.bottom", {"start": v(275.18, 55.56) * mm, "end": v(274.96, 53.03) * mm});
            skLineSegment(sketch, "E824.top", {"start": v(255.38, 63.66) * mm, "end": v(254.05, 48.48) * mm});
            skLineSegment(sketch, "E824.left", {"start": v(269.4, 62.43) * mm, "end": v(255.38, 63.66) * mm});
            skLineSegment(sketch, "E824.right", {"start": v(268.08, 47.25) * mm, "end": v(254.05, 48.48) * mm});
            skLineSegment(sketch, "E825", {"start": v(271.37, 46.96) * mm, "end": v(257.35, 48.2) * mm});
            skLineSegment(sketch, "E826", {"start": v(254.05, 48.48) * mm, "end": v(254.34, 51.78) * mm});
            skLineSegment(sketch, "E827", {"start": v(272.95, 62.34) * mm, "end": v(258.76, 64.7) * mm});
            skLineSegment(sketch, "E828", {"start": v(255.38, 63.66) * mm, "end": v(255.23, 61.95) * mm});
            skPoint(sketch, "E829.visualSharp", {"position": v(275.73, 61.88) * mm});
            skArc(sketch, "E829.filletArc", {"start": v(275.48, 59.07) * mm, "mid": v(274.86, 61.2) * mm, "end": v(272.95, 62.34) * mm});
            skPoint(sketch, "E830.visualSharp", {"position": v(274.4, 46.7) * mm});
            skArc(sketch, "E830.filletArc", {"start": v(271.37, 46.96) * mm, "mid": v(273.6, 47.67) * mm, "end": v(274.67, 49.74) * mm});
            skPoint(sketch, "E831.visualSharp", {"position": v(255.51, 65.23) * mm});
            skArc(sketch, "E831.filletArc", {"start": v(258.76, 64.7) * mm, "mid": v(256.4, 64.1) * mm, "end": v(255.23, 61.95) * mm});
            skPoint(sketch, "E832.visualSharp", {"position": v(254.05, 48.48) * mm});
            skArc(sketch, "E832.filletArc", {"start": v(254.34, 51.78) * mm, "mid": v(255.1, 49.36) * mm, "end": v(257.35, 48.2) * mm});
            skLineSegment(sketch, "E833.0", {"start": v(255.51, 65.23) * mm, "end": v(255.38, 63.66) * mm, "construction": true});
            skLineSegment(sketch, "E834.0", {"start": v(254.05, 48.48) * mm, "end": v(254.05, 48.48) * mm});
            skArc(sketch, "E835.filletArc", {"start": v(17.25, 216.85) * mm, "mid": v(13.97, 213.26) * mm, "end": v(14.19, 208.4) * mm});
            skArc(sketch, "E836.filletArc", {"start": v(28, 214.86) * mm, "mid": v(24.41, 218.14) * mm, "end": v(19.55, 217.92) * mm});
            skPoint(sketch, "E837.newPointA", {"position": v(-4.57, 199.9) * mm});
            skArc(sketch, "E837.filletArc", {"start": v(1.68, 196.85) * mm, "mid": v(-2.63, 199.09) * mm, "end": v(-7.27, 197.62) * mm});
            skPoint(sketch, "E838.newPointA", {"position": v(-11.96, 193.68) * mm});
            skPoint(sketch, "E838.newPointB", {"position": v(-12.52, 189.63) * mm});
            skArc(sketch, "E838.filletArc", {"start": v(-9.67, 195.6) * mm, "mid": v(-11.88, 191.6) * mm, "end": v(-10.83, 187.16) * mm});
            skArc(sketch, "E839.filletArc", {"start": v(-20.97, 173.2) * mm, "mid": v(-25.79, 173.81) * mm, "end": v(-29.63, 170.84) * mm});
            skArc(sketch, "E840.filletArc", {"start": v(-30.9, 168.64) * mm, "mid": v(-31.51, 163.82) * mm, "end": v(-28.54, 159.97) * mm});
            skArc(sketch, "E841.filletArc", {"start": v(-38.15, 147.36) * mm, "mid": v(-43, 147.57) * mm, "end": v(-46.59, 144.28) * mm});
            skArc(sketch, "E842.filletArc", {"start": v(-47.93, 141.41) * mm, "mid": v(-48.24, 136.87) * mm, "end": v(-45.43, 133.28) * mm});
            skArc(sketch, "E843.filletArc", {"start": v(-50.14, 117.23) * mm, "mid": v(-54.89, 116.17) * mm, "end": v(-57.5, 112.07) * mm});
            skArc(sketch, "E844.filletArc", {"start": v(-58.05, 108.92) * mm, "mid": v(-57.19, 104.47) * mm, "end": v(-53.58, 101.72) * mm});
            skArc(sketch, "E845.filletArc", {"start": v(-55.88, 90.19) * mm, "mid": v(-60.46, 88.54) * mm, "end": v(-62.53, 84.15) * mm});
            skArc(sketch, "E846.filletArc", {"start": v(-62.65, 81.6) * mm, "mid": v(-61, 77.04) * mm, "end": v(-56.6, 74.97) * mm});
            skArc(sketch, "E847.filletArc", {"start": v(-54.32, 63.43) * mm, "mid": v(-58.53, 61) * mm, "end": v(-59.8, 56.31) * mm});
            skArc(sketch, "E848.filletArc", {"start": v(-59.47, 53.8) * mm, "mid": v(-57.05, 49.58) * mm, "end": v(-52.36, 48.31) * mm});
            skArc(sketch, "E849.filletArc", {"start": v(-51.75, 35.7) * mm, "mid": v(-55.84, 33.08) * mm, "end": v(-56.9, 28.34) * mm});
            skArc(sketch, "E850.filletArc", {"start": v(-56.46, 25.84) * mm, "mid": v(-53.84, 21.74) * mm, "end": v(-49.1, 20.69) * mm});
            skArc(sketch, "E851.filletArc", {"start": v(-44.3, 7.42) * mm, "mid": v(-47.58, 3.84) * mm, "end": v(-47.37, -1.02) * mm});
            skArc(sketch, "E852.filletArc", {"start": v(-46.3, -3.32) * mm, "mid": v(-42.7, -6.6) * mm, "end": v(-37.85, -6.39) * mm});
            skArc(sketch, "E853.filletArc", {"start": v(-29.58, -28.95) * mm, "mid": v(-25.73, -31.92) * mm, "end": v(-20.9, -31.3) * mm});
            skArc(sketch, "E854.filletArc", {"start": v(-28.49, -18.08) * mm, "mid": v(-31.46, -21.93) * mm, "end": v(-30.84, -26.75) * mm});
            skPoint(sketch, "E855.newPointA", {"position": v(-4.5, -56.62) * mm});
            skArc(sketch, "E855.filletArc", {"start": v(-7.2, -54.35) * mm, "mid": v(-2.56, -55.81) * mm, "end": v(1.75, -53.57) * mm});
            skPoint(sketch, "E856.newPointA", {"position": v(-11.9, -50.4) * mm});
            skArc(sketch, "E856.filletArc", {"start": v(-9.92, -43.77) * mm, "mid": v(-11.38, -48.4) * mm, "end": v(-9.14, -52.72) * mm});
            skArc(sketch, "E857.filletArc", {"start": v(17.26, -73.58) * mm, "mid": v(22.04, -74.45) * mm, "end": v(26.04, -71.7) * mm});
            skArc(sketch, "E858.filletArc", {"start": v(13.24, -63.42) * mm, "mid": v(12.37, -68.2) * mm, "end": v(15.13, -72.2) * mm});
            skArc(sketch, "E859.filletArc", {"start": v(46.73, -87.22) * mm, "mid": v(51.57, -86.76) * mm, "end": v(54.66, -83) * mm});
            skArc(sketch, "E860.filletArc", {"start": v(40.09, -78.55) * mm, "mid": v(40.55, -83.39) * mm, "end": v(44.3, -86.48) * mm});
            skArc(sketch, "E861.filletArc", {"start": v(75.18, -94.36) * mm, "mid": v(79.93, -93.31) * mm, "end": v(82.54, -89.21) * mm});
            skArc(sketch, "E862.filletArc", {"start": v(67.53, -86.57) * mm, "mid": v(68.58, -91.31) * mm, "end": v(72.68, -93.92) * mm});
            skArc(sketch, "E863.filletArc", {"start": v(95.4, -91.03) * mm, "mid": v(97.26, -95.52) * mm, "end": v(101.75, -97.38) * mm});
            skArc(sketch, "E864.filletArc", {"start": v(104.29, -97.38) * mm, "mid": v(108.78, -95.52) * mm, "end": v(110.64, -91.03) * mm});
            skPoint(sketch, "E865.newPointA", {"position": v(129.22, -95.98) * mm});
            skArc(sketch, "E865.filletArc", {"start": v(125.33, -90.22) * mm, "mid": v(127.94, -94.32) * mm, "end": v(132.7, -95.37) * mm});
            skPoint(sketch, "E866.newPointA", {"position": v(138.74, -94.3) * mm});
            skArc(sketch, "E866.filletArc", {"start": v(135.2, -94.92) * mm, "mid": v(139.29, -92.3) * mm, "end": v(140.34, -87.56) * mm});
            skPoint(sketch, "E867.newPointA", {"position": v(168, -86.67) * mm});
            skArc(sketch, "E867.filletArc", {"start": v(164.58, -87.72) * mm, "mid": v(168.33, -84.62) * mm, "end": v(168.8, -79.78) * mm});
            skPoint(sketch, "E868.newPointA", {"position": v(158.78, -89.5) * mm});
            skArc(sketch, "E868.filletArc", {"start": v(154.22, -84.25) * mm, "mid": v(157.32, -88) * mm, "end": v(162.15, -88.46) * mm});
            skArc(sketch, "E869.filletArc", {"start": v(192.8, -75.28) * mm, "mid": v(196.09, -71.7) * mm, "end": v(195.87, -66.84) * mm});
            skArc(sketch, "E870.filletArc", {"start": v(182.07, -73.3) * mm, "mid": v(185.65, -76.57) * mm, "end": v(190.5, -76.36) * mm});
            skArc(sketch, "E871.filletArc", {"start": v(220.04, -54.43) * mm, "mid": v(222.28, -50.11) * mm, "end": v(220.81, -45.48) * mm});
            skArc(sketch, "E872.filletArc", {"start": v(209.14, -55.28) * mm, "mid": v(213.46, -57.52) * mm, "end": v(218.1, -56.06) * mm});
            skArc(sketch, "E873.filletArc", {"start": v(241.97, -28.34) * mm, "mid": v(242.59, -23.52) * mm, "end": v(239.62, -19.68) * mm});
            skArc(sketch, "E874.filletArc", {"start": v(232.05, -32.9) * mm, "mid": v(236.87, -33.52) * mm, "end": v(240.71, -30.55) * mm});
            skArc(sketch, "E875.filletArc", {"start": v(259, -1.43) * mm, "mid": v(259.2, 3.42) * mm, "end": v(255.92, 7) * mm});
            skArc(sketch, "E876.filletArc", {"start": v(249.48, -6.81) * mm, "mid": v(254.34, -7.02) * mm, "end": v(257.92, -3.74) * mm});
            skArc(sketch, "E877.filletArc", {"start": v(269.5, 28.61) * mm, "mid": v(268.44, 33.36) * mm, "end": v(264.34, 35.97) * mm});
            skArc(sketch, "E878.filletArc", {"start": v(261.7, 20.96) * mm, "mid": v(266.45, 22.01) * mm, "end": v(269.05, 26.11) * mm});
            skArc(sketch, "E879.filletArc", {"start": v(275.18, 55.56) * mm, "mid": v(273.72, 60.2) * mm, "end": v(269.4, 62.43) * mm});
            skArc(sketch, "E880.filletArc", {"start": v(268.08, 47.25) * mm, "mid": v(272.71, 48.71) * mm, "end": v(274.96, 53.03) * mm});
            skArc(sketch, "E881.filletArc", {"start": v(275.15, 83.57) * mm, "mid": v(273.08, 87.96) * mm, "end": v(268.5, 89.6) * mm});
            skArc(sketch, "E882.filletArc", {"start": v(269.24, 74.38) * mm, "mid": v(273.63, 76.46) * mm, "end": v(275.28, 81.03) * mm});
            skArc(sketch, "E883.filletArc", {"start": v(270.07, 112.17) * mm, "mid": v(267.46, 116.27) * mm, "end": v(262.72, 117.32) * mm});
            skArc(sketch, "E884.filletArc", {"start": v(265.36, 102.31) * mm, "mid": v(269.46, 104.92) * mm, "end": v(270.51, 109.67) * mm});
            skArc(sketch, "E885.filletArc", {"start": v(259.15, 144.37) * mm, "mid": v(255.56, 147.66) * mm, "end": v(250.7, 147.44) * mm});
            skArc(sketch, "E886.filletArc", {"start": v(257.15, 133.63) * mm, "mid": v(260.43, 137.21) * mm, "end": v(260.22, 142.07) * mm});
            skArc(sketch, "E887.filletArc", {"start": v(242.18, 170.92) * mm, "mid": v(238.33, 173.9) * mm, "end": v(233.51, 173.27) * mm});
            skArc(sketch, "E888.filletArc", {"start": v(241.09, 160.05) * mm, "mid": v(244.06, 163.9) * mm, "end": v(243.44, 168.72) * mm});
            skArc(sketch, "E889.filletArc", {"start": v(222.52, 187.11) * mm, "mid": v(223.98, 191.75) * mm, "end": v(221.74, 196.06) * mm});
            skArc(sketch, "E890.filletArc", {"start": v(219.8, 197.69) * mm, "mid": v(215.16, 199.15) * mm, "end": v(210.85, 196.9) * mm});
            skArc(sketch, "E891.filletArc", {"start": v(198.33, 208.46) * mm, "mid": v(198.55, 213.32) * mm, "end": v(195.26, 216.9) * mm});
            skArc(sketch, "E892.filletArc", {"start": v(192.96, 217.97) * mm, "mid": v(188.1, 218.18) * mm, "end": v(184.52, 214.9) * mm});
            skPoint(sketch, "E893.newPointA", {"position": v(167.9, 230.04) * mm});
            skArc(sketch, "E893.filletArc", {"start": v(168.7, 223.16) * mm, "mid": v(168.24, 228) * mm, "end": v(164.49, 231.09) * mm});
            skPoint(sketch, "E894.newPointA", {"position": v(158.69, 232.87) * mm});
            skArc(sketch, "E894.filletArc", {"start": v(162.06, 231.83) * mm, "mid": v(157.22, 231.37) * mm, "end": v(154.13, 227.62) * mm});
            skPoint(sketch, "E895.newPointA", {"position": v(138.65, 237.65) * mm});
            skArc(sketch, "E895.filletArc", {"start": v(140.24, 230.92) * mm, "mid": v(139.2, 235.67) * mm, "end": v(135.1, 238.28) * mm});
            skPoint(sketch, "E896.newPointA", {"position": v(129.12, 239.33) * mm});
            skArc(sketch, "E896.filletArc", {"start": v(132.6, 238.72) * mm, "mid": v(127.85, 237.67) * mm, "end": v(125.24, 233.57) * mm});
            skArc(sketch, "E897.filletArc", {"start": v(113.93, 234.28) * mm, "mid": v(112.07, 238.77) * mm, "end": v(107.58, 240.63) * mm});
            skArc(sketch, "E898.filletArc", {"start": v(105.04, 240.63) * mm, "mid": v(100.55, 238.77) * mm, "end": v(98.69, 234.28) * mm});
            skArc(sketch, "E899.filletArc", {"start": v(87.27, 233.56) * mm, "mid": v(84.66, 237.66) * mm, "end": v(79.91, 238.7) * mm});
            skArc(sketch, "E900.filletArc", {"start": v(77.4, 238.26) * mm, "mid": v(73.31, 235.65) * mm, "end": v(72.26, 230.9) * mm});
            skArc(sketch, "E901.filletArc", {"start": v(58.38, 227.6) * mm, "mid": v(55.28, 231.34) * mm, "end": v(50.45, 231.8) * mm});
            skArc(sketch, "E902.filletArc", {"start": v(48.02, 231.06) * mm, "mid": v(44.27, 227.96) * mm, "end": v(43.8, 223.12) * mm});
            skSolve(sketch);
        }
        {
            var Q0;
            {var subQ0=sQuery(id+"F5.wireOp",EDGE,"E468.MirrorCS");Q0=makeQuery(id+"F5.imprint","IMPRINT",FACE,{"disambiguationData":[TD([[makeQuery(id+"F5.imprint","IMPRINT",EDGE,{"derivedFrom":subQ0}),1.0]])]});}
            var Q1;
            {var subQ0=sQuery(id+"F5.wireOp",EDGE,"E540.MirrorCS");Q1=makeQuery(id+"F5.imprint","IMPRINT",FACE,{"disambiguationData":[TD([[makeQuery(id+"F5.imprint","IMPRINT",EDGE,{"derivedFrom":subQ0}),1.0]])]});}
            var Q2;
            {var subQ0=sQuery(id+"F5.wireOp",EDGE,"E487.MirrorCS");Q2=makeQuery(id+"F5.imprint","IMPRINT",FACE,{"disambiguationData":[TD([[makeQuery(id+"F5.imprint","IMPRINT",EDGE,{"derivedFrom":subQ0}),-1.0]])]});}
            var Q3;
            {var subQ4=sQuery(id+"F5.wireOp",EDGE,"E417.MirrorCS");Q3=makeQuery(id+"F5.imprint","IMPRINT",FACE,{"disambiguationData":[TD([[makeQuery(id+"F5.imprint","IMPRINT",EDGE,{"derivedFrom":subQ4}),1.0]])]});}
            var Q4;
            {var subQ0=sQuery(id+"F5.wireOp",EDGE,"E555.MirrorCS");Q4=makeQuery(id+"F5.imprint","IMPRINT",FACE,{"disambiguationData":[TD([[makeQuery(id+"F5.imprint","IMPRINT",EDGE,{"derivedFrom":subQ0}),-1.0]])]});}
            var Q5;
            {var subQ0=sQuery(id+"F5.wireOp",EDGE,"E506.MirrorCS");Q5=makeQuery(id+"F5.imprint","IMPRINT",FACE,{"disambiguationData":[TD([[makeQuery(id+"F5.imprint","IMPRINT",EDGE,{"derivedFrom":subQ0}),1.0]])]});}
            var Q6;
            {var subQ5=sQuery(id+"F5.wireOp",EDGE,"E485.MirrorCS");Q6=makeQuery(id+"F5.imprint","IMPRINT",FACE,{"disambiguationData":[TD([[makeQuery(id+"F5.imprint","IMPRINT",EDGE,{"derivedFrom":subQ5}),1.0]])]});}
            var Q7;
            {var subQ1=sQuery(id+"F5.wireOp",EDGE,"E475.MirrorCS");Q7=makeQuery(id+"F5.imprint","IMPRINT",FACE,{"disambiguationData":[TD([[makeQuery(id+"F5.imprint","IMPRINT",EDGE,{"derivedFrom":subQ1}),1.0]])]});}
            var Q8;
            {var subQ0=sQuery(id+"F5.wireOp",EDGE,"E509.MirrorCS");Q8=makeQuery(id+"F5.imprint","IMPRINT",FACE,{"disambiguationData":[TD([[makeQuery(id+"F5.imprint","IMPRINT",EDGE,{"derivedFrom":subQ0}),-1.0]])]});}
            var Q9;
            {var subQ0=sQuery(id+"F5.wireOp",EDGE,"E550.MirrorCS");Q9=makeQuery(id+"F5.imprint","IMPRINT",FACE,{"disambiguationData":[TD([[makeQuery(id+"F5.imprint","IMPRINT",EDGE,{"derivedFrom":subQ0}),1.0]])]});}
            var Q10;
            {var subQ0=sQuery(id+"F5.wireOp",EDGE,"E499.MirrorCS");Q10=makeQuery(id+"F5.imprint","IMPRINT",FACE,{"disambiguationData":[TD([[makeQuery(id+"F5.imprint","IMPRINT",EDGE,{"derivedFrom":subQ0}),1.0]])]});}
            var Q11;
            {var subQ0=sQuery(id+"F5.wireOp",EDGE,"E507.MirrorCS");Q11=makeQuery(id+"F5.imprint","IMPRINT",FACE,{"disambiguationData":[TD([[makeQuery(id+"F5.imprint","IMPRINT",EDGE,{"derivedFrom":subQ0}),-1.0]])]});}
            var Q12;
            {var subQ5=sQuery(id+"F5.wireOp",EDGE,"E304");Q12=makeQuery(id+"F5.imprint","IMPRINT",FACE,{"disambiguationData":[TD([[makeQuery(id+"F5.imprint","IMPRINT",EDGE,{"derivedFrom":subQ5}),1.0]])]});}
            var Q13;
            {var subQ11=sQuery(id+"F5.wireOp",EDGE,"E384.bottom");Q13=makeQuery(id+"F5.imprint","IMPRINT",FACE,{"disambiguationData":[TD([[makeQuery(id+"F5.imprint","IMPRINT",EDGE,{"derivedFrom":subQ11}),-1.0]])]});}
            var Q14;
            {var subQ11=sQuery(id+"F5.wireOp",EDGE,"E373.bottom");Q14=makeQuery(id+"F5.imprint","IMPRINT",FACE,{"disambiguationData":[TD([[makeQuery(id+"F5.imprint","IMPRINT",EDGE,{"derivedFrom":subQ11}),-1.0]])]});}
            var Q15;
            {var subQ11=sQuery(id+"F5.wireOp",EDGE,"E406.bottom");Q15=makeQuery(id+"F5.imprint","IMPRINT",FACE,{"disambiguationData":[TD([[makeQuery(id+"F5.imprint","IMPRINT",EDGE,{"derivedFrom":subQ11}),-1.0]])]});}
            var Q16;
            {var subQ0=sQuery(id+"F5.wireOp",EDGE,"E556.MirrorCS");Q16=makeQuery(id+"F5.imprint","IMPRINT",FACE,{"disambiguationData":[TD([[makeQuery(id+"F5.imprint","IMPRINT",EDGE,{"derivedFrom":subQ0}),1.0]])]});}
            var Q17;
            {var subQ11=sQuery(id+"F5.wireOp",EDGE,"E395.bottom");Q17=makeQuery(id+"F5.imprint","IMPRINT",FACE,{"disambiguationData":[TD([[makeQuery(id+"F5.imprint","IMPRINT",EDGE,{"derivedFrom":subQ11}),-1.0]])]});}
            var Q18;
            {var subQ5=sQuery(id+"F5.wireOp",EDGE,"E511.MirrorCS");Q18=makeQuery(id+"F5.imprint","IMPRINT",FACE,{"disambiguationData":[TD([[makeQuery(id+"F5.imprint","IMPRINT",EDGE,{"derivedFrom":subQ5}),1.0]])]});}
            var Q19;
            {var subQ11=sQuery(id+"F5.wireOp",EDGE,"E483.MirrorCS");Q19=makeQuery(id+"F5.imprint","IMPRINT",FACE,{"disambiguationData":[TD([[makeQuery(id+"F5.imprint","IMPRINT",EDGE,{"derivedFrom":subQ11}),1.0]])]});}
            var Q20;
            {var subQ9=sQuery(id+"F5.wireOp",EDGE,"E813.bottom");Q20=makeQuery(id+"F5.imprint","IMPRINT",FACE,{"disambiguationData":[TD([[makeQuery(id+"F5.imprint","IMPRINT",EDGE,{"derivedFrom":subQ9}),-1.0]])]});}
            var Q21;
            {var subQ6=sQuery(id+"F5.wireOp",EDGE,"E824.bottom");Q21=makeQuery(id+"F5.imprint","IMPRINT",FACE,{"disambiguationData":[TD([[makeQuery(id+"F5.imprint","IMPRINT",EDGE,{"derivedFrom":subQ6}),-1.0]])]});}
            var Q22;
            {var subQ5=sQuery(id+"F5.wireOp",EDGE,"E484.MirrorCS");Q22=makeQuery(id+"F5.imprint","IMPRINT",FACE,{"disambiguationData":[TD([[makeQuery(id+"F5.imprint","IMPRINT",EDGE,{"derivedFrom":subQ5}),1.0]])]});}
            var Q23;
            {var subQ0=sQuery(id+"F5.wireOp",EDGE,"E488.MirrorCS");Q23=makeQuery(id+"F5.imprint","IMPRINT",FACE,{"disambiguationData":[TD([[makeQuery(id+"F5.imprint","IMPRINT",EDGE,{"derivedFrom":subQ0}),1.0]])]});}
            var Q24;
            {var subQ0=sQuery(id+"F5.wireOp",EDGE,"E560.MirrorCS");Q24=makeQuery(id+"F5.imprint","IMPRINT",FACE,{"disambiguationData":[TD([[makeQuery(id+"F5.imprint","IMPRINT",EDGE,{"derivedFrom":subQ0}),1.0]])]});}
            var Q25;
            {var subQ5=sQuery(id+"F5.wireOp",EDGE,"E385");Q25=makeQuery(id+"F5.imprint","IMPRINT",FACE,{"disambiguationData":[TD([[makeQuery(id+"F5.imprint","IMPRINT",EDGE,{"derivedFrom":subQ5}),-1.0]])]});}
            var Q26;
            {var subQ1=sQuery(id+"F5.wireOp",EDGE,"E814");Q26=makeQuery(id+"F5.imprint","IMPRINT",FACE,{"disambiguationData":[TD([[makeQuery(id+"F5.imprint","IMPRINT",EDGE,{"derivedFrom":subQ1}),-1.0]])]});}
            var Q27;
            {var subQ5=sQuery(id+"F5.wireOp",EDGE,"E396");Q27=makeQuery(id+"F5.imprint","IMPRINT",FACE,{"disambiguationData":[TD([[makeQuery(id+"F5.imprint","IMPRINT",EDGE,{"derivedFrom":subQ5}),-1.0]])]});}
            var Q28;
            {var subQ0=sQuery(id+"F5.wireOp",EDGE,"E528.MirrorCS");Q28=makeQuery(id+"F5.imprint","IMPRINT",FACE,{"disambiguationData":[TD([[makeQuery(id+"F5.imprint","IMPRINT",EDGE,{"derivedFrom":subQ0}),1.0]])]});}
            var Q29;
            {var subQ5=sQuery(id+"F5.wireOp",EDGE,"E409");Q29=makeQuery(id+"F5.imprint","IMPRINT",FACE,{"disambiguationData":[TD([[makeQuery(id+"F5.imprint","IMPRINT",EDGE,{"derivedFrom":subQ5}),1.0]])]});}
            var Q30;
            {var subQ0=sQuery(id+"F5.wireOp",EDGE,"E500.MirrorCS");Q30=makeQuery(id+"F5.imprint","IMPRINT",FACE,{"disambiguationData":[TD([[makeQuery(id+"F5.imprint","IMPRINT",EDGE,{"derivedFrom":subQ0}),1.0]])]});}
            var Q31;
            {var subQ5=sQuery(id+"F5.wireOp",EDGE,"E398");Q31=makeQuery(id+"F5.imprint","IMPRINT",FACE,{"disambiguationData":[TD([[makeQuery(id+"F5.imprint","IMPRINT",EDGE,{"derivedFrom":subQ5}),1.0]])]});}
            var Q32;
            {var subQ5=sQuery(id+"F5.wireOp",EDGE,"E827");Q32=makeQuery(id+"F5.imprint","IMPRINT",FACE,{"disambiguationData":[TD([[makeQuery(id+"F5.imprint","IMPRINT",EDGE,{"derivedFrom":subQ5}),1.0]])]});}
            var Q33;
            {var subQ5=sQuery(id+"F5.wireOp",EDGE,"E363");Q33=makeQuery(id+"F5.imprint","IMPRINT",FACE,{"disambiguationData":[TD([[makeQuery(id+"F5.imprint","IMPRINT",EDGE,{"derivedFrom":subQ5}),-1.0]])]});}
            var Q34;
            {var subQ0=sQuery(id+"F5.wireOp",EDGE,"E532.MirrorCS");Q34=makeQuery(id+"F5.imprint","IMPRINT",FACE,{"disambiguationData":[TD([[makeQuery(id+"F5.imprint","IMPRINT",EDGE,{"derivedFrom":subQ0}),-1.0]])]});}
            var Q35;
            {var subQ5=sQuery(id+"F5.wireOp",EDGE,"E376");Q35=makeQuery(id+"F5.imprint","IMPRINT",FACE,{"disambiguationData":[TD([[makeQuery(id+"F5.imprint","IMPRINT",EDGE,{"derivedFrom":subQ5}),1.0]])]});}
            var Q36;
            {var subQ0=sQuery(id+"F5.wireOp",EDGE,"E501.MirrorCS");Q36=makeQuery(id+"F5.imprint","IMPRINT",FACE,{"disambiguationData":[TD([[makeQuery(id+"F5.imprint","IMPRINT",EDGE,{"derivedFrom":subQ0}),-1.0]])]});}
            var Q37;
            {var subQ5=sQuery(id+"F5.wireOp",EDGE,"E374");Q37=makeQuery(id+"F5.imprint","IMPRINT",FACE,{"disambiguationData":[TD([[makeQuery(id+"F5.imprint","IMPRINT",EDGE,{"derivedFrom":subQ5}),-1.0]])]});}
            var Q38;
            {var subQ0=sQuery(id+"F5.wireOp",EDGE,"E486.MirrorCS");Q38=makeQuery(id+"F5.imprint","IMPRINT",FACE,{"disambiguationData":[TD([[makeQuery(id+"F5.imprint","IMPRINT",EDGE,{"derivedFrom":subQ0}),-1.0]])]});}
            var Q39;
            {var subQ5=sQuery(id+"F5.wireOp",EDGE,"E387");Q39=makeQuery(id+"F5.imprint","IMPRINT",FACE,{"disambiguationData":[TD([[makeQuery(id+"F5.imprint","IMPRINT",EDGE,{"derivedFrom":subQ5}),1.0]])]});}
            var Q40;
            {var subQ5=sQuery(id+"F5.wireOp",EDGE,"E816");Q40=makeQuery(id+"F5.imprint","IMPRINT",FACE,{"disambiguationData":[TD([[makeQuery(id+"F5.imprint","IMPRINT",EDGE,{"derivedFrom":subQ5}),1.0]])]});}
            var Q41;
            {var subQ5=sQuery(id+"F5.wireOp",EDGE,"E407");Q41=makeQuery(id+"F5.imprint","IMPRINT",FACE,{"disambiguationData":[TD([[makeQuery(id+"F5.imprint","IMPRINT",EDGE,{"derivedFrom":subQ5}),-1.0]])]});}
            var Q42;
            {var subQ0=sQuery(id+"F5.wireOp",EDGE,"E527.MirrorCS");Q42=makeQuery(id+"F5.imprint","IMPRINT",FACE,{"disambiguationData":[TD([[makeQuery(id+"F5.imprint","IMPRINT",EDGE,{"derivedFrom":subQ0}),-1.0]])]});}
            var Q43;
            {var subQ0=sQuery(id+"F5.wireOp",EDGE,"E397");Q43=makeQuery(id+"F5.imprint","IMPRINT",FACE,{"disambiguationData":[TD([[makeQuery(id+"F5.imprint","IMPRINT",EDGE,{"derivedFrom":subQ0}),-1.0]])]});}
            var Q44;
            {var subQ0=sQuery(id+"F5.wireOp",EDGE,"E495.MirrorCS");var subQ1=sQuery(id+"F5.wireOp",EDGE,"E481.MirrorCS");var subQ2=makeQuery(id+"F5.imprint","INTERSECT",VERTEX,{"derivedFrom":[subQ1,subQ0]});Q44=makeQuery(id+"F5.imprint","IMPRINT",FACE,{"disambiguationData":[TD([[makeQuery(id+"F5.imprint","IMPRINT",EDGE,{"disambiguationData":[TD([[subQ2,-1.0]])],"derivedFrom":subQ1}),1.0]])]});}
            var Q45;
            {var subQ0=sQuery(id+"F5.wireOp",EDGE,"E366");Q45=makeQuery(id+"F5.imprint","IMPRINT",FACE,{"disambiguationData":[TD([[makeQuery(id+"F5.imprint","IMPRINT",EDGE,{"derivedFrom":subQ0}),1.0]])]});}
            var Q46;
            {var subQ0=sQuery(id+"F5.wireOp",EDGE,"E497.MirrorCS");var subQ1=sQuery(id+"F5.wireOp",EDGE,"E438.MirrorCS");var subQ2=makeQuery(id+"F5.imprint","INTERSECT",VERTEX,{"derivedFrom":[subQ1,subQ0]});Q46=makeQuery(id+"F5.imprint","IMPRINT",FACE,{"disambiguationData":[TD([[makeQuery(id+"F5.imprint","IMPRINT",EDGE,{"disambiguationData":[TD([[subQ2,1.0]])],"derivedFrom":subQ1}),1.0]])]});}
            var Q47;
            {var subQ0=sQuery(id+"F5.wireOp",EDGE,"E375");Q47=makeQuery(id+"F5.imprint","IMPRINT",FACE,{"disambiguationData":[TD([[makeQuery(id+"F5.imprint","IMPRINT",EDGE,{"derivedFrom":subQ0}),-1.0]])]});}
            var Q48;
            {var subQ0=sQuery(id+"F5.wireOp",EDGE,"E508.MirrorCS");var subQ1=sQuery(id+"F5.wireOp",EDGE,"E437.MirrorCS");var subQ2=makeQuery(id+"F5.imprint","INTERSECT",VERTEX,{"derivedFrom":[subQ1,subQ0]});Q48=makeQuery(id+"F5.imprint","IMPRINT",FACE,{"disambiguationData":[TD([[makeQuery(id+"F5.imprint","IMPRINT",EDGE,{"disambiguationData":[TD([[subQ2,1.0]])],"derivedFrom":subQ1}),1.0]])]});}
            var Q49;
            {var subQ0=sQuery(id+"F5.wireOp",EDGE,"E817");Q49=makeQuery(id+"F5.imprint","IMPRINT",FACE,{"disambiguationData":[TD([[makeQuery(id+"F5.imprint","IMPRINT",EDGE,{"derivedFrom":subQ0}),1.0]])]});}
            var Q50;
            {var subQ0=sQuery(id+"F5.wireOp",EDGE,"E826");Q50=makeQuery(id+"F5.imprint","IMPRINT",FACE,{"disambiguationData":[TD([[makeQuery(id+"F5.imprint","IMPRINT",EDGE,{"derivedFrom":subQ0}),-1.0]])]});}
            var Q51;
            {var subQ0=sQuery(id+"F5.wireOp",EDGE,"E515.MirrorCS");var subQ1=sQuery(id+"F5.wireOp",EDGE,"E478.MirrorCS");var subQ2=makeQuery(id+"F5.imprint","INTERSECT",VERTEX,{"derivedFrom":[subQ1,subQ0]});Q51=makeQuery(id+"F5.imprint","IMPRINT",FACE,{"disambiguationData":[TD([[makeQuery(id+"F5.imprint","IMPRINT",EDGE,{"disambiguationData":[TD([[subQ2,-1.0]])],"derivedFrom":subQ1}),1.0]])]});}
            var Q52;
            {var subQ0=sQuery(id+"F5.wireOp",EDGE,"E515.MirrorCS");var subQ1=sQuery(id+"F5.wireOp",EDGE,"E448.MirrorCS");var subQ2=makeQuery(id+"F5.imprint","INTERSECT",VERTEX,{"derivedFrom":[subQ1,subQ0]});Q52=makeQuery(id+"F5.imprint","IMPRINT",FACE,{"disambiguationData":[TD([[makeQuery(id+"F5.imprint","IMPRINT",EDGE,{"disambiguationData":[TD([[subQ2,1.0]])],"derivedFrom":subQ1}),1.0]])]});}
            var Q53;
            {var subQ0=sQuery(id+"F5.wireOp",EDGE,"E522.MirrorCS");var subQ1=sQuery(id+"F5.wireOp",EDGE,"E452.MirrorCS");var subQ2=makeQuery(id+"F5.imprint","INTERSECT",VERTEX,{"derivedFrom":[subQ1,subQ0]});Q53=makeQuery(id+"F5.imprint","IMPRINT",FACE,{"disambiguationData":[TD([[makeQuery(id+"F5.imprint","IMPRINT",EDGE,{"disambiguationData":[TD([[subQ2,1.0]])],"derivedFrom":subQ1}),1.0]])]});}
            var Q54;
            {var subQ0=sQuery(id+"F5.wireOp",EDGE,"E508.MirrorCS");var subQ1=sQuery(id+"F5.wireOp",EDGE,"E458.MirrorCS");var subQ2=makeQuery(id+"F5.imprint","INTERSECT",VERTEX,{"derivedFrom":[subQ1,subQ0]});Q54=makeQuery(id+"F5.imprint","IMPRINT",FACE,{"disambiguationData":[TD([[makeQuery(id+"F5.imprint","IMPRINT",EDGE,{"disambiguationData":[TD([[subQ2,-1.0]])],"derivedFrom":subQ1}),1.0]])]});}
            var Q55;
            {var subQ0=sQuery(id+"F5.wireOp",EDGE,"E399");Q55=makeQuery(id+"F5.imprint","IMPRINT",FACE,{"disambiguationData":[TD([[makeQuery(id+"F5.imprint","IMPRINT",EDGE,{"derivedFrom":subQ0}),1.0]])]});}
            var Q56;
            {var subQ0=sQuery(id+"F5.wireOp",EDGE,"E828");Q56=makeQuery(id+"F5.imprint","IMPRINT",FACE,{"disambiguationData":[TD([[makeQuery(id+"F5.imprint","IMPRINT",EDGE,{"derivedFrom":subQ0}),1.0]])]});}
            var Q57;
            {var subQ0=sQuery(id+"F5.wireOp",EDGE,"E410");Q57=makeQuery(id+"F5.imprint","IMPRINT",FACE,{"disambiguationData":[TD([[makeQuery(id+"F5.imprint","IMPRINT",EDGE,{"derivedFrom":subQ0}),1.0]])]});}
            var Q58;
            {var subQ0=sQuery(id+"F5.wireOp",EDGE,"E377");Q58=makeQuery(id+"F5.imprint","IMPRINT",FACE,{"disambiguationData":[TD([[makeQuery(id+"F5.imprint","IMPRINT",EDGE,{"derivedFrom":subQ0}),1.0]])]});}
            var Q59;
            {var subQ0=sQuery(id+"F5.wireOp",EDGE,"E495.MirrorCS");var subQ1=sQuery(id+"F5.wireOp",EDGE,"E454.MirrorCS");var subQ2=makeQuery(id+"F5.imprint","INTERSECT",VERTEX,{"derivedFrom":[subQ1,subQ0]});Q59=makeQuery(id+"F5.imprint","IMPRINT",FACE,{"disambiguationData":[TD([[makeQuery(id+"F5.imprint","IMPRINT",EDGE,{"disambiguationData":[TD([[subQ2,1.0]])],"derivedFrom":subQ1}),1.0]])]});}
            var Q60;
            {var subQ0=sQuery(id+"F5.wireOp",EDGE,"E388");Q60=makeQuery(id+"F5.imprint","IMPRINT",FACE,{"disambiguationData":[TD([[makeQuery(id+"F5.imprint","IMPRINT",EDGE,{"derivedFrom":subQ0}),1.0]])]});}
            var Q61;
            {var subQ0=sQuery(id+"F5.wireOp",EDGE,"E522.MirrorCS");var subQ1=sQuery(id+"F5.wireOp",EDGE,"E470.MirrorCS");var subQ2=makeQuery(id+"F5.imprint","INTERSECT",VERTEX,{"derivedFrom":[subQ1,subQ0]});Q61=makeQuery(id+"F5.imprint","IMPRINT",FACE,{"disambiguationData":[TD([[makeQuery(id+"F5.imprint","IMPRINT",EDGE,{"disambiguationData":[TD([[subQ2,-1.0]])],"derivedFrom":subQ1}),1.0]])]});}
            var Q62;
            {var subQ0=sQuery(id+"F5.wireOp",EDGE,"E408");Q62=makeQuery(id+"F5.imprint","IMPRINT",FACE,{"disambiguationData":[TD([[makeQuery(id+"F5.imprint","IMPRINT",EDGE,{"derivedFrom":subQ0}),-1.0]])]});}
            var Q63;
            {var subQ0=sQuery(id+"F5.wireOp",EDGE,"E364");Q63=makeQuery(id+"F5.imprint","IMPRINT",FACE,{"disambiguationData":[TD([[makeQuery(id+"F5.imprint","IMPRINT",EDGE,{"derivedFrom":subQ0}),-1.0]])]});}
            var Q64;
            {var subQ0=sQuery(id+"F5.wireOp",EDGE,"E497.MirrorCS");var subQ1=sQuery(id+"F5.wireOp",EDGE,"E439.MirrorCS");var subQ2=makeQuery(id+"F5.imprint","INTERSECT",VERTEX,{"derivedFrom":[subQ1,subQ0]});Q64=makeQuery(id+"F5.imprint","IMPRINT",FACE,{"disambiguationData":[TD([[makeQuery(id+"F5.imprint","IMPRINT",EDGE,{"disambiguationData":[TD([[subQ2,-1.0]])],"derivedFrom":subQ1}),1.0]])]});}
            var Q65;
            {var subQ0=sQuery(id+"F5.wireOp",EDGE,"E386");Q65=makeQuery(id+"F5.imprint","IMPRINT",FACE,{"disambiguationData":[TD([[makeQuery(id+"F5.imprint","IMPRINT",EDGE,{"derivedFrom":subQ0}),-1.0]])]});}
            var Q66;
            {var subQ9=sQuery(id+"F5.wireOp",EDGE,"E351.bottom");Q66=makeQuery(id+"F5.imprint","IMPRINT",FACE,{"disambiguationData":[TD([[makeQuery(id+"F5.imprint","IMPRINT",EDGE,{"derivedFrom":subQ9}),-1.0]])]});}
            var Q67;
            {var subQ11=sQuery(id+"F5.wireOp",EDGE,"E301.bottom");Q67=makeQuery(id+"F5.imprint","IMPRINT",FACE,{"disambiguationData":[TD([[makeQuery(id+"F5.imprint","IMPRINT",EDGE,{"derivedFrom":subQ11}),-1.0]])]});}
            var Q68;
            {var subQ11=sQuery(id+"F5.wireOp",EDGE,"E326.bottom");Q68=makeQuery(id+"F5.imprint","IMPRINT",FACE,{"disambiguationData":[TD([[makeQuery(id+"F5.imprint","IMPRINT",EDGE,{"derivedFrom":subQ11}),-1.0]])]});}
            var Q69;
            {var subQ11=sQuery(id+"F5.wireOp",EDGE,"E340.bottom");Q69=makeQuery(id+"F5.imprint","IMPRINT",FACE,{"disambiguationData":[TD([[makeQuery(id+"F5.imprint","IMPRINT",EDGE,{"derivedFrom":subQ11}),-1.0]])]});}
            var Q70;
            {var subQ11=sQuery(id+"F5.wireOp",EDGE,"E362.bottom");Q70=makeQuery(id+"F5.imprint","IMPRINT",FACE,{"disambiguationData":[TD([[makeQuery(id+"F5.imprint","IMPRINT",EDGE,{"derivedFrom":subQ11}),-1.0]])]});}
            var Q71;
            {var subQ5=sQuery(id+"F5.wireOp",EDGE,"E354");Q71=makeQuery(id+"F5.imprint","IMPRINT",FACE,{"disambiguationData":[TD([[makeQuery(id+"F5.imprint","IMPRINT",EDGE,{"derivedFrom":subQ5}),1.0]])]});}
            var Q72;
            {var subQ1=sQuery(id+"F5.wireOp",EDGE,"E352");Q72=makeQuery(id+"F5.imprint","IMPRINT",FACE,{"disambiguationData":[TD([[makeQuery(id+"F5.imprint","IMPRINT",EDGE,{"derivedFrom":subQ1}),-1.0]])]});}
            var Q73;
            {var subQ5=sQuery(id+"F5.wireOp",EDGE,"E365");Q73=makeQuery(id+"F5.imprint","IMPRINT",FACE,{"disambiguationData":[TD([[makeQuery(id+"F5.imprint","IMPRINT",EDGE,{"derivedFrom":subQ5}),1.0]])]});}
            var Q74;
            {var subQ5=sQuery(id+"F5.wireOp",EDGE,"E341");Q74=makeQuery(id+"F5.imprint","IMPRINT",FACE,{"disambiguationData":[TD([[makeQuery(id+"F5.imprint","IMPRINT",EDGE,{"derivedFrom":subQ5}),-1.0]])]});}
            var Q75;
            {var subQ5=sQuery(id+"F5.wireOp",EDGE,"E302");Q75=makeQuery(id+"F5.imprint","IMPRINT",FACE,{"disambiguationData":[TD([[makeQuery(id+"F5.imprint","IMPRINT",EDGE,{"derivedFrom":subQ5}),-1.0]])]});}
            var Q76;
            {var subQ5=sQuery(id+"F5.wireOp",EDGE,"E329");Q76=makeQuery(id+"F5.imprint","IMPRINT",FACE,{"disambiguationData":[TD([[makeQuery(id+"F5.imprint","IMPRINT",EDGE,{"derivedFrom":subQ5}),1.0]])]});}
            var Q77;
            {var subQ5=sQuery(id+"F5.wireOp",EDGE,"E327");Q77=makeQuery(id+"F5.imprint","IMPRINT",FACE,{"disambiguationData":[TD([[makeQuery(id+"F5.imprint","IMPRINT",EDGE,{"derivedFrom":subQ5}),-1.0]])]});}
            var Q78;
            {var subQ5=sQuery(id+"F5.wireOp",EDGE,"E343");Q78=makeQuery(id+"F5.imprint","IMPRINT",FACE,{"disambiguationData":[TD([[makeQuery(id+"F5.imprint","IMPRINT",EDGE,{"derivedFrom":subQ5}),1.0]])]});}
            var Q79;
            {var subQ0=sQuery(id+"F5.wireOp",EDGE,"E305");Q79=makeQuery(id+"F5.imprint","IMPRINT",FACE,{"disambiguationData":[TD([[makeQuery(id+"F5.imprint","IMPRINT",EDGE,{"derivedFrom":subQ0}),1.0]])]});}
            var Q80;
            {var subQ0=sQuery(id+"F5.wireOp",EDGE,"E303");Q80=makeQuery(id+"F5.imprint","IMPRINT",FACE,{"disambiguationData":[TD([[makeQuery(id+"F5.imprint","IMPRINT",EDGE,{"derivedFrom":subQ0}),-1.0]])]});}
            var Q81;
            {var subQ0=sQuery(id+"F5.wireOp",EDGE,"E344");Q81=makeQuery(id+"F5.imprint","IMPRINT",FACE,{"disambiguationData":[TD([[makeQuery(id+"F5.imprint","IMPRINT",EDGE,{"derivedFrom":subQ0}),1.0]])]});}
            var Q82;
            {var subQ0=sQuery(id+"F5.wireOp",EDGE,"E330");Q82=makeQuery(id+"F5.imprint","IMPRINT",FACE,{"disambiguationData":[TD([[makeQuery(id+"F5.imprint","IMPRINT",EDGE,{"derivedFrom":subQ0}),1.0]])]});}
            var Q83;
            {var subQ0=sQuery(id+"F5.wireOp",EDGE,"E328");Q83=makeQuery(id+"F5.imprint","IMPRINT",FACE,{"disambiguationData":[TD([[makeQuery(id+"F5.imprint","IMPRINT",EDGE,{"derivedFrom":subQ0}),-1.0]])]});}
            var Q84;
            {var subQ0=sQuery(id+"F5.wireOp",EDGE,"E355");Q84=makeQuery(id+"F5.imprint","IMPRINT",FACE,{"disambiguationData":[TD([[makeQuery(id+"F5.imprint","IMPRINT",EDGE,{"derivedFrom":subQ0}),1.0]])]});}
            var Q85;
            {var subQ0=sQuery(id+"F5.wireOp",EDGE,"E342");Q85=makeQuery(id+"F5.imprint","IMPRINT",FACE,{"disambiguationData":[TD([[makeQuery(id+"F5.imprint","IMPRINT",EDGE,{"derivedFrom":subQ0}),-1.0]])]});}
            var Q86;
            {var subQ0=sQuery(id+"F5.wireOp",EDGE,"E647.MirrorCS");Q86=makeQuery(id+"F5.imprint","IMPRINT",FACE,{"disambiguationData":[TD([[makeQuery(id+"F5.imprint","IMPRINT",EDGE,{"derivedFrom":subQ0}),-1.0]])]});}
            var Q87;
            {var subQ0=sQuery(id+"F5.wireOp",EDGE,"E685.MirrorCS");Q87=makeQuery(id+"F5.imprint","IMPRINT",FACE,{"disambiguationData":[TD([[makeQuery(id+"F5.imprint","IMPRINT",EDGE,{"derivedFrom":subQ0}),-1.0]])]});}
            var Q88;
            {var subQ0=sQuery(id+"F5.wireOp",EDGE,"E619.MirrorCS");Q88=makeQuery(id+"F5.imprint","IMPRINT",FACE,{"disambiguationData":[TD([[makeQuery(id+"F5.imprint","IMPRINT",EDGE,{"derivedFrom":subQ0}),1.0]])]});}
            var Q89;
            {var subQ0=sQuery(id+"F5.wireOp",EDGE,"E628.MirrorCS");Q89=makeQuery(id+"F5.imprint","IMPRINT",FACE,{"disambiguationData":[TD([[makeQuery(id+"F5.imprint","IMPRINT",EDGE,{"derivedFrom":subQ0}),-1.0]])]});}
            var Q90;
            {var subQ0=sQuery(id+"F5.wireOp",EDGE,"E681.MirrorCS");var subQ1=sQuery(id+"F5.wireOp",EDGE,"E604.MirrorCS");var subQ2=makeQuery(id+"F5.imprint","INTERSECT",VERTEX,{"derivedFrom":[subQ1,subQ0]});Q90=makeQuery(id+"F5.imprint","IMPRINT",FACE,{"disambiguationData":[TD([[makeQuery(id+"F5.imprint","IMPRINT",EDGE,{"disambiguationData":[TD([[subQ2,-1.0]])],"derivedFrom":subQ1}),-1.0]])]});}
            var Q91;
            {var subQ0=sQuery(id+"F5.wireOp",EDGE,"E681.MirrorCS");var subQ1=sQuery(id+"F5.wireOp",EDGE,"E567.MirrorCS");var subQ2=makeQuery(id+"F5.imprint","INTERSECT",VERTEX,{"derivedFrom":[subQ1,subQ0]});Q91=makeQuery(id+"F5.imprint","IMPRINT",FACE,{"disambiguationData":[TD([[makeQuery(id+"F5.imprint","IMPRINT",EDGE,{"disambiguationData":[TD([[subQ2,1.0]])],"derivedFrom":subQ1}),-1.0]])]});}
            var Q92;
            {var subQ0=sQuery(id+"F5.wireOp",EDGE,"E635.MirrorCS");var subQ1=sQuery(id+"F5.wireOp",EDGE,"E612.MirrorCS");var subQ2=makeQuery(id+"F5.imprint","INTERSECT",VERTEX,{"derivedFrom":[subQ1,subQ0]});Q92=makeQuery(id+"F5.imprint","IMPRINT",FACE,{"disambiguationData":[TD([[makeQuery(id+"F5.imprint","IMPRINT",EDGE,{"disambiguationData":[TD([[subQ2,-1.0]])],"derivedFrom":subQ1}),-1.0]])]});}
            var Q93;
            {var subQ0=sQuery(id+"F5.wireOp",EDGE,"E626.MirrorCS");Q93=makeQuery(id+"F5.imprint","IMPRINT",FACE,{"disambiguationData":[TD([[makeQuery(id+"F5.imprint","IMPRINT",EDGE,{"derivedFrom":subQ0}),1.0]])]});}
            var Q94;
            {var subQ0=sQuery(id+"F5.wireOp",EDGE,"E684.MirrorCS");var subQ1=sQuery(id+"F5.wireOp",EDGE,"E598.MirrorCS");var subQ2=makeQuery(id+"F5.imprint","INTERSECT",VERTEX,{"derivedFrom":[subQ1,subQ0]});Q94=makeQuery(id+"F5.imprint","IMPRINT",FACE,{"disambiguationData":[TD([[makeQuery(id+"F5.imprint","IMPRINT",EDGE,{"disambiguationData":[TD([[subQ2,-1.0]])],"derivedFrom":subQ1}),-1.0]])]});}
            var Q95;
            {var subQ0=sQuery(id+"F5.wireOp",EDGE,"E635.MirrorCS");var subQ1=sQuery(id+"F5.wireOp",EDGE,"E582.MirrorCS");var subQ2=makeQuery(id+"F5.imprint","INTERSECT",VERTEX,{"derivedFrom":[subQ1,subQ0]});Q95=makeQuery(id+"F5.imprint","IMPRINT",FACE,{"disambiguationData":[TD([[makeQuery(id+"F5.imprint","IMPRINT",EDGE,{"disambiguationData":[TD([[subQ2,1.0]])],"derivedFrom":subQ1}),-1.0]])]});}
            var Q96;
            {var subQ0=sQuery(id+"F5.wireOp",EDGE,"E746.MirrorCS");Q96=makeQuery(id+"F5.imprint","IMPRINT",FACE,{"disambiguationData":[TD([[makeQuery(id+"F5.imprint","IMPRINT",EDGE,{"derivedFrom":subQ0}),1.0]])]});}
            var Q97;
            {var subQ7=sQuery(id+"F5.wireOp",EDGE,"E748.MirrorCS");Q97=makeQuery(id+"F5.imprint","IMPRINT",FACE,{"disambiguationData":[TD([[makeQuery(id+"F5.imprint","IMPRINT",EDGE,{"derivedFrom":subQ7}),1.0]])]});}
            var Q98;
            {var subQ7=sQuery(id+"F5.wireOp",EDGE,"E683.MirrorCS");Q98=makeQuery(id+"F5.imprint","IMPRINT",FACE,{"disambiguationData":[TD([[makeQuery(id+"F5.imprint","IMPRINT",EDGE,{"derivedFrom":subQ7}),-1.0]])]});}
            var Q99;
            {var subQ0=sQuery(id+"F5.wireOp",EDGE,"E744.MirrorCS");Q99=makeQuery(id+"F5.imprint","IMPRINT",FACE,{"disambiguationData":[TD([[makeQuery(id+"F5.imprint","IMPRINT",EDGE,{"derivedFrom":subQ0}),1.0]])]});}
            var Q100;
            {var subQ0=sQuery(id+"F5.wireOp",EDGE,"E747.MirrorCS");Q100=makeQuery(id+"F5.imprint","IMPRINT",FACE,{"disambiguationData":[TD([[makeQuery(id+"F5.imprint","IMPRINT",EDGE,{"derivedFrom":subQ0}),1.0]])]});}
            var Q101;
            {var subQ5=sQuery(id+"F5.wireOp",EDGE,"E671.MirrorCS");Q101=makeQuery(id+"F5.imprint","IMPRINT",FACE,{"disambiguationData":[TD([[makeQuery(id+"F5.imprint","IMPRINT",EDGE,{"derivedFrom":subQ5}),-1.0]])]});}
            var Q102;
            {var subQ9=sQuery(id+"F5.wireOp",EDGE,"E320.MirrorCS");Q102=makeQuery(id+"F5.imprint","IMPRINT",FACE,{"disambiguationData":[TD([[makeQuery(id+"F5.imprint","IMPRINT",EDGE,{"derivedFrom":subQ9}),1.0]])]});}
            var Q103;
            {var subQ0=sQuery(id+"F5.wireOp",EDGE,"E633.MirrorCS");Q103=makeQuery(id+"F5.imprint","IMPRINT",FACE,{"disambiguationData":[TD([[makeQuery(id+"F5.imprint","IMPRINT",EDGE,{"derivedFrom":subQ0}),-1.0]])]});}
            var Q104;
            {var subQ1=sQuery(id+"F5.wireOp",EDGE,"E585.MirrorCS");Q104=makeQuery(id+"F5.imprint","IMPRINT",FACE,{"disambiguationData":[TD([[makeQuery(id+"F5.imprint","IMPRINT",EDGE,{"derivedFrom":subQ1}),-1.0]])]});}
            var Q105;
            {var subQ0=sQuery(id+"F5.wireOp",EDGE,"E771.MirrorCS");Q105=makeQuery(id+"F5.imprint","IMPRINT",FACE,{"disambiguationData":[TD([[makeQuery(id+"F5.imprint","IMPRINT",EDGE,{"derivedFrom":subQ0}),-1.0]])]});}
            var Q106;
            {var subQ4=sQuery(id+"F5.wireOp",EDGE,"E687.MirrorCS");Q106=makeQuery(id+"F5.imprint","IMPRINT",FACE,{"disambiguationData":[TD([[makeQuery(id+"F5.imprint","IMPRINT",EDGE,{"derivedFrom":subQ4}),1.0]])]});}
            var Q107;
            {var subQ0=sQuery(id+"F5.wireOp",EDGE,"E787.MirrorCS");Q107=makeQuery(id+"F5.imprint","IMPRINT",FACE,{"disambiguationData":[TD([[makeQuery(id+"F5.imprint","IMPRINT",EDGE,{"derivedFrom":subQ0}),1.0]])]});}
            var Q108;
            {var subQ0=sQuery(id+"F5.wireOp",EDGE,"E753.MirrorCS");Q108=makeQuery(id+"F5.imprint","IMPRINT",FACE,{"disambiguationData":[TD([[makeQuery(id+"F5.imprint","IMPRINT",EDGE,{"derivedFrom":subQ0}),1.0]])]});}
            var Q109;
            {var subQ0=sQuery(id+"F5.wireOp",EDGE,"E767.MirrorCS");Q109=makeQuery(id+"F5.imprint","IMPRINT",FACE,{"disambiguationData":[TD([[makeQuery(id+"F5.imprint","IMPRINT",EDGE,{"derivedFrom":subQ0}),1.0]])]});}
            var Q110;
            {var subQ0=sQuery(id+"F5.wireOp",EDGE,"E668.MirrorCS");Q110=makeQuery(id+"F5.imprint","IMPRINT",FACE,{"disambiguationData":[TD([[makeQuery(id+"F5.imprint","IMPRINT",EDGE,{"derivedFrom":subQ0}),-1.0]])]});}
            var Q111;
            {var subQ0=sQuery(id+"F5.wireOp",EDGE,"E766.MirrorCS");Q111=makeQuery(id+"F5.imprint","IMPRINT",FACE,{"disambiguationData":[TD([[makeQuery(id+"F5.imprint","IMPRINT",EDGE,{"derivedFrom":subQ0}),-1.0]])]});}
            var Q112;
            {var subQ0=sQuery(id+"F5.wireOp",EDGE,"E652.MirrorCS");Q112=makeQuery(id+"F5.imprint","IMPRINT",FACE,{"disambiguationData":[TD([[makeQuery(id+"F5.imprint","IMPRINT",EDGE,{"derivedFrom":subQ0}),1.0]])]});}
            var Q113;
            {var subQ0=sQuery(id+"F5.wireOp",EDGE,"E788.MirrorCS");Q113=makeQuery(id+"F5.imprint","IMPRINT",FACE,{"disambiguationData":[TD([[makeQuery(id+"F5.imprint","IMPRINT",EDGE,{"derivedFrom":subQ0}),-1.0]])]});}
            var Q114;
            {var subQ0=sQuery(id+"F5.wireOp",EDGE,"E772.MirrorCS");Q114=makeQuery(id+"F5.imprint","IMPRINT",FACE,{"disambiguationData":[TD([[makeQuery(id+"F5.imprint","IMPRINT",EDGE,{"derivedFrom":subQ0}),-1.0]])]});}
            var Q115;
            {var subQ0=sQuery(id+"F5.wireOp",EDGE,"E755.MirrorCS");Q115=makeQuery(id+"F5.imprint","IMPRINT",FACE,{"disambiguationData":[TD([[makeQuery(id+"F5.imprint","IMPRINT",EDGE,{"derivedFrom":subQ0}),-1.0]])]});}
            var Q116;
            {var subQ0=sQuery(id+"F5.wireOp",EDGE,"E639.MirrorCS");Q116=makeQuery(id+"F5.imprint","IMPRINT",FACE,{"disambiguationData":[TD([[makeQuery(id+"F5.imprint","IMPRINT",EDGE,{"derivedFrom":subQ0}),1.0]])]});}
            var Q117;
            {var subQ0=sQuery(id+"F5.wireOp",EDGE,"E642.MirrorCS");Q117=makeQuery(id+"F5.imprint","IMPRINT",FACE,{"disambiguationData":[TD([[makeQuery(id+"F5.imprint","IMPRINT",EDGE,{"derivedFrom":subQ0}),-1.0]])]});}
            var Q118;
            {var subQ0=sQuery(id+"F5.wireOp",EDGE,"E322.MirrorCS");Q118=makeQuery(id+"F5.imprint","IMPRINT",FACE,{"disambiguationData":[TD([[makeQuery(id+"F5.imprint","IMPRINT",EDGE,{"derivedFrom":subQ0}),-1.0]])]});}
            var Q119;
            {var subQ0=sQuery(id+"F5.wireOp",EDGE,"E653.MirrorCS");Q119=makeQuery(id+"F5.imprint","IMPRINT",FACE,{"disambiguationData":[TD([[makeQuery(id+"F5.imprint","IMPRINT",EDGE,{"derivedFrom":subQ0}),1.0]])]});}
            var Q120;
            {var subQ0=sQuery(id+"F5.wireOp",EDGE,"E655.MirrorCS");Q120=makeQuery(id+"F5.imprint","IMPRINT",FACE,{"disambiguationData":[TD([[makeQuery(id+"F5.imprint","IMPRINT",EDGE,{"derivedFrom":subQ0}),1.0]])]});}
            var Q121;
            {var subQ0=sQuery(id+"F5.wireOp",EDGE,"E321.MirrorCS");Q121=makeQuery(id+"F5.imprint","IMPRINT",FACE,{"disambiguationData":[TD([[makeQuery(id+"F5.imprint","IMPRINT",EDGE,{"derivedFrom":subQ0}),1.0]])]});}
            var Q122;
            {var subQ0=sQuery(id+"F5.wireOp",EDGE,"E323.MirrorCS");var subQ1=sQuery(id+"F5.wireOp",EDGE,"E315.MirrorCS");var subQ2=makeQuery(id+"F5.imprint","INTERSECT",VERTEX,{"derivedFrom":[subQ1,subQ0]});Q122=makeQuery(id+"F5.imprint","IMPRINT",FACE,{"disambiguationData":[TD([[makeQuery(id+"F5.imprint","IMPRINT",EDGE,{"disambiguationData":[TD([[subQ2,1.0]])],"derivedFrom":subQ1}),1.0]])]});}
            var Q123;
            {var subQ0=sQuery(id+"F5.wireOp",EDGE,"E323.MirrorCS");var subQ1=sQuery(id+"F5.wireOp",EDGE,"E314.MirrorCS");var subQ2=makeQuery(id+"F5.imprint","INTERSECT",VERTEX,{"derivedFrom":[subQ1,subQ0]});Q123=makeQuery(id+"F5.imprint","IMPRINT",FACE,{"disambiguationData":[TD([[makeQuery(id+"F5.imprint","IMPRINT",EDGE,{"disambiguationData":[TD([[subQ2,-1.0]])],"derivedFrom":subQ1}),1.0]])]});}
            var Q124;
            {var subQ0=sQuery(id+"F5.wireOp",EDGE,"E664.MirrorCS");var subQ1=sQuery(id+"F5.wireOp",EDGE,"E614.MirrorCS");var subQ2=makeQuery(id+"F5.imprint","INTERSECT",VERTEX,{"derivedFrom":[subQ1,subQ0]});Q124=makeQuery(id+"F5.imprint","IMPRINT",FACE,{"disambiguationData":[TD([[makeQuery(id+"F5.imprint","IMPRINT",EDGE,{"disambiguationData":[TD([[subQ2,1.0]])],"derivedFrom":subQ1}),-1.0]])]});}
            var Q125;
            {var subQ0=sQuery(id+"F5.wireOp",EDGE,"E636.MirrorCS");var subQ1=sQuery(id+"F5.wireOp",EDGE,"E611.MirrorCS");var subQ2=makeQuery(id+"F5.imprint","INTERSECT",VERTEX,{"derivedFrom":[subQ1,subQ0]});Q125=makeQuery(id+"F5.imprint","IMPRINT",FACE,{"disambiguationData":[TD([[makeQuery(id+"F5.imprint","IMPRINT",EDGE,{"disambiguationData":[TD([[subQ2,1.0]])],"derivedFrom":subQ1}),-1.0]])]});}
            var Q126;
            {var subQ0=sQuery(id+"F5.wireOp",EDGE,"E617.MirrorCS");var subQ1=sQuery(id+"F5.wireOp",EDGE,"E613.MirrorCS");var subQ2=makeQuery(id+"F5.imprint","INTERSECT",VERTEX,{"derivedFrom":[subQ1,subQ0]});Q126=makeQuery(id+"F5.imprint","IMPRINT",FACE,{"disambiguationData":[TD([[makeQuery(id+"F5.imprint","IMPRINT",EDGE,{"disambiguationData":[TD([[subQ2,1.0]])],"derivedFrom":subQ1}),-1.0]])]});}
            var Q127;
            {var subQ0=sQuery(id+"F5.wireOp",EDGE,"E664.MirrorCS");var subQ1=sQuery(id+"F5.wireOp",EDGE,"E563.MirrorCS");var subQ2=makeQuery(id+"F5.imprint","INTERSECT",VERTEX,{"derivedFrom":[subQ1,subQ0]});Q127=makeQuery(id+"F5.imprint","IMPRINT",FACE,{"disambiguationData":[TD([[makeQuery(id+"F5.imprint","IMPRINT",EDGE,{"disambiguationData":[TD([[subQ2,-1.0]])],"derivedFrom":subQ1}),-1.0]])]});}
            var Q128;
            {var subQ0=sQuery(id+"F5.wireOp",EDGE,"E764.MirrorCS");var subQ1=sQuery(id+"F5.wireOp",EDGE,"E738.MirrorCS");var subQ2=makeQuery(id+"F5.imprint","INTERSECT",VERTEX,{"derivedFrom":[subQ1,subQ0]});Q128=makeQuery(id+"F5.imprint","IMPRINT",FACE,{"disambiguationData":[TD([[makeQuery(id+"F5.imprint","IMPRINT",EDGE,{"disambiguationData":[TD([[subQ2,1.0]])],"derivedFrom":subQ1}),1.0]])]});}
            var Q129;
            {var subQ0=sQuery(id+"F5.wireOp",EDGE,"E791.MirrorCS");var subQ1=sQuery(id+"F5.wireOp",EDGE,"E705.MirrorCS");var subQ2=makeQuery(id+"F5.imprint","INTERSECT",VERTEX,{"derivedFrom":[subQ1,subQ0]});Q129=makeQuery(id+"F5.imprint","IMPRINT",FACE,{"disambiguationData":[TD([[makeQuery(id+"F5.imprint","IMPRINT",EDGE,{"disambiguationData":[TD([[subQ2,1.0]])],"derivedFrom":subQ1}),1.0]])]});}
            var Q130;
            {var subQ0=sQuery(id+"F5.wireOp",EDGE,"E789.MirrorCS");var subQ1=sQuery(id+"F5.wireOp",EDGE,"E716.MirrorCS");var subQ2=makeQuery(id+"F5.imprint","INTERSECT",VERTEX,{"derivedFrom":[subQ1,subQ0]});Q130=makeQuery(id+"F5.imprint","IMPRINT",FACE,{"disambiguationData":[TD([[makeQuery(id+"F5.imprint","IMPRINT",EDGE,{"disambiguationData":[TD([[subQ2,-1.0]])],"derivedFrom":subQ1}),1.0]])]});}
            var Q131;
            {var subQ0=sQuery(id+"F5.wireOp",EDGE,"E764.MirrorCS");var subQ1=sQuery(id+"F5.wireOp",EDGE,"E694.MirrorCS");var subQ2=makeQuery(id+"F5.imprint","INTERSECT",VERTEX,{"derivedFrom":[subQ1,subQ0]});Q131=makeQuery(id+"F5.imprint","IMPRINT",FACE,{"disambiguationData":[TD([[makeQuery(id+"F5.imprint","IMPRINT",EDGE,{"disambiguationData":[TD([[subQ2,-1.0]])],"derivedFrom":subQ1}),1.0]])]});}
            var Q132;
            {var subQ0=sQuery(id+"F5.wireOp",EDGE,"E805.MirrorCS");var subQ1=sQuery(id+"F5.wireOp",EDGE,"E734.MirrorCS");var subQ2=makeQuery(id+"F5.imprint","INTERSECT",VERTEX,{"derivedFrom":[subQ1,subQ0]});Q132=makeQuery(id+"F5.imprint","IMPRINT",FACE,{"disambiguationData":[TD([[makeQuery(id+"F5.imprint","IMPRINT",EDGE,{"disambiguationData":[TD([[subQ2,1.0]])],"derivedFrom":subQ1}),1.0]])]});}
            var Q133;
            {var subQ0=sQuery(id+"F5.wireOp",EDGE,"E789.MirrorCS");var subQ1=sQuery(id+"F5.wireOp",EDGE,"E741.MirrorCS");var subQ2=makeQuery(id+"F5.imprint","INTERSECT",VERTEX,{"derivedFrom":[subQ1,subQ0]});Q133=makeQuery(id+"F5.imprint","IMPRINT",FACE,{"disambiguationData":[TD([[makeQuery(id+"F5.imprint","IMPRINT",EDGE,{"disambiguationData":[TD([[subQ2,1.0]])],"derivedFrom":subQ1}),1.0]])]});}
            var Q134;
            {var subQ0=sQuery(id+"F5.wireOp",EDGE,"E646.MirrorCS");var subQ1=sQuery(id+"F5.wireOp",EDGE,"E607.MirrorCS");var subQ2=makeQuery(id+"F5.imprint","INTERSECT",VERTEX,{"derivedFrom":[subQ1,subQ0]});Q134=makeQuery(id+"F5.imprint","IMPRINT",FACE,{"disambiguationData":[TD([[makeQuery(id+"F5.imprint","IMPRINT",EDGE,{"disambiguationData":[TD([[subQ2,-1.0]])],"derivedFrom":subQ1}),-1.0]])]});}
            var Q135;
            {var subQ0=sQuery(id+"F5.wireOp",EDGE,"E646.MirrorCS");var subQ1=sQuery(id+"F5.wireOp",EDGE,"E574.MirrorCS");var subQ2=makeQuery(id+"F5.imprint","INTERSECT",VERTEX,{"derivedFrom":[subQ1,subQ0]});Q135=makeQuery(id+"F5.imprint","IMPRINT",FACE,{"disambiguationData":[TD([[makeQuery(id+"F5.imprint","IMPRINT",EDGE,{"disambiguationData":[TD([[subQ2,1.0]])],"derivedFrom":subQ1}),-1.0]])]});}
            var Q136;
            {var subQ0=sQuery(id+"F5.wireOp",EDGE,"E791.MirrorCS");var subQ1=sQuery(id+"F5.wireOp",EDGE,"E689.MirrorCS");var subQ2=makeQuery(id+"F5.imprint","INTERSECT",VERTEX,{"derivedFrom":[subQ1,subQ0]});Q136=makeQuery(id+"F5.imprint","IMPRINT",FACE,{"disambiguationData":[TD([[makeQuery(id+"F5.imprint","IMPRINT",EDGE,{"disambiguationData":[TD([[subQ2,-1.0]])],"derivedFrom":subQ1}),1.0]])]});}
            var Q137;
            {var subQ0=sQuery(id+"F5.wireOp",EDGE,"E636.MirrorCS");var subQ1=sQuery(id+"F5.wireOp",EDGE,"E577.MirrorCS");var subQ2=makeQuery(id+"F5.imprint","INTERSECT",VERTEX,{"derivedFrom":[subQ1,subQ0]});Q137=makeQuery(id+"F5.imprint","IMPRINT",FACE,{"disambiguationData":[TD([[makeQuery(id+"F5.imprint","IMPRINT",EDGE,{"disambiguationData":[TD([[subQ2,-1.0]])],"derivedFrom":subQ1}),-1.0]])]});}
            var Q138;
            {var subQ0=sQuery(id+"F5.wireOp",EDGE,"E743.MirrorCS");Q138=makeQuery(id+"F5.imprint","IMPRINT",FACE,{"disambiguationData":[TD([[makeQuery(id+"F5.imprint","IMPRINT",EDGE,{"derivedFrom":subQ0}),1.0]])]});}
            var Q139;
            {var subQ10=sQuery(id+"F5.wireOp",EDGE,"E745.MirrorCS");Q139=makeQuery(id+"F5.imprint","IMPRINT",FACE,{"disambiguationData":[TD([[makeQuery(id+"F5.imprint","IMPRINT",EDGE,{"derivedFrom":subQ10}),1.0]])]});}
            var Q140;
            {var subQ0=sQuery(id+"F5.wireOp",EDGE,"E773.MirrorCS");Q140=makeQuery(id+"F5.imprint","IMPRINT",FACE,{"disambiguationData":[TD([[makeQuery(id+"F5.imprint","IMPRINT",EDGE,{"derivedFrom":subQ0}),1.0]])]});}
            var Q141;
            {var subQ0=sQuery(id+"F5.wireOp",EDGE,"E811.MirrorCS");Q141=makeQuery(id+"F5.imprint","IMPRINT",FACE,{"disambiguationData":[TD([[makeQuery(id+"F5.imprint","IMPRINT",EDGE,{"derivedFrom":subQ0}),1.0]])]});}
            var Q142;
            {var subQ0=sQuery(id+"F5.wireOp",EDGE,"E807.MirrorCS");Q142=makeQuery(id+"F5.imprint","IMPRINT",FACE,{"disambiguationData":[TD([[makeQuery(id+"F5.imprint","IMPRINT",EDGE,{"derivedFrom":subQ0}),1.0]])]});}
            var Q143;
            {var subQ0=sQuery(id+"F5.wireOp",EDGE,"E802.MirrorCS");Q143=makeQuery(id+"F5.imprint","IMPRINT",FACE,{"disambiguationData":[TD([[makeQuery(id+"F5.imprint","IMPRINT",EDGE,{"derivedFrom":subQ0}),-1.0]])]});}
            var Q144;
            {var subQ0=sQuery(id+"F5.wireOp",EDGE,"E801.MirrorCS");Q144=makeQuery(id+"F5.imprint","IMPRINT",FACE,{"disambiguationData":[TD([[makeQuery(id+"F5.imprint","IMPRINT",EDGE,{"derivedFrom":subQ0}),-1.0]])]});}
            var Q145;
            {var subQ0=sQuery(id+"F5.wireOp",EDGE,"E803.MirrorCS");Q145=makeQuery(id+"F5.imprint","IMPRINT",FACE,{"disambiguationData":[TD([[makeQuery(id+"F5.imprint","IMPRINT",EDGE,{"derivedFrom":subQ0}),1.0]])]});}
            var Q146;
            {var subQ0=sQuery(id+"F5.wireOp",EDGE,"E798.MirrorCS");var subQ1=sQuery(id+"F5.wireOp",EDGE,"E731.MirrorCS");var subQ2=makeQuery(id+"F5.imprint","INTERSECT",VERTEX,{"derivedFrom":[subQ1,subQ0]});Q146=makeQuery(id+"F5.imprint","IMPRINT",FACE,{"disambiguationData":[TD([[makeQuery(id+"F5.imprint","IMPRINT",EDGE,{"disambiguationData":[TD([[subQ2,-1.0]])],"derivedFrom":subQ1}),1.0]])]});}
            var Q147;
            {var subQ0=sQuery(id+"F5.wireOp",EDGE,"E774.MirrorCS");var subQ1=sQuery(id+"F5.wireOp",EDGE,"E709.MirrorCS");var subQ2=makeQuery(id+"F5.imprint","INTERSECT",VERTEX,{"derivedFrom":[subQ1,subQ0]});Q147=makeQuery(id+"F5.imprint","IMPRINT",FACE,{"disambiguationData":[TD([[makeQuery(id+"F5.imprint","IMPRINT",EDGE,{"disambiguationData":[TD([[subQ2,1.0]])],"derivedFrom":subQ1}),1.0]])]});}
            var Q148;
            {var subQ0=sQuery(id+"F5.wireOp",EDGE,"E781.MirrorCS");var subQ1=sQuery(id+"F5.wireOp",EDGE,"E725.MirrorCS");var subQ2=makeQuery(id+"F5.imprint","INTERSECT",VERTEX,{"derivedFrom":[subQ1,subQ0]});Q148=makeQuery(id+"F5.imprint","IMPRINT",FACE,{"disambiguationData":[TD([[makeQuery(id+"F5.imprint","IMPRINT",EDGE,{"disambiguationData":[TD([[subQ2,-1.0]])],"derivedFrom":subQ1}),1.0]])]});}
            var Q149;
            {var subQ0=sQuery(id+"F5.wireOp",EDGE,"E774.MirrorCS");var subQ1=sQuery(id+"F5.wireOp",EDGE,"E728.MirrorCS");var subQ2=makeQuery(id+"F5.imprint","INTERSECT",VERTEX,{"derivedFrom":[subQ1,subQ0]});Q149=makeQuery(id+"F5.imprint","IMPRINT",FACE,{"disambiguationData":[TD([[makeQuery(id+"F5.imprint","IMPRINT",EDGE,{"disambiguationData":[TD([[subQ2,-1.0]])],"derivedFrom":subQ1}),1.0]])]});}
            var Q150;
            {var subQ0=sQuery(id+"F5.wireOp",EDGE,"E781.MirrorCS");var subQ1=sQuery(id+"F5.wireOp",EDGE,"E699.MirrorCS");var subQ2=makeQuery(id+"F5.imprint","INTERSECT",VERTEX,{"derivedFrom":[subQ1,subQ0]});Q150=makeQuery(id+"F5.imprint","IMPRINT",FACE,{"disambiguationData":[TD([[makeQuery(id+"F5.imprint","IMPRINT",EDGE,{"disambiguationData":[TD([[subQ2,1.0]])],"derivedFrom":subQ1}),1.0]])]});}
            var Q151;
            {var subQ0=sQuery(id+"F5.wireOp",EDGE,"E798.MirrorCS");var subQ1=sQuery(id+"F5.wireOp",EDGE,"E703.MirrorCS");var subQ2=makeQuery(id+"F5.imprint","INTERSECT",VERTEX,{"derivedFrom":[subQ1,subQ0]});Q151=makeQuery(id+"F5.imprint","IMPRINT",FACE,{"disambiguationData":[TD([[makeQuery(id+"F5.imprint","IMPRINT",EDGE,{"disambiguationData":[TD([[subQ2,1.0]])],"derivedFrom":subQ1}),1.0]])]});}
            var Q152;
            {var subQ7=sQuery(id+"F5.wireOp",EDGE,"E648.MirrorCS");Q152=makeQuery(id+"F5.imprint","IMPRINT",FACE,{"disambiguationData":[TD([[makeQuery(id+"F5.imprint","IMPRINT",EDGE,{"derivedFrom":subQ7}),-1.0]])]});}
            var Q153;
            {var subQ0=sQuery(id+"F5.wireOp",EDGE,"E679.MirrorCS");Q153=makeQuery(id+"F5.imprint","IMPRINT",FACE,{"disambiguationData":[TD([[makeQuery(id+"F5.imprint","IMPRINT",EDGE,{"derivedFrom":subQ0}),-1.0]])]});}
            var Q154;
            {var subQ0=sQuery(id+"F5.wireOp",EDGE,"E630.MirrorCS");Q154=makeQuery(id+"F5.imprint","IMPRINT",FACE,{"disambiguationData":[TD([[makeQuery(id+"F5.imprint","IMPRINT",EDGE,{"derivedFrom":subQ0}),-1.0]])]});}
            var Q155;
            {var subQ0=sQuery(id+"F5.wireOp",EDGE,"E666.MirrorCS");Q155=makeQuery(id+"F5.imprint","IMPRINT",FACE,{"disambiguationData":[TD([[makeQuery(id+"F5.imprint","IMPRINT",EDGE,{"derivedFrom":subQ0}),1.0]])]});}
            var Q156;
            {var subQ0=sQuery(id+"F5.wireOp",EDGE,"E669.MirrorCS");Q156=makeQuery(id+"F5.imprint","IMPRINT",FACE,{"disambiguationData":[TD([[makeQuery(id+"F5.imprint","IMPRINT",EDGE,{"derivedFrom":subQ0}),-1.0]])]});}
            var Q157;
            {var subQ5=sQuery(id+"F5.wireOp",EDGE,"E678.MirrorCS");Q157=makeQuery(id+"F5.imprint","IMPRINT",FACE,{"disambiguationData":[TD([[makeQuery(id+"F5.imprint","IMPRINT",EDGE,{"derivedFrom":subQ5}),-1.0]])]});}
            extrude(context, id + "F6", {"entities" : qUnion([Q0, Q1, Q2, Q3, Q4, Q5, Q6, Q7, Q8, Q9, Q10, Q11, Q12, Q13, Q14, Q15, Q16, Q17, Q18, Q19, Q20, Q21, Q22, Q23, Q24, Q25, Q26, Q27, Q28, Q29, Q30, Q31, Q32, Q33, Q34, Q35, Q36, Q37, Q38, Q39, Q40, Q41, Q42, Q43, Q44, Q45, Q46, Q47, Q48, Q49, Q50, Q51, Q52, Q53, Q54, Q55, Q56, Q57, Q58, Q59, Q60, Q61, Q62, Q63, Q64, Q65, Q66, Q67, Q68, Q69, Q70, Q71, Q72, Q73, Q74, Q75, Q76, Q77, Q78, Q79, Q80, Q81, Q82, Q83, Q84, Q85, Q86, Q87, Q88, Q89, Q90, Q91, Q92, Q93, Q94, Q95, Q96, Q97, Q98, Q99, Q100, Q101, Q102, Q103, Q104, Q105, Q106, Q107, Q108, Q109, Q110, Q111, Q112, Q113, Q114, Q115, Q116, Q117, Q118, Q119, Q120, Q121, Q122, Q123, Q124, Q125, Q126, Q127, Q128, Q129, Q130, Q131, Q132, Q133, Q134, Q135, Q136, Q137, Q138, Q139, Q140, Q141, Q142, Q143, Q144, Q145, Q146, Q147, Q148, Q149, Q150, Q151, Q152, Q153, Q154, Q155, Q156, Q157]), "operationType" : NewBodyOperationType.ADD, "depth" : 12.7 * mm});
        }
    });
